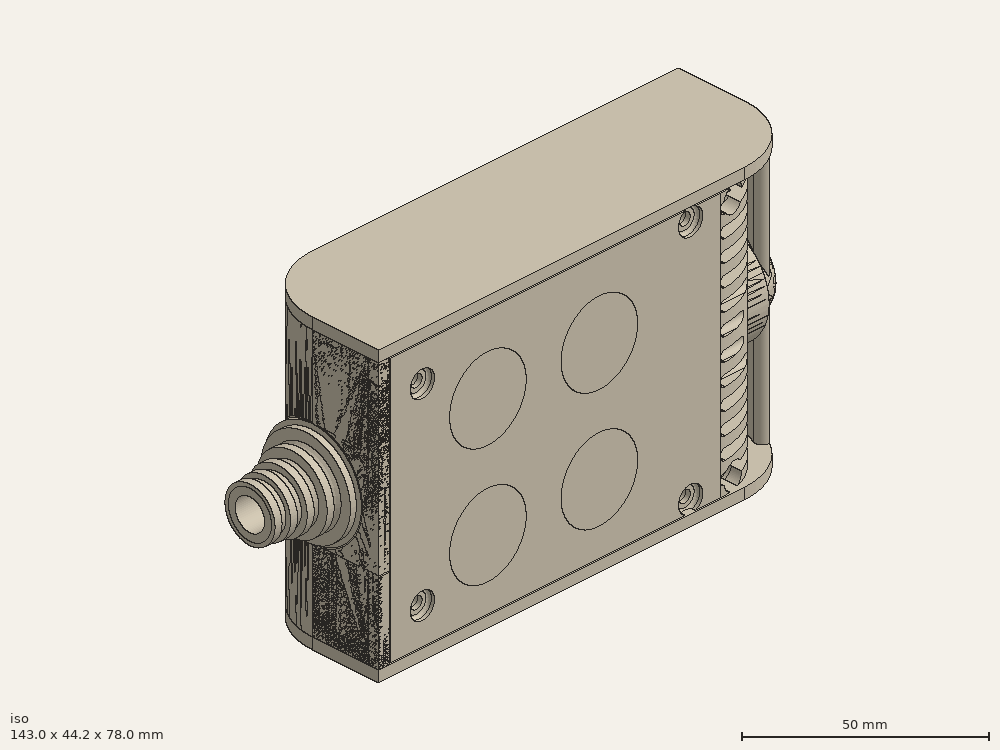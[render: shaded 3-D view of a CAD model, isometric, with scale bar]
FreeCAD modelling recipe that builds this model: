
FCSTD DOCUMENT  (FreeCAD 0.19R0.19.2)
Label: enclosure_138
License: All rights reserved
LicenseURL: http://en.wikipedia.org/wiki/All_rights_reserved
objects: Part::Feature×90, Part::Revolution×90, Part::MultiFuse×67, Sketcher::SketchObject×48, Part::Extrusion×36, Part::Cut×33, Part::Fillet×27, Part::Cylinder×26, Part::Box×19, App::MeasureDistance×4
note: 436 computed .brp shape members not serialized (recipe doc carries the construction recipe); baked Part::Feature solids carry a one-line shape summary decoded from their .brp

FEATURE [Sketcher::SketchObject] Sketch  label="topSketch"
  FullyConstrained = true
  sketch-geometry (20):
    g0: LineSegment StartX=5.21097e-06 StartY=3 StartZ=0 EndX=5.21097e-06 EndY=19 EndZ=0
    g1: ArcOfCircle CenterX=19 CenterY=19 CenterZ=0 NormalX=0 NormalY=0 NormalZ=1 AngleXU=0 Radius=19 StartAngle=1.5708 EndAngle=3.14159
    g2: ArcOfCircle CenterX=19 CenterY=19 CenterZ=0 NormalX=0 NormalY=0 NormalZ=1 AngleXU=0 Radius=16 StartAngle=1.5708 EndAngle=3.14159
    g3: LineSegment StartX=114 StartY=35 StartZ=0 EndX=19 EndY=35 EndZ=0
    g4: LineSegment StartX=5.21097e-06 StartY=3 StartZ=0 EndX=5.21097e-06 EndY=0 EndZ=0
    g5: LineSegment StartX=3 StartY=0 StartZ=0 EndX=5.21097e-06 EndY=0 EndZ=0
    g6: LineSegment StartX=3 StartY=19 StartZ=0 EndX=3 EndY=0 EndZ=0
    g7: LineSegment StartX=19 StartY=38 StartZ=0 EndX=124 EndY=38 EndZ=0
    g8: Circle CenterX=119 CenterY=35 CenterZ=0 NormalX=0 NormalY=0 NormalZ=1 AngleXU=0 Radius=1
    g9: Circle CenterX=121 CenterY=35 CenterZ=0 NormalX=0 NormalY=0 NormalZ=1 AngleXU=0 Radius=1
    g10: Circle CenterX=121 CenterY=33 CenterZ=0 NormalX=0 NormalY=0 NormalZ=1 AngleXU=0 Radius=1
    g11: BSplineCurve PolesCount=3 KnotsCount=2 Degree=2 IsPeriodic=0
    g12: GeomPoint X=119 Y=35 Z=0
    g13: GeomPoint X=121 Y=33 Z=0
    g14: LineSegment StartX=119 StartY=35 StartZ=0 EndX=114 EndY=35 EndZ=0
    g15: ArcOfCircle CenterX=105 CenterY=19 CenterZ=0 NormalX=0 NormalY=0 NormalZ=1 AngleXU=0 Radius=19 StartAngle=5.7297 EndAngle=6.28319
    g16: ArcOfCircle CenterX=105 CenterY=19 CenterZ=0 NormalX=0 NormalY=0 NormalZ=1 AngleXU=0 Radius=16 StartAngle=5.60905 EndAngle=6.28319
    g17: LineSegment StartX=121 StartY=33 StartZ=0 EndX=121 EndY=19 EndZ=0
    g18: LineSegment StartX=124 StartY=38 StartZ=0 EndX=124 EndY=19 EndZ=0
    g19: LineSegment StartX=117.5 StartY=9.01251 StartZ=0 EndX=121.163 EndY=9.0125 EndZ=0
  constraints (46):
    c: Vertical(g0)
    c: Block(g0)
    c: Coincident(g1,g0)
    c: Block(g1)
    c: Coincident(g2,g1)
    c: Block(g2)
    c: Coincident(g3,g2)
    c: Horizontal(g3)
    c: Tangent(g3,g2)
    c: Coincident(g4,g0)
    c: Distance(g4) = 3
    c: Vertical(g4)
    c: Coincident(g5,g4)
    c: Horizontal(g5)
    c: Coincident(g6,g2)
    c: Coincident(g6,g5)
    c: Vertical(g6)
    c: Horizontal(g7)
    c: Distance(g7) = 105
    c: Coincident(g7,g1)
    c: Block(g3)
    c: Weight(g8) = 1
    c: Equal(g8,g9)
    c: Equal(g8,g10)
    c: InternalAlignment(g8,g11)
    c: InternalAlignment(g9,g11)
    c: InternalAlignment(g10,g11)
    c: InternalAlignment(g12,g11)
    c: InternalAlignment(g13,g11)
    c: Block(g11)
    c: Coincident(g14,g11)
    c: Coincident(g14,g3)
    c: Horizontal(g14)
    c: Block(g15)
    c: Coincident(g16,g15)
    c: Block(g16)
    c: Coincident(g17,g11)
    c: Coincident(g17,g16)
    c: Vertical(g17)
    c: Distance(g17) = 14
    c: Coincident(g18,g7)
    c: Coincident(g18,g15)
    c: Vertical(g18)
    c: Distance(g18) = 19
    c: Coincident(g19,g16)
    c: Coincident(g19,g15)
FEATURE [Sketcher::SketchObject] Sketch001  label="bottomSketch"
  FullyConstrained = true
  sketch-geometry (32):
    g0: LineSegment StartX=3.3 StartY=-6.03275e-07 StartZ=0 EndX=98 EndY=-6.03275e-07 EndZ=0
    g1: ArcOfCircle CenterX=98 CenterY=19 CenterZ=0 NormalX=0 NormalY=0 NormalZ=1 AngleXU=0 Radius=19 StartAngle=4.71239 EndAngle=5.71103
    g2: LineSegment StartX=6.3 StartY=8 StartZ=0 EndX=3.3 EndY=8 EndZ=0
    g3: LineSegment StartX=3.3 StartY=8 StartZ=0 EndX=3.3 EndY=-6.03275e-07 EndZ=0
    g4: ArcOfCircle CenterX=8.3 CenterY=5 CenterZ=0 NormalX=0 NormalY=0 NormalZ=1 AngleXU=0 Radius=2 StartAngle=3.14159 EndAngle=4.71239
    g5: LineSegment StartX=6.3 StartY=8 StartZ=0 EndX=6.3 EndY=5 EndZ=0
    g6: ArcOfCircle CenterX=98 CenterY=19 CenterZ=0 NormalX=0 NormalY=0 NormalZ=1 AngleXU=0 Radius=12.7 StartAngle=4.71239 EndAngle=6.28319
    g7: LineSegment StartX=94.7 StartY=3 StartZ=0 EndX=8.3 EndY=3 EndZ=0
    g8-g12: Circle x5 (B-spline internal-alignment scaffolding for g13; pole/knot coordinates omitted)
    g13: BSplineCurve PolesCount=5 KnotsCount=3 Degree=3 IsPeriodic=0
    g14: GeomPoint X=98 Y=6.3 Z=0
    g15: GeomPoint X=96.3938 Y=4.71946 Z=0
    g16: GeomPoint X=94.7 Y=3 Z=0
    g17-g23: Circle x7 (B-spline internal-alignment scaffolding for g24; pole/knot coordinates omitted)
    g24: BSplineCurve PolesCount=7 KnotsCount=5 Degree=3 IsPeriodic=0
    g25-g29: GeomPoint x5 (B-spline internal-alignment scaffolding for g24; pole/knot coordinates omitted)
    g30: ArcOfCircle CenterX=98 CenterY=19 CenterZ=0 NormalX=0 NormalY=0 NormalZ=1 AngleXU=0 Radius=15.7 StartAngle=5.81226 EndAngle=6.28319
    g31: LineSegment StartX=110.7 StartY=19 StartZ=0 EndX=113.7 EndY=19 EndZ=0
  constraints (41):
    c: Horizontal(g0)
    c: Coincident(g1,g0)
    c: Block(g1)
    c: Horizontal(g2)
    c: Distance(g2) = 3
    c: Coincident(g3,g2)
    c: Vertical(g3)
    c: Coincident(g3,g0)
    c: Block(g4)
    c: Block(g2)
    c: Coincident(g5,g2)
    c: Coincident(g5,g4)
    c: Vertical(g5)
    c: Coincident(g6,g1)
    c: Block(g6)
    c: Coincident(g7,g4)
    c: Horizontal(g7)
    c: Block(g0)
    c: Block(g7)
    c: Block(g3)
    c: Coincident(g13,g6)
    c: Weight(g8) = 1
    c: Equal(g8, g9-g12) x4
    c: Coincident(g13,g7)
    c: InternalAlignment(g8-g12 -> g13) x5
    c: InternalAlignment(g14,g13)
    c: InternalAlignment(g15,g13)
    c: InternalAlignment(g16,g13)
    c: Block(g13)
    c: Weight(g17) = 1
    c: Equal(g17, g18-g23) x6
    c: Coincident(g24,g1)
    c: InternalAlignment(g17-g23 -> g24) x7
    c: InternalAlignment(g25-g29 -> g24) x5
    c: Block(g24)
    c: Coincident(g30,g24)
    c: Coincident(g31,g6)
    c: Coincident(g31,g30)
    c: Horizontal(g31)
    c: Block(g31)
    c: Block(g30)
FEATURE [Part::Extrusion] Extrude  label="top"
  Base = -> Sketch
  Dir = (0,0,1)
  DirMode = 2
  FaceMakerClass = Part::FaceMakerBullseye
  LengthFwd = 72
  LengthRev = 0
  Solid = true
  Symmetric = false
FEATURE [Part::Extrusion] Extrude001  label="bottom"
  Base = -> Sketch001
  Dir = (0,0,1)
  DirMode = 2
  FaceMakerClass = Part::FaceMakerBullseye
  LengthFwd = 71.4
  LengthRev = 0
  Placement = pos=(0,0,0.3) rot=(0,0,1;0rad)
  Solid = true
  Symmetric = false
FEATURE [Sketcher::SketchObject] Sketch002  label="topSketch001"
  FullyConstrained = true
  sketch-geometry (6):
    g0: ArcOfCircle CenterX=19 CenterY=19 CenterZ=0 NormalX=0 NormalY=0 NormalZ=1 AngleXU=0 Radius=19 StartAngle=1.5708 EndAngle=3.14159
    g1: LineSegment StartX=5.22862e-06 StartY=19 StartZ=0 EndX=5.22862e-06 EndY=1.19904e-11 EndZ=0
    g2: LineSegment StartX=19 StartY=38 StartZ=0 EndX=124 EndY=38 EndZ=0
    g3: LineSegment StartX=5.22862e-06 StartY=1.19904e-11 StartZ=0 EndX=105 EndY=1.19904e-11 EndZ=0
    g4: ArcOfCircle CenterX=105 CenterY=19 CenterZ=0 NormalX=0 NormalY=0 NormalZ=1 AngleXU=0 Radius=19 StartAngle=4.71239 EndAngle=6.28319
    g5: LineSegment StartX=124 StartY=38 StartZ=0 EndX=124 EndY=19 EndZ=0
  constraints (16):
    c: Block(g0)
    c: Coincident(g1,g0)
    c: Vertical(g1)
    c: Horizontal(g2)
    c: Distance(g2) = 105
    c: Coincident(g2,g0)
    c: Distance(g1) = 19
    c: Coincident(g3,g1)
    c: Horizontal(g3)
    c: Distance(g3) = 105
    c: Block(g4)
    c: Coincident(g4,g3)
    c: Coincident(g5,g2)
    c: Coincident(g5,g4)
    c: Vertical(g5)
    c: Distance(g5) = 19
FEATURE [Part::Extrusion] Extrude002  label="sideA"
  Base = -> Sketch002
  Dir = (0,0,1)
  DirMode = 2
  FaceMakerClass = Part::FaceMakerBullseye
  LengthFwd = 3
  LengthRev = 0
  Placement = pos=(0,0,-3) rot=(0,0,1;0rad)
  Solid = true
  Symmetric = false
FEATURE [Sketcher::SketchObject] Sketch003  label="topSketch002"
  FullyConstrained = true
  sketch-geometry (6):
    g0: LineSegment StartX=19 StartY=38 StartZ=0 EndX=117 EndY=38 EndZ=0
    g1: ArcOfCircle CenterX=19 CenterY=19 CenterZ=0 NormalX=0 NormalY=0 NormalZ=1 AngleXU=0 Radius=19 StartAngle=1.5708 EndAngle=3.14159
    g2: LineSegment StartX=117 StartY=38 StartZ=0 EndX=117 EndY=19 EndZ=0
    g3: LineSegment StartX=98 StartY=1.0161e-12 StartZ=0 EndX=5.22862e-06 EndY=1.0161e-12 EndZ=0
    g4: LineSegment StartX=5.22862e-06 StartY=19 StartZ=0 EndX=5.22862e-06 EndY=1.0161e-12 EndZ=0
    g5: ArcOfCircle CenterX=98 CenterY=19 CenterZ=0 NormalX=0 NormalY=0 NormalZ=1 AngleXU=0 Radius=19 StartAngle=4.71239 EndAngle=6.28319
  constraints (16):
    c: Horizontal(g0)
    c: Distance(g0) = 98
    c: Coincident(g1,g0)
    c: Block(g1)
    c: Coincident(g2,g0)
    c: Vertical(g2)
    c: Distance(g2) = 19
    c: Horizontal(g3)
    c: Coincident(g4,g1)
    c: Vertical(g4)
    c: Coincident(g3,g4)
    c: Block(g3)
    c: Coincident(g5,g2)
    c: Coincident(g5,g3)
    c: Block(g0)
    c: Block(g5)
FEATURE [Sketcher::SketchObject] Sketch004
  FullyConstrained = true
  MapMode = 3
  Placement = pos=(0,0,0) rot=(1,0,0;1.5708rad)
  Support = -> [Extrude]
  sketch-geometry (8):
    g0: Circle CenterX=80.351 CenterY=-67.6202 CenterZ=0 NormalX=0 NormalY=0 NormalZ=1 AngleXU=0 Radius=2
    g1: Circle CenterX=80.351 CenterY=-67.6202 CenterZ=0 NormalX=0 NormalY=0 NormalZ=1 AngleXU=0 Radius=3
    g2: Circle CenterX=80.351 CenterY=-4.92017 CenterZ=0 NormalX=0 NormalY=0 NormalZ=1 AngleXU=0 Radius=2
    g3: Circle CenterX=80.351 CenterY=-4.92017 CenterZ=0 NormalX=0 NormalY=0 NormalZ=1 AngleXU=0 Radius=3
    g4: Circle CenterX=23.851 CenterY=-4.92017 CenterZ=0 NormalX=0 NormalY=0 NormalZ=1 AngleXU=0 Radius=2
    g5: Circle CenterX=23.851 CenterY=-4.92017 CenterZ=0 NormalX=0 NormalY=0 NormalZ=1 AngleXU=0 Radius=3
    g6: Circle CenterX=23.851 CenterY=-67.6202 CenterZ=0 NormalX=0 NormalY=0 NormalZ=1 AngleXU=0 Radius=2
    g7: Circle CenterX=23.851 CenterY=-67.6202 CenterZ=0 NormalX=0 NormalY=0 NormalZ=1 AngleXU=0 Radius=3
  constraints (8):
    c: Block(g3)
    c: Block(g2)
    c: Block(g1)
    c: Block(g0)
    c: Block(g6)
    c: Block(g7)
    c: Block(g4)
    c: Block(g5)
FEATURE [Part::Extrusion] Extrude004
  Base = -> Sketch004
  Dir = (0,-1,2e-16)
  DirMode = 2
  FaceMakerClass = Part::FaceMakerBullseye
  LengthFwd = 6
  LengthRev = 0
  Placement = pos=(0,9,0) rot=(0,0,1;0rad)
  Solid = true
  Symmetric = false
FEATURE [Sketcher::SketchObject] Sketch005
  FullyConstrained = true
  MapMode = 3
  Placement = pos=(0,0,0) rot=(1,0,0;1.5708rad)
  Support = -> [Extrude]
  sketch-geometry (8):
    g0: Circle CenterX=80.351 CenterY=-67.6202 CenterZ=0 NormalX=0 NormalY=0 NormalZ=1 AngleXU=0 Radius=3
    g1: Circle CenterX=80.351 CenterY=-4.92017 CenterZ=0 NormalX=0 NormalY=0 NormalZ=1 AngleXU=0 Radius=3
    g2: Circle CenterX=23.851 CenterY=-4.92017 CenterZ=0 NormalX=0 NormalY=0 NormalZ=1 AngleXU=0 Radius=3
    g3: Circle CenterX=23.851 CenterY=-67.6202 CenterZ=0 NormalX=0 NormalY=0 NormalZ=1 AngleXU=0 Radius=3
    g4: Circle CenterX=23.851 CenterY=-67.6202 CenterZ=0 NormalX=0 NormalY=0 NormalZ=1 AngleXU=0 Radius=5
    g5: Circle CenterX=80.351 CenterY=-67.6202 CenterZ=0 NormalX=0 NormalY=0 NormalZ=1 AngleXU=0 Radius=5
    g6: Circle CenterX=23.851 CenterY=-4.92017 CenterZ=0 NormalX=0 NormalY=0 NormalZ=1 AngleXU=0 Radius=5
    g7: Circle CenterX=80.351 CenterY=-4.92017 CenterZ=0 NormalX=0 NormalY=0 NormalZ=1 AngleXU=0 Radius=5
  constraints (8):
    c: Block(g1)
    c: Block(g0)
    c: Block(g3)
    c: Block(g2)
    c: Block(g5)
    c: Block(g4)
    c: Block(g6)
    c: Block(g7)
FEATURE [Part::Extrusion] Extrude005
  Base = -> Sketch005
  Dir = (0,-1,2e-16)
  DirMode = 2
  FaceMakerClass = Part::FaceMakerBullseye
  LengthFwd = 2
  LengthRev = 0
  Solid = true
  Symmetric = false
FEATURE [Sketcher::SketchObject] Sketch006
  FullyConstrained = true
  MapMode = 3
  Placement = pos=(0,0,0) rot=(1,0,0;1.5708rad)
  sketch-geometry (8):
    g0: Circle CenterX=80.351 CenterY=-67.6202 CenterZ=0 NormalX=0 NormalY=0 NormalZ=1 AngleXU=0 Radius=3
    g1: Circle CenterX=80.351 CenterY=-4.92017 CenterZ=0 NormalX=0 NormalY=0 NormalZ=1 AngleXU=0 Radius=3
    g2: Circle CenterX=23.851 CenterY=-4.92017 CenterZ=0 NormalX=0 NormalY=0 NormalZ=1 AngleXU=0 Radius=3
    g3: Circle CenterX=23.851 CenterY=-67.6202 CenterZ=0 NormalX=0 NormalY=0 NormalZ=1 AngleXU=0 Radius=3
    g4: Circle CenterX=23.851 CenterY=-67.6202 CenterZ=0 NormalX=0 NormalY=0 NormalZ=1 AngleXU=0 Radius=5
    g5: Circle CenterX=80.351 CenterY=-67.6202 CenterZ=0 NormalX=0 NormalY=0 NormalZ=1 AngleXU=0 Radius=5
    g6: Circle CenterX=23.851 CenterY=-4.92017 CenterZ=0 NormalX=0 NormalY=0 NormalZ=1 AngleXU=0 Radius=5
    g7: Circle CenterX=80.351 CenterY=-4.92017 CenterZ=0 NormalX=0 NormalY=0 NormalZ=1 AngleXU=0 Radius=5
  constraints (8):
    c: Block(g1)
    c: Block(g0)
    c: Block(g3)
    c: Block(g2)
    c: Block(g5)
    c: Block(g4)
    c: Block(g6)
    c: Block(g7)
FEATURE [Part::Extrusion] Extrude007
  Base = -> Sketch006
  Dir = (0,-1,2e-16)
  DirMode = 2
  FaceMakerClass = Part::FaceMakerBullseye
  LengthFwd = 2
  LengthRev = 0
  Solid = true
  Symmetric = false
FEATURE [Part::Fillet] Fillet
  Base = -> Extrude007
  Edges = 4 edges r=1.99: [Edge6,Edge12,Edge18,Edge24]
FEATURE [Part::Cut] Cut
  Base = -> Extrude005
  Placement = pos=(0,5,0) rot=(0,0,1;0rad)
  Tool = -> Fillet
FEATURE [Part::MultiFuse] Fusion  label="pCBScrews"
  Placement = pos=(-2.5,0,72.3) rot=(0,0,1;0rad)
  Shapes = -> [Extrude004,Cut]
FEATURE [App::MeasureDistance] Distance  label="Distance: 0.69 mm"
  Distance = 0.685967
  P1 = (24.0138,2.9647,0.3)
  P2 = (23.8901,3,-0.373787)
FEATURE [App::MeasureDistance] Distance001  label="Distance: 0.53 mm"
  Distance = 0.533607
  P1 = (80.2939,3,72.2334)
  P2 = (80.281,2.99661,71.7)
FEATURE [Part::Fillet] Fillet001
  Base = -> Extrude001
  Edges = 1 edges r=2.4: [Edge17]
FEATURE [Part::Fillet] Fillet002  label="bottom001"
  Base = -> Fillet001
  Edges = 1 edges r=2.4: [Edge36]
FEATURE [Part::Fillet] Fillet003  label="top001"
  Base = -> Extrude
  Edges = 1 edges r=2: [Edge1]
FEATURE [Sketcher::SketchObject] Sketch007
  FullyConstrained = true
  sketch-geometry (16):
    g0: LineSegment StartX=4 StartY=0 StartZ=0 EndX=4 EndY=2.4 EndZ=0
    g1: LineSegment StartX=4 StartY=2.4 StartZ=0 EndX=7 EndY=2.4 EndZ=0
    g2: LineSegment StartX=4 StartY=0 StartZ=0 EndX=5.7 EndY=0 EndZ=0
    g3: LineSegment StartX=5.7 StartY=0 StartZ=0 EndX=5.7 EndY=-5.6 EndZ=0
    g4-g8: Circle x5 (B-spline internal-alignment scaffolding for g9; pole/knot coordinates omitted)
    g9: BSplineCurve PolesCount=5 KnotsCount=3 Degree=3 IsPeriodic=0
    g10: GeomPoint X=7 Y=2.4 Z=0
    g11: GeomPoint X=10.4582 Y=-1.55472 Z=0
    g12: GeomPoint X=14 Y=-5.6 Z=0
    g13: LineSegment StartX=14 StartY=-5.6 StartZ=0 EndX=14 EndY=-14.1 EndZ=0
    g14: LineSegment StartX=14 StartY=-14.1 StartZ=0 EndX=6.5 EndY=-14.1 EndZ=0
    g15: LineSegment StartX=5.7 StartY=-5.6 StartZ=0 EndX=6.5 EndY=-14.1 EndZ=0
  constraints (28):
    c: Distance(g0) = 2.4
    c: Vertical(g0)
    c: Block(g0)
    c: Coincident(g1,g0)
    c: Horizontal(g1)
    c: Distance(g1) = 3
    c: Coincident(g2,g0)
    c: Horizontal(g2)
    c: Distance(g2) = 1.7
    c: Coincident(g3,g2)
    c: Vertical(g3)
    c: Distance(g3) = 5.6
    c: Coincident(g9,g1)
    c: Weight(g4) = 1
    c: Equal(g4, g5-g8) x4
    c: InternalAlignment(g4-g8 -> g9) x5
    c: InternalAlignment(g10,g9)
    c: InternalAlignment(g11,g9)
    c: InternalAlignment(g12,g9)
    c: Block(g9)
    c: Coincident(g13,g9)
    c: Vertical(g13)
    c: Distance(g13) = 8.5
    c: Coincident(g14,g13)
    c: Horizontal(g14)
    c: Distance(g14) = 7.5
    c: Coincident(g15,g3)
    c: Coincident(g15,g14)
FEATURE [Part::Feature] Face
  shape: bbox 10 x 16.5 x 2e-07 mm, 1 faces, 0 solids (baked)
FEATURE [Part::Revolution] Revolve  label="plugHousing"
  Angle = 360
  Axis = (0,1,0)
  Base = (0,0,0)
  FaceMakerClass = Part::FaceMakerBullseye
  Placement = pos=(0,0,36.15) rot=(0,0,1;0rad)
  Solid = false
  Source = -> Face
  Symmetric = false
FEATURE [Part::Feature] Face001
  shape: bbox 10 x 16.5 x 2e-07 mm, 1 faces, 0 solids (baked)
FEATURE [Part::Revolution] Revolve001  label="plugHousing001"
  Angle = 360
  Axis = (0,1,0)
  Base = (0,0,0)
  FaceMakerClass = Part::FaceMakerBullseye
  Placement = pos=(0,0,36.15) rot=(0,0,1;0rad)
  Solid = false
  Source = -> Face001
  Symmetric = false
FEATURE [Part::MultiFuse] Fusion001  label="plugHousing002"
  Placement = pos=(0,0,0) rot=(0,0,1;1.5708rad)
  Shapes = -> [Revolve001,Revolve]
FEATURE [Part::Feature] Face002
  shape: bbox 10 x 16.5 x 2e-07 mm, 1 faces, 0 solids (baked)
FEATURE [Part::Revolution] Revolve003  label="plugHousing005"
  Angle = 360
  Axis = (0,1,0)
  Base = (0,0,0)
  FaceMakerClass = Part::FaceMakerBullseye
  Placement = pos=(0,0,36.15) rot=(0,0,1;0rad)
  Solid = false
  Source = -> Face002
  Symmetric = false
FEATURE [Part::Feature] Face003
  shape: bbox 10 x 16.5 x 2e-07 mm, 1 faces, 0 solids (baked)
FEATURE [Part::Revolution] Revolve002  label="plugHousing003"
  Angle = 360
  Axis = (0,1,0)
  Base = (0,0,0)
  FaceMakerClass = Part::FaceMakerBullseye
  Placement = pos=(0,0,36.15) rot=(0,0,1;0rad)
  Solid = false
  Source = -> Face003
  Symmetric = false
FEATURE [Part::MultiFuse] Fusion002  label="plugHousing004"
  Placement = pos=(0,0,0) rot=(0,0,1;1.5708rad)
  Shapes = -> [Revolve002,Revolve003]
FEATURE [Part::MultiFuse] Fusion003  label="plugHousing006"
  Placement = pos=(0,19,0) rot=(0,0,1;3.14159rad)
  Shapes = -> [Fusion002,Fusion001]
FEATURE [Part::Feature] Face004
  shape: bbox 10 x 16.5 x 2e-07 mm, 1 faces, 0 solids (baked)
FEATURE [Part::Revolution] Revolve006  label="plugHousing010"
  Angle = 360
  Axis = (0,1,0)
  Base = (0,0,0)
  FaceMakerClass = Part::FaceMakerBullseye
  Placement = pos=(0,0,36.15) rot=(0,0,1;0rad)
  Solid = false
  Source = -> Face004
  Symmetric = false
FEATURE [Part::Feature] Face005
  shape: bbox 10 x 16.5 x 2e-07 mm, 1 faces, 0 solids (baked)
FEATURE [Part::Revolution] Revolve007  label="plugHousing011"
  Angle = 360
  Axis = (0,1,0)
  Base = (0,0,0)
  FaceMakerClass = Part::FaceMakerBullseye
  Placement = pos=(0,0,36.15) rot=(0,0,1;0rad)
  Solid = false
  Source = -> Face005
  Symmetric = false
FEATURE [Part::Feature] Face006
  shape: bbox 10 x 16.5 x 2e-07 mm, 1 faces, 0 solids (baked)
FEATURE [Part::Revolution] Revolve004  label="plugHousing007"
  Angle = 360
  Axis = (0,1,0)
  Base = (0,0,0)
  FaceMakerClass = Part::FaceMakerBullseye
  Placement = pos=(0,0,36.15) rot=(0,0,1;0rad)
  Solid = false
  Source = -> Face006
  Symmetric = false
FEATURE [Part::MultiFuse] Fusion004  label="plugHousing009"
  Placement = pos=(0,0,0) rot=(0,0,1;1.5708rad)
  Shapes = -> [Revolve004,Revolve007]
FEATURE [Part::Feature] Face007
  shape: bbox 10 x 16.5 x 2e-07 mm, 1 faces, 0 solids (baked)
FEATURE [Part::Revolution] Revolve005  label="plugHousing008"
  Angle = 360
  Axis = (0,1,0)
  Base = (0,0,0)
  FaceMakerClass = Part::FaceMakerBullseye
  Placement = pos=(0,0,36.15) rot=(0,0,1;0rad)
  Solid = false
  Source = -> Face007
  Symmetric = false
FEATURE [Part::MultiFuse] Fusion005  label="plugHousing012"
  Placement = pos=(0,0,0) rot=(0,0,1;1.5708rad)
  Shapes = -> [Revolve006,Revolve005]
FEATURE [Part::MultiFuse] Fusion006  label="plugHousing013"
  Placement = pos=(0,19,0) rot=(0,0,1;3.14159rad)
  Shapes = -> [Fusion005,Fusion004]
FEATURE [Part::MultiFuse] Fusion007  label="plugHousing014"
  Placement = pos=(122.621,0,-0.15) rot=(0,0,1;0rad)
  Shapes = -> [Fusion003,Fusion006]
FEATURE [Part::Cylinder] Cylinder002
  Angle = 360
  AttacherType = Attacher::AttachEngine3D
  Height = 20
  Placement = pos=(0,0,36.15) rot=(0,0,1;0rad)
  Radius = 4
FEATURE [Part::Cylinder] Cylinder003
  Angle = 360
  AttacherType = Attacher::AttachEngine3D
  Height = 10
  Placement = pos=(0,0,36.15) rot=(0,0,1;0rad)
  Radius = 4
FEATURE [Part::MultiFuse] Fusion009  label="removeToCreateHoleForPlugHousing"
  Placement = pos=(70,19,36.15) rot=(0,1,0;1.5708rad)
  Shapes = -> [Cylinder002,Cylinder003]
FEATURE [Part::Cylinder] Cylinder004
  Angle = 360
  AttacherType = Attacher::AttachEngine3D
  Height = 20
  Placement = pos=(0,0,36.15) rot=(0,0,1;0rad)
  Radius = 4
FEATURE [Part::Cylinder] Cylinder005
  Angle = 360
  AttacherType = Attacher::AttachEngine3D
  Height = 10
  Placement = pos=(0,0,36.15) rot=(0,0,1;0rad)
  Radius = 4
FEATURE [Part::MultiFuse] Fusion010  label="removeToCreateHoleForPlugHousing001"
  Placement = pos=(70,19,36.15) rot=(0,1,0;1.5708rad)
  Shapes = -> [Cylinder004,Cylinder005]
FEATURE [Part::Cut] Cut001
  Base = -> Fillet003
  Tool = -> Fusion010
FEATURE [Part::Cut] Cut002  label="Bottom"
  Base = -> Fillet002
  Tool = -> Fusion009
FEATURE [Part::Feature] Face008
  shape: bbox 10 x 16.5 x 2e-07 mm, 1 faces, 0 solids (baked)
FEATURE [Part::Revolution] Revolve011  label="plugHousing021"
  Angle = 360
  Axis = (0,1,0)
  Base = (0,0,0)
  FaceMakerClass = Part::FaceMakerBullseye
  Placement = pos=(0,0,36.15) rot=(0,0,1;0rad)
  Solid = false
  Source = -> Face008
  Symmetric = false
FEATURE [Part::Feature] Face009
  shape: bbox 10 x 16.5 x 2e-07 mm, 1 faces, 0 solids (baked)
FEATURE [Part::Revolution] Revolve012  label="plugHousing022"
  Angle = 360
  Axis = (0,1,0)
  Base = (0,0,0)
  FaceMakerClass = Part::FaceMakerBullseye
  Placement = pos=(0,0,36.15) rot=(0,0,1;0rad)
  Solid = false
  Source = -> Face009
  Symmetric = false
FEATURE [Part::Feature] Face010 .. Face013  x4 (patterned run collapsed; names and placements below)
  shape: bbox 10 x 16.5 x 2e-07 mm, 1 faces, 0 solids (baked)
FEATURE [Part::Revolution] Revolve015  label="plugHousing027"
  Angle = 360
  Axis = (0,1,0)
  Base = (0,0,0)
  FaceMakerClass = Part::FaceMakerBullseye
  Placement = pos=(0,0,36.15) rot=(0,0,1;0rad)
  Solid = false
  Source = -> Face013
  Symmetric = false
FEATURE [Part::Feature] Face014
  shape: bbox 10 x 16.5 x 2e-07 mm, 1 faces, 0 solids (baked)
FEATURE [Part::Feature] Face015
  shape: bbox 10 x 16.5 x 2e-07 mm, 1 faces, 0 solids (baked)
FEATURE [Part::Feature] Face016
  shape: bbox 10 x 16.5 x 2e-07 mm, 1 faces, 0 solids (baked)
FEATURE [Part::Revolution] Revolve019  label="plugHousing033"
  Angle = 360
  Axis = (0,1,0)
  Base = (0,0,0)
  FaceMakerClass = Part::FaceMakerBullseye
  Placement = pos=(0,0,36.15) rot=(0,0,1;0rad)
  Solid = false
  Source = -> Face016
  Symmetric = false
FEATURE [Part::Feature] Face017
  shape: bbox 10 x 16.5 x 2e-07 mm, 1 faces, 0 solids (baked)
FEATURE [Part::Revolution] Revolve020  label="plugHousing034"
  Angle = 360
  Axis = (0,1,0)
  Base = (0,0,0)
  FaceMakerClass = Part::FaceMakerBullseye
  Placement = pos=(0,0,36.15) rot=(0,0,1;0rad)
  Solid = false
  Source = -> Face017
  Symmetric = false
FEATURE [Part::Feature] Face018
  shape: bbox 10 x 16.5 x 2e-07 mm, 1 faces, 0 solids (baked)
FEATURE [Part::Revolution] Revolve016  label="plugHousing030"
  Angle = 360
  Axis = (0,1,0)
  Base = (0,0,0)
  FaceMakerClass = Part::FaceMakerBullseye
  Placement = pos=(0,0,36.15) rot=(0,0,1;0rad)
  Solid = false
  Source = -> Face018
  Symmetric = false
FEATURE [Part::MultiFuse] Fusion020  label="plugHousing038"
  Placement = pos=(0,0,0) rot=(0,0,1;1.5708rad)
  Shapes = -> [Revolve016,Revolve020]
FEATURE [Part::Feature] Face019
  shape: bbox 10 x 16.5 x 2e-07 mm, 1 faces, 0 solids (baked)
FEATURE [Part::Feature] Face020
  shape: bbox 10 x 16.5 x 2e-07 mm, 1 faces, 0 solids (baked)
FEATURE [Part::Revolution] Revolve017  label="plugHousing031"
  Angle = 360
  Axis = (0,1,0)
  Base = (0,0,0)
  FaceMakerClass = Part::FaceMakerBullseye
  Placement = pos=(0,0,36.15) rot=(0,0,1;0rad)
  Solid = false
  Source = -> Face020
  Symmetric = false
FEATURE [Part::MultiFuse] Fusion021  label="plugHousing039"
  Placement = pos=(0,0,0) rot=(0,0,1;1.5708rad)
  Shapes = -> [Revolve019,Revolve017]
FEATURE [Part::MultiFuse] Fusion023  label="plugHousing041"
  Placement = pos=(0,19,0) rot=(0,0,1;3.14159rad)
  Shapes = -> [Fusion021,Fusion020]
FEATURE [Part::Revolution] Revolve022  label="plugHousing043"
  Angle = 360
  Axis = (0,1,0)
  Base = (0,0,0)
  FaceMakerClass = Part::FaceMakerBullseye
  Placement = pos=(0,0,36.15) rot=(0,0,1;0rad)
  Solid = false
  Source = -> Face019
  Symmetric = false
FEATURE [Part::Feature] Face021
  shape: bbox 10 x 16.5 x 2e-07 mm, 1 faces, 0 solids (baked)
FEATURE [Part::Revolution] Revolve023  label="plugHousing044"
  Angle = 360
  Axis = (0,1,0)
  Base = (0,0,0)
  FaceMakerClass = Part::FaceMakerBullseye
  Placement = pos=(0,0,36.15) rot=(0,0,1;0rad)
  Solid = false
  Source = -> Face021
  Symmetric = false
FEATURE [Part::Feature] Face022
  shape: bbox 10 x 16.5 x 2e-07 mm, 1 faces, 0 solids (baked)
FEATURE [Part::Revolution] Revolve018  label="plugHousing032"
  Angle = 360
  Axis = (0,1,0)
  Base = (0,0,0)
  FaceMakerClass = Part::FaceMakerBullseye
  Placement = pos=(0,0,36.15) rot=(0,0,1;0rad)
  Solid = false
  Source = -> Face022
  Symmetric = false
FEATURE [Part::MultiFuse] Fusion022  label="plugHousing040"
  Placement = pos=(0,0,0) rot=(0,0,1;1.5708rad)
  Shapes = -> [Revolve018,Revolve023]
FEATURE [Part::Feature] Face023
  shape: bbox 10 x 16.5 x 2e-07 mm, 1 faces, 0 solids (baked)
FEATURE [Part::Revolution] Revolve021  label="plugHousing035"
  Angle = 360
  Axis = (0,1,0)
  Base = (0,0,0)
  FaceMakerClass = Part::FaceMakerBullseye
  Placement = pos=(0,0,36.15) rot=(0,0,1;0rad)
  Solid = false
  Source = -> Face023
  Symmetric = false
FEATURE [Part::MultiFuse] Fusion018  label="plugHousing036"
  Placement = pos=(0,0,0) rot=(0,0,1;1.5708rad)
  Shapes = -> [Revolve022,Revolve021]
FEATURE [Part::MultiFuse] Fusion019  label="plugHousing037"
  Placement = pos=(0,19,0) rot=(0,0,1;3.14159rad)
  Shapes = -> [Fusion018,Fusion022]
FEATURE [Part::MultiFuse] Fusion024  label="plugHousing042"
  Placement = pos=(122.621,0,-0.15) rot=(0,0,1;0rad)
  Shapes = -> [Fusion023,Fusion019]
FEATURE [Part::Cylinder] Cylinder006
  Angle = 360
  AttacherType = Attacher::AttachEngine3D
  Height = 20
  Placement = pos=(0,0,36.15) rot=(0,0,1;0rad)
  Radius = 14.3
FEATURE [Part::Cylinder] Cylinder007
  Angle = 360
  AttacherType = Attacher::AttachEngine3D
  Height = 10
  Placement = pos=(0,0,36.15) rot=(0,0,1;0rad)
  Radius = 4
FEATURE [Part::MultiFuse] Fusion026  label="removeToCreteHoleForPlugHousing"
  Placement = pos=(70,19,36) rot=(0,1,0;1.5708rad)
  Shapes = -> [Cylinder006,Cylinder007]
FEATURE [Part::Box] Box001  label="Cube001"
  AttacherType = Attacher::AttachEngine3D
  Height = 28
  Length = 3
  Placement = pos=(110.7,19,22) rot=(0,0,1;0rad)
  Width = 15.7
FEATURE [Part::Cut] Cut003  label="top002"
  Base = -> Cut001
  Tool = -> Fusion007
FEATURE [Part::Revolution] Revolve008  label="plugHousing015"
  Angle = 360
  Axis = (0,1,0)
  Base = (0,0,0)
  FaceMakerClass = Part::FaceMakerBullseye
  Placement = pos=(0,0,36.15) rot=(0,0,1;0rad)
  Solid = false
  Source = -> Face010
  Symmetric = false
FEATURE [Part::MultiFuse] Fusion013  label="plugHousing020"
  Placement = pos=(0,0,0) rot=(0,0,1;1.5708rad)
  Shapes = -> [Revolve008,Revolve012]
FEATURE [Part::Cut] Cut004  label="top003"
  Base = -> Cut003
  Placement = pos=(1,0,0) rot=(0,0,1;0rad)
  Tool = -> Fusion026
FEATURE [Part::Cylinder] Cylinder008
  Angle = 360
  AttacherType = Attacher::AttachEngine3D
  Height = 20
  Placement = pos=(0,0,36.15) rot=(0,0,1;0rad)
  Radius = 10.3
FEATURE [Part::Cylinder] Cylinder009
  Angle = 360
  AttacherType = Attacher::AttachEngine3D
  Height = 10
  Placement = pos=(0,0,36.15) rot=(0,0,1;0rad)
  Radius = 4
FEATURE [Part::MultiFuse] Fusion027  label="removeToCreteHoleForPlugHousing001"
  Placement = pos=(70,19,36) rot=(0,1,0;1.5708rad)
  Shapes = -> [Cylinder008,Cylinder009]
FEATURE [Part::Cut] Cut005  label="plugHousingTab"
  Base = -> Box001
  Tool = -> Fusion027
FEATURE [Part::MultiFuse] Fusion028  label="plugHousing045"
  Shapes = -> [Fusion024,Cut005]
FEATURE [Part::Box] Box002  label="Cube002"
  AttacherType = Attacher::AttachEngine3D
  Height = 28.8
  Length = 3
  Placement = pos=(107.3,28,21.6) rot=(0,0,1;0rad)
  Width = 7
FEATURE [Part::Box] Box003  label="Cube003"
  AttacherType = Attacher::AttachEngine3D
  Height = 3
  Length = 6.4
  Placement = pos=(107.3,28,18.6) rot=(0,0,1;0rad)
  Width = 7
FEATURE [Part::Box] Box004  label="Cube004"
  AttacherType = Attacher::AttachEngine3D
  Height = 3
  Length = 6.4
  Placement = pos=(107.3,28,50.4) rot=(0,0,1;0rad)
  Width = 7
FEATURE [Part::MultiFuse] Fusion029  label="plugHousingBracketHolder"
  Shapes = -> [Box004,Box002,Box003]
FEATURE [Part::Cylinder] Cylinder010
  Angle = 360
  AttacherType = Attacher::AttachEngine3D
  Height = 20
  Placement = pos=(0,0,36.15) rot=(0,0,1;0rad)
  Radius = 14.3
FEATURE [Part::Cylinder] Cylinder011
  Angle = 360
  AttacherType = Attacher::AttachEngine3D
  Height = 10
  Placement = pos=(0,0,36.15) rot=(0,0,1;0rad)
  Radius = 4
FEATURE [Part::MultiFuse] Fusion030  label="removeToCreteHoleForPlugHousing002"
  Placement = pos=(70,19,36) rot=(0,1,0;1.5708rad)
  Shapes = -> [Cylinder010,Cylinder011]
FEATURE [Part::Cut] Cut006  label="plugHousingBracketHolder001"
  Base = -> Fusion029
  Tool = -> Fusion030
FEATURE [Part::Cylinder] Cylinder012
  Angle = 360
  AttacherType = Attacher::AttachEngine3D
  Height = 20
  Placement = pos=(0,0,36.15) rot=(0,0,1;0rad)
  Radius = 7
FEATURE [Part::Cylinder] Cylinder013
  Angle = 360
  AttacherType = Attacher::AttachEngine3D
  Height = 10
  Placement = pos=(0,0,36.15) rot=(0,0,1;0rad)
  Radius = 4
FEATURE [Part::MultiFuse] Fusion032  label="removeToCreteHoleForPlugHousing003"
  Placement = pos=(70,19,36) rot=(0,1,0;1.5708rad)
  Shapes = -> [Cylinder012,Cylinder013]
FEATURE [Part::Cut] Cut007  label="bottom002"
  Base = -> Cut002
  Tool = -> Fusion032
FEATURE [Sketcher::SketchObject] Sketch008
  FullyConstrained = true
  sketch-geometry (54):
    g0: LineSegment StartX=-4.2 StartY=0 StartZ=0 EndX=-6.2 EndY=0 EndZ=0
    g1: LineSegment StartX=-14 StartY=-18 StartZ=0 EndX=-14 EndY=-26.5 EndZ=0
    g2: LineSegment StartX=-4.2 StartY=0 StartZ=0 EndX=-4.2 EndY=-13.4877 EndZ=0
    g3: Circle CenterX=-4.2 CenterY=-13.4877 CenterZ=0 NormalX=0 NormalY=0 NormalZ=1 AngleXU=0 Radius=1
    g4: Circle CenterX=-4.2 CenterY=-26.5 CenterZ=0 NormalX=0 NormalY=0 NormalZ=1 AngleXU=0 Radius=1
    g5: Circle CenterX=-8.2 CenterY=-26.5 CenterZ=0 NormalX=0 NormalY=0 NormalZ=1 AngleXU=0 Radius=1
    g6: BSplineCurve PolesCount=3 KnotsCount=2 Degree=2 IsPeriodic=0
    g7: GeomPoint X=-4.2 Y=-13.4877 Z=0
    g8: GeomPoint X=-8.2 Y=-26.5 Z=0
    g9: LineSegment StartX=-14 StartY=-26.5 StartZ=0 EndX=-8.2 EndY=-26.5 EndZ=0
    g10: LineSegment StartX=-10.15 StartY=-12 StartZ=0 EndX=-10.15 EndY=-14 EndZ=0
    g11: LineSegment StartX=-12.8401 StartY=-16 StartZ=0 EndX=-10.1571 EndY=-16 EndZ=0
    g12: LineSegment StartX=-10.15 StartY=-14 StartZ=0 EndX=-8.70761 EndY=-14 EndZ=0
    g13: LineSegment StartX=-12.8401 StartY=-16 StartZ=0 EndX=-12.8401 EndY=-17.6958 EndZ=0
    g14: LineSegment StartX=-10.15 StartY=-12 StartZ=0 EndX=-7.79258 EndY=-12 EndZ=0
    g15: Circle CenterX=-6.2215 CenterY=-2 CenterZ=0 NormalX=0 NormalY=0 NormalZ=1 AngleXU=0 Radius=1
    g16: Circle CenterX=-6.22762 CenterY=-2.58724 CenterZ=0 NormalX=0 NormalY=0 NormalZ=1 AngleXU=0 Radius=1
    g17: Circle CenterX=-6.32538 CenterY=-4 CenterZ=0 NormalX=0 NormalY=0 NormalZ=1 AngleXU=0 Radius=1
    g18: BSplineCurve PolesCount=3 KnotsCount=2 Degree=2 IsPeriodic=0
    g19: GeomPoint X=-6.2215 Y=-2 Z=0
    g20: GeomPoint X=-6.32538 Y=-4 Z=0
    g21: Circle CenterX=-6.48644 CenterY=-5.99526 CenterZ=0 NormalX=0 NormalY=0 NormalZ=1 AngleXU=0 Radius=1
    g22: Circle CenterX=-6.58486 CenterY=-6.99526 CenterZ=0 NormalX=0 NormalY=0 NormalZ=1 AngleXU=0 Radius=1
    g23: Circle CenterX=-6.77343 CenterY=-8 CenterZ=0 NormalX=0 NormalY=0 NormalZ=1 AngleXU=0 Radius=1
    g24: BSplineCurve PolesCount=3 KnotsCount=2 Degree=2 IsPeriodic=0
    g25: GeomPoint X=-6.48644 Y=-5.99526 Z=0
    g26: GeomPoint X=-6.77343 Y=-8 Z=0
    g27: Circle CenterX=-7.19003 CenterY=-10 CenterZ=0 NormalX=0 NormalY=0 NormalZ=1 AngleXU=0 Radius=1
    g28: Circle CenterX=-7.44407 CenterY=-11.0915 CenterZ=0 NormalX=0 NormalY=0 NormalZ=1 AngleXU=0 Radius=1
    g29: Circle CenterX=-7.79258 CenterY=-12 CenterZ=0 NormalX=0 NormalY=0 NormalZ=1 AngleXU=0 Radius=1
    g30: BSplineCurve PolesCount=3 KnotsCount=2 Degree=2 IsPeriodic=0
    g31: GeomPoint X=-7.19003 Y=-10 Z=0
    g32: GeomPoint X=-7.79258 Y=-12 Z=0
    g33: Circle CenterX=-8.70761 CenterY=-14 CenterZ=0 NormalX=0 NormalY=0 NormalZ=1 AngleXU=0 Radius=1
    g34: Circle CenterX=-9.33087 CenterY=-15.1837 CenterZ=0 NormalX=0 NormalY=0 NormalZ=1 AngleXU=0 Radius=1
    g35: Circle CenterX=-10.1571 CenterY=-16 CenterZ=0 NormalX=0 NormalY=0 NormalZ=1 AngleXU=0 Radius=1
    g36: BSplineCurve PolesCount=3 KnotsCount=2 Degree=2 IsPeriodic=0
    g37: GeomPoint X=-8.70761 Y=-14 Z=0
    g38: GeomPoint X=-10.1571 Y=-16 Z=0
    g39: Circle CenterX=-12.8401 CenterY=-17.6958 CenterZ=0 NormalX=0 NormalY=0 NormalZ=1 AngleXU=0 Radius=1
    g40: Circle CenterX=-13.3521 CenterY=-17.9027 CenterZ=0 NormalX=0 NormalY=0 NormalZ=1 AngleXU=0 Radius=1
    g41: Circle CenterX=-14 CenterY=-18 CenterZ=0 NormalX=0 NormalY=0 NormalZ=1 AngleXU=0 Radius=1
    g42: BSplineCurve PolesCount=3 KnotsCount=2 Degree=2 IsPeriodic=0
    g43: GeomPoint X=-12.8401 Y=-17.6958 Z=0
    g44: GeomPoint X=-14 Y=-18 Z=0
    g45: LineSegment StartX=-6.2 StartY=0 StartZ=0 EndX=-7.2 EndY=0 EndZ=0
    g46: LineSegment StartX=-7.2 StartY=0 StartZ=0 EndX=-7.2 EndY=-2 EndZ=0
    g47: LineSegment StartX=-7.2 StartY=-2 StartZ=0 EndX=-6.2215 EndY=-2 EndZ=0
    g48: LineSegment StartX=-6.32538 StartY=-4 StartZ=0 EndX=-7.65538 EndY=-4 EndZ=0
    g49: LineSegment StartX=-7.65538 StartY=-4 StartZ=0 EndX=-7.65538 EndY=-5.99526 EndZ=0
    g50: LineSegment StartX=-7.65538 StartY=-5.99526 StartZ=0 EndX=-6.48644 EndY=-5.99526 EndZ=0
    g51: LineSegment StartX=-6.77343 StartY=-8 StartZ=0 EndX=-8.43343 EndY=-8 EndZ=0
    g52: LineSegment StartX=-8.43343 StartY=-8 StartZ=0 EndX=-8.43343 EndY=-10 EndZ=0
    g53: LineSegment StartX=-8.43343 StartY=-10 StartZ=0 EndX=-7.19003 EndY=-10 EndZ=0
  constraints (112):
    c: Horizontal(g0)
    c: Distance(g0) = 2
    c: Block(g0)
    c: Vertical(g1)
    c: Coincident(g2,g0)
    c: Vertical(g2)
    c: Block(g2)
    c: Coincident(g6,g2)
    c: Weight(g3) = 1
    c: Equal(g3,g4)
    c: Equal(g3,g5)
    c: InternalAlignment(g3,g6)
    c: InternalAlignment(g4,g6)
    c: InternalAlignment(g5,g6)
    c: InternalAlignment(g7,g6)
    c: InternalAlignment(g8,g6)
    c: Block(g6)
    c: Coincident(g9,g1)
    c: Coincident(g9,g6)
    c: Horizontal(g9)
    c: Vertical(g10)
    c: Block(g10)
    c: Horizontal(g11)
    c: Block(g11)
    c: Coincident(g12,g10)
    c: Horizontal(g12)
    c: Block(g12)
    c: Coincident(g13,g11)
    c: Vertical(g13)
    c: Block(g13)
    c: Coincident(g14,g10)
    c: Horizontal(g14)
    c: Block(g14)
    c: Block(g9)
    c: Block(g1)
    c: Weight(g15) = 1
    c: Equal(g15,g16)
    c: Equal(g15,g17)
    c: InternalAlignment(g15,g18)
    c: InternalAlignment(g16,g18)
    c: InternalAlignment(g17,g18)
    c: InternalAlignment(g19,g18)
    c: InternalAlignment(g20,g18)
    c: Weight(g21) = 1
    c: Equal(g21,g22)
    c: Equal(g21,g23)
    c: InternalAlignment(g21,g24)
    c: InternalAlignment(g22,g24)
    c: InternalAlignment(g23,g24)
    c: InternalAlignment(g25,g24)
    c: InternalAlignment(g26,g24)
    c: Weight(g27) = 1
    c: Equal(g27,g28)
    c: Equal(g27,g29)
    c: Coincident(g30,g14)
    c: InternalAlignment(g27,g30)
    c: InternalAlignment(g28,g30)
    c: InternalAlignment(g29,g30)
    c: InternalAlignment(g31,g30)
    c: InternalAlignment(g32,g30)
    c: Coincident(g36,g12)
    c: Weight(g33) = 1
    c: Equal(g33,g34)
    c: Equal(g33,g35)
    c: Coincident(g36,g11)
    c: InternalAlignment(g33,g36)
    c: InternalAlignment(g34,g36)
    c: InternalAlignment(g35,g36)
    c: InternalAlignment(g37,g36)
    c: InternalAlignment(g38,g36)
    c: Coincident(g42,g13)
    c: Weight(g39) = 1
    c: Equal(g39,g40)
    c: Equal(g39,g41)
    c: Coincident(g42,g1)
    c: InternalAlignment(g39,g42)
    c: InternalAlignment(g40,g42)
    c: InternalAlignment(g41,g42)
    c: InternalAlignment(g43,g42)
    c: InternalAlignment(g44,g42)
    c: Block(g18)
    c: Block(g24)
    c: Block(g30)
    c: Block(g36)
    c: Block(g42)
    c: Horizontal(g45)
    c: Coincident(g45,g0)
    c: Vertical(g46)
    c: Coincident(g46,g45)
    c: Coincident(g47,g46)
    c: Coincident(g47,g18)
    c: Horizontal(g47)
    c: Block(g46)
    c: Coincident(g48,g18)
    c: Horizontal(g48)
    c: Distance(g48) = 1.33
    c: Vertical(g49)
    c: Coincident(g49,g48)
    c: Coincident(g50,g49)
    c: Coincident(g50,g24)
    c: Horizontal(g50)
    c: Tangent(g50,g22)
    c: Horizontal(g51)
    c: Coincident(g51,g24)
    c: Block(g51)
    c: Vertical(g52)
    c: Block(g52)
    c: Coincident(g52,g51)
    c: Coincident(g53,g52)
    c: Coincident(g53,g30)
    c: Horizontal(g53)
    c: Distance(g1) = 8.5
FEATURE [Part::Feature] Face024
  shape: bbox 9.8 x 26.5 x 2e-07 mm, 1 faces, 0 solids (baked)
FEATURE [Part::Revolution] Revolve024
  Angle = 360
  Axis = (0,1,0)
  Base = (0,0,0)
  FaceMakerClass = Part::FaceMakerBullseye
  Placement = pos=(0,0,0) rot=(0,0,1;1.5708rad)
  Solid = false
  Source = -> Face024
  Symmetric = false
FEATURE [Part::Feature] Face025
  shape: bbox 9.8 x 26.5 x 2e-07 mm, 1 faces, 0 solids (baked)
FEATURE [Part::Revolution] Revolve025
  Angle = 360
  Axis = (0,1,0)
  Base = (0,0,0)
  FaceMakerClass = Part::FaceMakerBullseye
  Placement = pos=(0,0,0) rot=(0,0,1;1.5708rad)
  Solid = false
  Source = -> Face025
  Symmetric = false
FEATURE [Part::MultiFuse] Fusion033
  Placement = pos=(-18,19,36) rot=(0,0,1;0rad)
  Shapes = -> [Revolve025,Revolve024]
FEATURE [Part::Cylinder] Cylinder014
  Angle = 360
  AttacherType = Attacher::AttachEngine3D
  Height = 20
  Placement = pos=(0,0,36.15) rot=(0,0,1;0rad)
  Radius = 14.3
FEATURE [Part::Cylinder] Cylinder015
  Angle = 360
  AttacherType = Attacher::AttachEngine3D
  Height = 10
  Placement = pos=(0,0,36.15) rot=(0,0,1;0rad)
  Radius = 4
FEATURE [Part::MultiFuse] Fusion034  label="removeToCreteHoleForPlugHousing004"
  Placement = pos=(-42,19,36) rot=(0,1,0;1.5708rad)
  Shapes = -> [Cylinder014,Cylinder015]
FEATURE [Part::Cut] Cut008  label="top004"
  Base = -> Cut004
  Placement = pos=(-1,0,0) rot=(0,0,1;0rad)
  Tool = -> Fusion034
FEATURE [Part::Box] Box005  label="Cube005"
  AttacherType = Attacher::AttachEngine3D
  Height = 28
  Length = 3
  Placement = pos=(110.7,19,22) rot=(0,0,1;0rad)
  Width = 15.7
FEATURE [Part::Cylinder] Cylinder016
  Angle = 360
  AttacherType = Attacher::AttachEngine3D
  Height = 10
  Placement = pos=(0,0,36.15) rot=(0,0,1;0rad)
  Radius = 4
FEATURE [Part::Cylinder] Cylinder017
  Angle = 360
  AttacherType = Attacher::AttachEngine3D
  Height = 20
  Placement = pos=(0,0,36.15) rot=(0,0,1;0rad)
  Radius = 10.3
FEATURE [Part::MultiFuse] Fusion035  label="removeToCreteHoleForPlugHousing005"
  Placement = pos=(70,19,36) rot=(0,1,0;1.5708rad)
  Shapes = -> [Cylinder017,Cylinder016]
FEATURE [Part::Cut] Cut009  label="plugHousingTab001"
  Base = -> Box005
  Placement = pos=(-107.4,-14,0) rot=(0,0,1;0rad)
  Tool = -> Fusion035
FEATURE [Part::Box] Box006  label="Cube006"
  AttacherType = Attacher::AttachEngine3D
  Height = 28
  Length = 3
  Placement = pos=(110.7,19,22) rot=(0,0,1;0rad)
  Width = 15.7
FEATURE [Part::Cylinder] Cylinder018
  Angle = 360
  AttacherType = Attacher::AttachEngine3D
  Height = 10
  Placement = pos=(0,0,36.15) rot=(0,0,1;0rad)
  Radius = 4
FEATURE [Part::Cylinder] Cylinder019
  Angle = 360
  AttacherType = Attacher::AttachEngine3D
  Height = 20
  Placement = pos=(0,0,36.15) rot=(0,0,1;0rad)
  Radius = 10.3
FEATURE [Part::MultiFuse] Fusion036  label="removeToCreteHoleForPlugHousing006"
  Placement = pos=(70,19,36) rot=(0,1,0;1.5708rad)
  Shapes = -> [Cylinder019,Cylinder018]
FEATURE [Part::Cut] Cut010  label="plugHousingTab002"
  Base = -> Box006
  Placement = pos=(-107.4,-14,0) rot=(0,0,1;0rad)
  Tool = -> Fusion036
FEATURE [Part::MultiFuse] Fusion037
  Placement = pos=(9.6,23,0) rot=(0,0,1;3.14159rad)
  Shapes = -> [Cut009,Cut010]
FEATURE [Part::Box] Box  label="Cube"
  AttacherType = Attacher::AttachEngine3D
  Height = 10
  Length = 3
  Placement = pos=(3.3,4,12) rot=(0,0,1;0rad)
  Width = 10
FEATURE [Part::Fillet] Fillet004
  Base = -> Fusion028
  Edges = 1 edges r=2: [Edge25]
FEATURE [Part::Fillet] Fillet005  label="plugHousing046"
  Base = -> Fillet004
  Edges = 1 edges r=2: [Edge8]
FEATURE [Part::Fillet] Fillet006
  Base = -> Box
  Edges = 1 edges r=2: [Edge11]
FEATURE [Part::Box] Box007  label="Cube007"
  AttacherType = Attacher::AttachEngine3D
  Height = 10
  Length = 3
  Placement = pos=(3.3,4,50) rot=(0,0,1;0rad)
  Width = 10
FEATURE [Part::Fillet] Fillet007
  Base = -> Box007
  Edges = 1 edges r=2: [Edge12]
FEATURE [Part::Box] Box008  label="Cube008"
  AttacherType = Attacher::AttachEngine3D
  Height = 28
  Length = 4
  Placement = pos=(5,0,22) rot=(0,0,1;0rad)
  Width = 10
FEATURE [Part::Fillet] Fillet008
  Base = -> Box008
  Edges = 1 edges r=1: [Edge7]
FEATURE [Part::Fillet] Fillet009
  Base = -> Fillet008
  Edges = 1 edges r=2: [Edge5]
FEATURE [Part::Fillet] Fillet010
  Base = -> Fillet009
  Edges = 1 edges r=2: [Edge2]
FEATURE [Sketcher::SketchObject] Sketch009  label="topSketch003"
  FullyConstrained = true
  sketch-geometry (4):
    g0: LineSegment StartX=16.8446 StartY=31.512 StartZ=0 EndX=16.3251 EndY=34.4666 EndZ=0
    g1: ArcOfCircle CenterX=19 CenterY=19.2524 CenterZ=0 NormalX=0 NormalY=0 NormalZ=1 AngleXU=0 Radius=15.4476 StartAngle=1.74483 EndAngle=2.72717
    g2: ArcOfCircle CenterX=19 CenterY=19.2524 CenterZ=0 NormalX=0 NormalY=0 NormalZ=1 AngleXU=0 Radius=12.4476 StartAngle=1.74483 EndAngle=2.73189
    g3: LineSegment StartX=4.86004 StartY=25.4725 StartZ=0 EndX=7.58253 EndY=24.2107 EndZ=0
  constraints (7):
    c: Block(g0)
    c: Coincident(g1,g0)
    c: Coincident(g2,g0)
    c: Coincident(g3,g1)
    c: Coincident(g3,g2)
    c: Block(g1)
    c: Block(g2)
FEATURE [Part::Extrusion] Extrude008
  Base = -> Sketch009
  Dir = (0,0,1)
  DirMode = 2
  FaceMakerClass = Part::FaceMakerBullseye
  LengthFwd = 10
  LengthRev = 0
  Placement = pos=(0,0,31) rot=(0,0,1;0rad)
  Solid = true
  Symmetric = false
FEATURE [Part::Cylinder] Cylinder020
  Angle = 360
  AttacherType = Attacher::AttachEngine3D
  Height = 20
  Placement = pos=(0,0,36.15) rot=(0,0,1;0rad)
  Radius = 8.2
FEATURE [Part::Cylinder] Cylinder021
  Angle = 360
  AttacherType = Attacher::AttachEngine3D
  Height = 10
  Placement = pos=(0,0,36.15) rot=(0,0,1;0rad)
  Radius = 4
FEATURE [Part::MultiFuse] Fusion038  label="removeToCreteHoleForPlugHousing007"
  Placement = pos=(-42,19,36) rot=(0,1,0;1.5708rad)
  Shapes = -> [Cylinder020,Cylinder021]
FEATURE [Part::Cut] Cut011
  Base = -> Extrude008
  Tool = -> Fusion038
FEATURE [Part::Fillet] Fillet011
  Base = -> Cut011
  Edges = 1 edges r=2: [Edge1]
FEATURE [Part::Fillet] Fillet012
  Base = -> Fillet011
  Edges = 1 edges r=2.5: [Edge1]
FEATURE [Part::Fillet] Fillet013
  Base = -> Fillet012
  Edges = 1 edges r=2.5: [Edge2]
FEATURE [Part::Box] Box010  label="Cube010"
  AttacherType = Attacher::AttachEngine3D
  Height = 16
  Length = 8
  Placement = pos=(12.7,31.52,28) rot=(0,0,1;0rad)
  Width = 4
FEATURE [Sketcher::SketchObject] Sketch010  label="topSketch004"
  FullyConstrained = true
  sketch-geometry (4):
    g0: LineSegment StartX=16.8446 StartY=31.512 StartZ=0 EndX=16.3251 EndY=34.4666 EndZ=0
    g1: ArcOfCircle CenterX=19 CenterY=19.2524 CenterZ=0 NormalX=0 NormalY=0 NormalZ=1 AngleXU=0 Radius=15.4476 StartAngle=1.74483 EndAngle=2.72717
    g2: ArcOfCircle CenterX=19 CenterY=19.2524 CenterZ=0 NormalX=0 NormalY=0 NormalZ=1 AngleXU=0 Radius=12.4476 StartAngle=1.74483 EndAngle=2.73189
    g3: LineSegment StartX=4.86004 StartY=25.4725 StartZ=0 EndX=7.58253 EndY=24.2107 EndZ=0
  constraints (7):
    c: Block(g0)
    c: Coincident(g1,g0)
    c: Coincident(g2,g0)
    c: Coincident(g3,g1)
    c: Coincident(g3,g2)
    c: Block(g1)
    c: Block(g2)
FEATURE [Part::Cylinder] Cylinder022
  Angle = 360
  AttacherType = Attacher::AttachEngine3D
  Height = 10
  Placement = pos=(0,0,36.15) rot=(0,0,1;0rad)
  Radius = 4
FEATURE [Sketcher::SketchObject] Sketch011  label="topSketch005"
  FullyConstrained = true
  sketch-geometry (4):
    g0: LineSegment StartX=16.8446 StartY=31.512 StartZ=0 EndX=16.3251 EndY=34.4666 EndZ=0
    g1: ArcOfCircle CenterX=19 CenterY=19.2524 CenterZ=0 NormalX=0 NormalY=0 NormalZ=1 AngleXU=0 Radius=15.4476 StartAngle=1.74483 EndAngle=2.72717
    g2: ArcOfCircle CenterX=19 CenterY=19.2524 CenterZ=0 NormalX=0 NormalY=0 NormalZ=1 AngleXU=0 Radius=12.4476 StartAngle=1.74483 EndAngle=2.73189
    g3: LineSegment StartX=4.86004 StartY=25.4725 StartZ=0 EndX=7.58253 EndY=24.2107 EndZ=0
  constraints (7):
    c: Block(g0)
    c: Coincident(g1,g0)
    c: Coincident(g2,g0)
    c: Coincident(g3,g1)
    c: Coincident(g3,g2)
    c: Block(g1)
    c: Block(g2)
FEATURE [Part::Extrusion] Extrude010
  Base = -> Sketch011
  Dir = (0,0,1)
  DirMode = 2
  FaceMakerClass = Part::FaceMakerBullseye
  LengthFwd = 10.6
  LengthRev = 0
  Placement = pos=(0,0,31) rot=(0,0,1;0rad)
  Solid = true
  Symmetric = false
FEATURE [Part::Cylinder] Cylinder023
  Angle = 360
  AttacherType = Attacher::AttachEngine3D
  Height = 20
  Placement = pos=(0,0,36.15) rot=(0,0,1;0rad)
  Radius = 8.2
FEATURE [Part::MultiFuse] Fusion039  label="removeToCreteHoleForPlugHousing008"
  Placement = pos=(-42,19,36) rot=(0,1,0;1.5708rad)
  Shapes = -> [Cylinder023,Cylinder022]
FEATURE [Part::Cut] Cut012
  Base = -> Extrude010
  Placement = pos=(0,0,-0.3) rot=(0,0,1;0rad)
  Tool = -> Fusion039
FEATURE [Part::Cut] Cut013
  Base = -> Box010
  Tool = -> Cut012
FEATURE [Part::Fillet] Fillet014
  Base = -> Cut013
  Edges = 1 edges r=0.7: [Edge13]
FEATURE [Part::Fillet] Fillet015
  Base = -> Fillet014
  Edges = 1 edges r=0.7: [Edge13]
FEATURE [Part::Fillet] Fillet016
  Base = -> Fillet015
  Edges = 1 edges r=0.7: [Edge16]
FEATURE [Part::Fillet] Fillet017
  Base = -> Fillet016
  Edges = 1 edges r=0.7: [Edge11]
FEATURE [Part::Fillet] Fillet018
  Base = -> Fillet017
  Edges = 1 edges r=0.7: [Edge10]
FEATURE [Part::Fillet] Fillet019
  Base = -> Fillet018
  Edges = 1 edges r=1.2: [Edge5]
FEATURE [Part::Fillet] Fillet020
  Base = -> Fillet019
  Edges = 1 edges r=1.2: [Edge12]
FEATURE [Part::Fillet] Fillet021
  Base = -> Fillet020
  Edges = 1 edges r=2: [Edge1]
  Placement = pos=(0.3,0,0) rot=(0,0,1;0rad)
FEATURE [Part::MultiFuse] Fusion040  label="top005"
  Shapes = -> [Cut008,Fillet021]
FEATURE [Part::MultiFuse] Fusion041  label="wireHolder"
  Shapes = -> [Fusion033,Fillet013]
FEATURE [Part::MultiFuse] Fusion042
  Shapes = -> [Fillet007,Fusion041]
FEATURE [Part::MultiFuse] Fusion043  label="wireHolder001"
  Shapes = -> [Fusion042,Fillet010]
FEATURE [Part::MultiFuse] Fusion044  label="wireHolder002"
  Shapes = -> [Fillet006,Fusion037,Fusion043]
FEATURE [Part::Feature] Face026
  shape: bbox 11 x 6 x 2e-07 mm, 1 faces, 0 solids (baked)
FEATURE [Part::Revolution] Revolve026
  Angle = 360
  Axis = (0,1,0)
  Base = (0,0,0)
  FaceMakerClass = Part::FaceMakerBullseye
  Placement = pos=(30.3,-1,19.7) rot=(0,0,1;0rad)
  Solid = false
  Source = -> Face026
  Symmetric = false
FEATURE [Sketcher::SketchObject] Sketch013  label="topSketch006"
  FullyConstrained = true
  sketch-geometry (13):
    g0: LineSegment StartX=117 StartY=19 StartZ=0 EndX=117 EndY=38 EndZ=0
    g1: ArcOfCircle CenterX=98 CenterY=19 CenterZ=0 NormalX=0 NormalY=0 NormalZ=1 AngleXU=0 Radius=19 StartAngle=5.7297 EndAngle=6.28319
    g2: LineSegment StartX=0 StartY=3 StartZ=0 EndX=0 EndY=19 EndZ=0
    g3: LineSegment StartX=19 StartY=38 StartZ=0 EndX=117 EndY=38 EndZ=0
    g4: ArcOfCircle CenterX=19 CenterY=19 CenterZ=0 NormalX=0 NormalY=0 NormalZ=1 AngleXU=0 Radius=19 StartAngle=1.5708 EndAngle=3.14159
    g5: ArcOfCircle CenterX=19 CenterY=19 CenterZ=0 NormalX=0 NormalY=0 NormalZ=1 AngleXU=0 Radius=16 StartAngle=1.5708 EndAngle=3.14159
    g6: ArcOfCircle CenterX=98 CenterY=19 CenterZ=0 NormalX=0 NormalY=0 NormalZ=1 AngleXU=0 Radius=16 StartAngle=5.60905 EndAngle=6.28319
    g7: LineSegment StartX=114 StartY=19 StartZ=0 EndX=114 EndY=35 EndZ=0
    g8: LineSegment StartX=110.5 StartY=9.01251 StartZ=0 EndX=114.163 EndY=9.01251 EndZ=0
    g9: LineSegment StartX=114 StartY=35 StartZ=0 EndX=19 EndY=35 EndZ=0
    g10: LineSegment StartX=0 StartY=3 StartZ=0 EndX=0 EndY=0 EndZ=0
    g11: LineSegment StartX=3 StartY=0 StartZ=0 EndX=0 EndY=0 EndZ=0
    g12: LineSegment StartX=3 StartY=19 StartZ=0 EndX=3 EndY=0 EndZ=0
  constraints (33):
    c: Vertical(g0)
    c: Distance(g0) = 19
    c: Block(g0)
    c: Coincident(g1,g0)
    c: Block(g1)
    c: Vertical(g2)
    c: Block(g2)
    c: Coincident(g3,g0)
    c: Horizontal(g3)
    c: Distance(g3) = 98
    c: Coincident(g4,g3)
    c: Coincident(g4,g2)
    c: Block(g4)
    c: Coincident(g5,g4)
    c: Coincident(g6,g1)
    c: Block(g6)
    c: Block(g5)
    c: Coincident(g7,g6)
    c: Vertical(g7)
    c: Coincident(g8,g6)
    c: Coincident(g8,g1)
    c: Coincident(g9,g7)
    c: Coincident(g9,g5)
    c: Horizontal(g9)
    c: Tangent(g9,g5)
    c: Coincident(g10,g2)
    c: Distance(g10) = 3
    c: Vertical(g10)
    c: Coincident(g11,g10)
    c: Horizontal(g11)
    c: Coincident(g12,g5)
    c: Coincident(g12,g11)
    c: Vertical(g12)
FEATURE [Part::Extrusion] Extrude011  label="top006"
  Base = -> Sketch013
  Dir = (0,0,1)
  DirMode = 2
  FaceMakerClass = Part::FaceMakerBullseye
  LengthFwd = 72
  LengthRev = 0
  Solid = true
  Symmetric = false
FEATURE [Sketcher::SketchObject] Sketch014
  FullyConstrained = true
  MapMode = 3
  Placement = pos=(0,0,0) rot=(1,0,0;1.5708rad)
  Support = -> [Extrude011]
  sketch-geometry (8):
    g0: Circle CenterX=80.351 CenterY=-67.6202 CenterZ=0 NormalX=0 NormalY=0 NormalZ=1 AngleXU=0 Radius=2
    g1: Circle CenterX=80.351 CenterY=-67.6202 CenterZ=0 NormalX=0 NormalY=0 NormalZ=1 AngleXU=0 Radius=3
    g2: Circle CenterX=80.351 CenterY=-4.92017 CenterZ=0 NormalX=0 NormalY=0 NormalZ=1 AngleXU=0 Radius=2
    g3: Circle CenterX=80.351 CenterY=-4.92017 CenterZ=0 NormalX=0 NormalY=0 NormalZ=1 AngleXU=0 Radius=3
    g4: Circle CenterX=23.851 CenterY=-4.92017 CenterZ=0 NormalX=0 NormalY=0 NormalZ=1 AngleXU=0 Radius=2
    g5: Circle CenterX=23.851 CenterY=-4.92017 CenterZ=0 NormalX=0 NormalY=0 NormalZ=1 AngleXU=0 Radius=3
    g6: Circle CenterX=23.851 CenterY=-67.6202 CenterZ=0 NormalX=0 NormalY=0 NormalZ=1 AngleXU=0 Radius=2
    g7: Circle CenterX=23.851 CenterY=-67.6202 CenterZ=0 NormalX=0 NormalY=0 NormalZ=1 AngleXU=0 Radius=3
  constraints (8):
    c: Block(g3)
    c: Block(g2)
    c: Block(g1)
    c: Block(g0)
    c: Block(g6)
    c: Block(g7)
    c: Block(g4)
    c: Block(g5)
FEATURE [Part::Feature] Face027
  shape: bbox 11 x 6 x 2e-07 mm, 1 faces, 0 solids (baked)
FEATURE [Part::Revolution] Revolve027
  Angle = 360
  Axis = (0,1,0)
  Base = (0,0,0)
  FaceMakerClass = Part::FaceMakerBullseye
  Placement = pos=(30.3,-1,51.7) rot=(0,0,1;0rad)
  Solid = false
  Source = -> Face027
  Symmetric = false
FEATURE [Part::Feature] Face028
  shape: bbox 11 x 6 x 2e-07 mm, 1 faces, 0 solids (baked)
FEATURE [Part::Revolution] Revolve028
  Angle = 360
  Axis = (0,1,0)
  Base = (0,0,0)
  FaceMakerClass = Part::FaceMakerBullseye
  Placement = pos=(62.3,-1,19.7) rot=(0,0,1;0rad)
  Solid = false
  Source = -> Face028
  Symmetric = false
FEATURE [Part::Feature] Face029
  shape: bbox 11 x 6 x 2e-07 mm, 1 faces, 0 solids (baked)
FEATURE [Part::Revolution] Revolve029
  Angle = 360
  Axis = (0,1,0)
  Base = (0,0,0)
  FaceMakerClass = Part::FaceMakerBullseye
  Placement = pos=(62.3,-1,51.7) rot=(0,0,1;0rad)
  Solid = false
  Source = -> Face029
  Symmetric = false
FEATURE [Part::Feature] Wire
  shape: bbox 11 x 5.2 x 2e-07 mm, 0 faces, 0 solids (baked)
FEATURE [Part::Revolution] Revolve030
  Angle = 360
  Axis = (0,1,0)
  Base = (0,0,0)
  FaceMakerClass = Part::FaceMakerBullseye
  Placement = pos=(30.3,38,19.7) rot=(0,0,1;0rad)
  Solid = true
  Source = -> Wire
  Symmetric = false
FEATURE [Part::Feature] Wire001
  shape: bbox 11 x 5.2 x 2e-07 mm, 0 faces, 0 solids (baked)
FEATURE [Part::Revolution] Revolve031
  Angle = 360
  Axis = (0,1,0)
  Base = (0,0,0)
  FaceMakerClass = Part::FaceMakerBullseye
  Placement = pos=(30.3,38,51.7) rot=(0,0,1;0rad)
  Solid = true
  Source = -> Wire001
  Symmetric = false
FEATURE [Part::Feature] Wire002
  shape: bbox 11 x 5.2 x 2e-07 mm, 0 faces, 0 solids (baked)
FEATURE [Part::Revolution] Revolve032
  Angle = 360
  Axis = (0,1,0)
  Base = (0,0,0)
  FaceMakerClass = Part::FaceMakerBullseye
  Placement = pos=(62.3,38,51.7) rot=(0,0,1;0rad)
  Solid = true
  Source = -> Wire002
  Symmetric = false
FEATURE [Part::Feature] Wire003
  shape: bbox 11 x 5.2 x 2e-07 mm, 0 faces, 0 solids (baked)
FEATURE [Part::Revolution] Revolve033
  Angle = 360
  Axis = (0,1,0)
  Base = (0,0,0)
  FaceMakerClass = Part::FaceMakerBullseye
  Placement = pos=(62.3,38,19.7) rot=(0,0,1;0rad)
  Solid = true
  Source = -> Wire003
  Symmetric = false
FEATURE [Part::MultiFuse] Fusion045  label="altRandScrewHousing"
  Shapes = -> [Revolve029,Revolve027,Revolve028,Revolve026]
FEATURE [Part::MultiFuse] Fusion046  label="fanScrewHousing"
  Shapes = -> [Revolve033,Revolve032,Revolve031,Revolve030]
FEATURE [Sketcher::SketchObject] Sketch015
  FullyConstrained = true
  sketch-geometry (17):
    g0: Circle CenterX=-3.5 CenterY=23.5 CenterZ=0 NormalX=0 NormalY=0 NormalZ=1 AngleXU=0 Radius=1
    g1: Circle CenterX=-1 CenterY=15.25 CenterZ=0 NormalX=0 NormalY=0 NormalZ=1 AngleXU=0 Radius=1
    g2: Circle CenterX=-3.5 CenterY=7 CenterZ=0 NormalX=0 NormalY=0 NormalZ=1 AngleXU=0 Radius=1
    g3: BSplineCurve PolesCount=3 KnotsCount=2 Degree=2 IsPeriodic=0
    g4: GeomPoint X=-3.5 Y=23.5 Z=0
    g5: GeomPoint X=-3.5 Y=7 Z=0
    g6: Circle CenterX=-4.8 CenterY=30.5 CenterZ=0 NormalX=0 NormalY=0 NormalZ=1 AngleXU=0 Radius=1
    g7: Circle CenterX=-3.5 CenterY=30.5 CenterZ=0 NormalX=0 NormalY=0 NormalZ=1 AngleXU=0 Radius=1
    g8: Circle CenterX=-3.5 CenterY=29.2 CenterZ=0 NormalX=0 NormalY=0 NormalZ=1 AngleXU=0 Radius=1
    g9: BSplineCurve PolesCount=3 KnotsCount=2 Degree=2 IsPeriodic=0
    g10: GeomPoint X=-4.8 Y=30.5 Z=0
    g11: GeomPoint X=-3.5 Y=29.2 Z=0
    g12: LineSegment StartX=-3.5 StartY=29.2 StartZ=0 EndX=-3.5 EndY=23.5 EndZ=0
    g13: LineSegment StartX=-4.8 StartY=30.5 StartZ=0 EndX=0 EndY=30.5 EndZ=0
    g14: LineSegment StartX=-3.5 StartY=0.3 StartZ=0 EndX=0 EndY=0.3 EndZ=0
    g15: LineSegment StartX=-3.5 StartY=0.3 StartZ=0 EndX=-3.5 EndY=7 EndZ=0
    g16: LineSegment StartX=0 StartY=0.3 StartZ=0 EndX=0 EndY=30.5 EndZ=0
  constraints (33):
    c: Weight(g0) = 1
    c: Equal(g0,g1)
    c: Equal(g0,g2)
    c: InternalAlignment(g0,g3)
    c: InternalAlignment(g1,g3)
    c: InternalAlignment(g2,g3)
    c: InternalAlignment(g4,g3)
    c: InternalAlignment(g5,g3)
    c: Block(g3)
    c: Weight(g6) = 1
    c: Equal(g6,g7)
    c: Equal(g6,g8)
    c: InternalAlignment(g6,g9)
    c: InternalAlignment(g7,g9)
    c: InternalAlignment(g8,g9)
    c: InternalAlignment(g10,g9)
    c: InternalAlignment(g11,g9)
    c: Block(g9)
    c: Coincident(g12,g9)
    c: Coincident(g12,g3)
    c: Vertical(g12)
    c: Coincident(g13,g9)
    c: Horizontal(g13)
    c: Distance(g13) = 4.8
    c: Horizontal(g14)
    c: Block(g14)
    c: Coincident(g15,g14)
    c: Coincident(g15,g3)
    c: Vertical(g15)
    c: Coincident(g16,g14)
    c: Coincident(g16,g13)
    c: Vertical(g16)
    c: Tangent(g16,g1)
FEATURE [Sketcher::SketchObject] Sketch016
  FullyConstrained = true
  sketch-geometry (16):
    g0: Circle CenterX=-3.5 CenterY=23.5 CenterZ=0 NormalX=0 NormalY=0 NormalZ=1 AngleXU=0 Radius=1
    g1: Circle CenterX=-1 CenterY=15.25 CenterZ=0 NormalX=0 NormalY=0 NormalZ=1 AngleXU=0 Radius=1
    g2: Circle CenterX=-3.5 CenterY=7 CenterZ=0 NormalX=0 NormalY=0 NormalZ=1 AngleXU=0 Radius=1
    g3: BSplineCurve PolesCount=3 KnotsCount=2 Degree=2 IsPeriodic=0
    g4: GeomPoint X=-3.5 Y=23.5 Z=0
    g5: GeomPoint X=-3.5 Y=7 Z=0
    g6: LineSegment StartX=-3.5 StartY=28.2 StartZ=0 EndX=-3.5 EndY=23.5 EndZ=0
    g7: LineSegment StartX=0 StartY=29.5 StartZ=0 EndX=0 EndY=30 EndZ=0
    g8: LineSegment StartX=-3.5 StartY=28.2 StartZ=0 EndX=-3.5 EndY=30 EndZ=0
    g9: LineSegment StartX=0 StartY=30 StartZ=0 EndX=0 EndY=30.5 EndZ=0
    g10: LineSegment StartX=0 StartY=30.5 StartZ=0 EndX=-3.5 EndY=30.5 EndZ=0
    g11: LineSegment StartX=-3.5 StartY=30.5 StartZ=0 EndX=-3.5 EndY=30 EndZ=0
    g12: LineSegment StartX=0 StartY=29.5 StartZ=0 EndX=0 EndY=5 EndZ=0
    g13: LineSegment StartX=-3.5 StartY=0.3 StartZ=0 EndX=-3.5 EndY=7 EndZ=0
    g14: LineSegment StartX=-3.5 StartY=0.3 StartZ=0 EndX=0 EndY=0.3 EndZ=0
    g15: LineSegment StartX=0 StartY=5 StartZ=0 EndX=0 EndY=0.3 EndZ=0
  constraints (39):
    c: Weight(g0) = 1
    c: Equal(g0,g1)
    c: Equal(g0,g2)
    c: InternalAlignment(g0,g3)
    c: InternalAlignment(g1,g3)
    c: InternalAlignment(g2,g3)
    c: InternalAlignment(g4,g3)
    c: InternalAlignment(g5,g3)
    c: Block(g3)
    c: Coincident(g6,g3)
    c: Vertical(g6)
    c: Vertical(g7)
    c: Distance(g7) = 0.5
    c: Coincident(g8,g6)
    c: Vertical(g8)
    c: Block(g6)
    c: Block(g7)
    c: Vertical(g9)
    c: Equal(g7,g9) = 0.5
    c: Block(g9)
    c: Coincident(g9,g7)
    c: Horizontal(g10)
    c: Coincident(g10,g9)
    c: Coincident(g11,g10)
    c: Coincident(g11,g8)
    c: Vertical(g11)
    c: Block(g11)
    c: Coincident(g12,g7)
    c: Vertical(g12)
    c: Coincident(g13,g3)
    c: Vertical(g13)
    c: Distance(g13) = 6.7
    c: Coincident(g14,g13)
    c: Horizontal(g14)
    c: Block(g14)
    c: Coincident(g15,g12)
    c: Coincident(g15,g14)
    c: Vertical(g15)
    c: Block(g15)
FEATURE [Sketcher::SketchObject] Sketch017
  FullyConstrained = true
  sketch-geometry (11):
    g0: LineSegment StartX=-3.5 StartY=1e-16 StartZ=0 EndX=-1.6 EndY=1e-16 EndZ=0
    g1: LineSegment StartX=-1.6 StartY=1e-16 StartZ=0 EndX=-1.6 EndY=1.5 EndZ=0
    g2: LineSegment StartX=-3.5 StartY=1.5 StartZ=0 EndX=-1.6 EndY=1.5 EndZ=0
    g3: LineSegment StartX=-3.5 StartY=1e-16 StartZ=0 EndX=-4.8 EndY=1e-16 EndZ=0
    g4: Circle CenterX=-3.5 CenterY=1.3 CenterZ=0 NormalX=0 NormalY=0 NormalZ=1 AngleXU=0 Radius=1
    g5: Circle CenterX=-3.5 CenterY=1e-16 CenterZ=0 NormalX=0 NormalY=0 NormalZ=1 AngleXU=0 Radius=1
    g6: Circle CenterX=-4.8 CenterY=1e-16 CenterZ=0 NormalX=0 NormalY=0 NormalZ=1 AngleXU=0 Radius=1
    g7: BSplineCurve PolesCount=3 KnotsCount=2 Degree=2 IsPeriodic=0
    g8: GeomPoint X=-3.5 Y=1.3 Z=0
    g9: GeomPoint X=-4.8 Y=1e-16 Z=0
    g10: LineSegment StartX=-3.5 StartY=1.3 StartZ=0 EndX=-3.5 EndY=1.5 EndZ=0
  constraints (24):
    c: Horizontal(g0)
    c: Distance(g0) = 1.9
    c: Block(g0)
    c: Coincident(g1,g0)
    c: Vertical(g1)
    c: Coincident(g2,g1)
    c: Horizontal(g2)
    c: Coincident(g3,g0)
    c: Horizontal(g3)
    c: Distance(g3) = 1.3
    c: Weight(g4) = 1
    c: Equal(g4,g5)
    c: Coincident(g5,g0)
    c: Equal(g4,g6)
    c: Coincident(g7,g3)
    c: InternalAlignment(g4,g7)
    c: InternalAlignment(g5,g7)
    c: InternalAlignment(g6,g7)
    c: InternalAlignment(g8,g7)
    c: InternalAlignment(g9,g7)
    c: Coincident(g10,g7)
    c: Coincident(g10,g2)
    c: Vertical(g10)
    c: Block(g10)
FEATURE [Part::Feature] Face035
  shape: bbox 3.2 x 1.5 x 2e-07 mm, 1 faces, 0 solids (baked)
FEATURE [Part::Revolution] Revolve039  label="backCaseScrewRetainer"
  Angle = 360
  Axis = (0,1,0)
  Base = (0,0,0)
  FaceMakerClass = Part::FaceMakerBullseye
  Placement = pos=(12.5,3,62) rot=(0,0,1;0rad)
  Solid = false
  Source = -> Face035
  Symmetric = false
FEATURE [Part::Feature] Face036
  shape: bbox 3.2 x 1.5 x 2e-07 mm, 1 faces, 0 solids (baked)
FEATURE [Part::Feature] Face039
  shape: bbox 4.8 x 30.2 x 2e-07 mm, 1 faces, 0 solids (baked)
FEATURE [Part::Revolution] Revolve043  label="frontCaseScrewPost002"
  Angle = 360
  Axis = (0,1,0)
  Base = (0,0,0)
  FaceMakerClass = Part::FaceMakerBullseye
  Placement = pos=(89.5,4.5,3.5) rot=(0,0,1;0rad)
  Solid = false
  Source = -> Face039
  Symmetric = false
FEATURE [Part::Feature] Face042
  shape: bbox 4.8 x 30.2 x 2e-07 mm, 1 faces, 0 solids (baked)
FEATURE [Part::Revolution] Revolve046  label="frontCaseScrewPost003"
  Angle = 360
  Axis = (0,1,0)
  Base = (0,0,0)
  FaceMakerClass = Part::FaceMakerBullseye
  Placement = pos=(89.5,4.5,68.5) rot=(0,0,1;0rad)
  Solid = false
  Source = -> Face042
  Symmetric = false
FEATURE [Part::Feature] Face043
  shape: bbox 3.2 x 1.5 x 2e-07 mm, 1 faces, 0 solids (baked)
FEATURE [Part::Revolution] Revolve047  label="frontCaseScrewRetainer002"
  Angle = 360
  Axis = (0,1,0)
  Base = (0,0,0)
  FaceMakerClass = Part::FaceMakerBullseye
  Placement = pos=(89.5,3,68.5) rot=(0,0,1;0rad)
  Solid = false
  Source = -> Face043
  Symmetric = false
FEATURE [Part::Feature] Face044
  shape: bbox 3.2 x 1.5 x 2e-07 mm, 1 faces, 0 solids (baked)
FEATURE [Part::Revolution] Revolve048  label="frontCaseScrewRetainer003"
  Angle = 360
  Axis = (0,1,0)
  Base = (0,0,0)
  FaceMakerClass = Part::FaceMakerBullseye
  Placement = pos=(89.5,3,3.5) rot=(0,0,1;0rad)
  Solid = false
  Source = -> Face044
  Symmetric = false
FEATURE [App::MeasureDistance] Distance002  label="Distance: 1.67 mm"
  Distance = 1.66921
  P1 = (99.2361,4.7524,71.7)
  P2 = (99.2347,6.42161,71.7)
FEATURE [Sketcher::SketchObject] Sketch018
  FullyConstrained = true
  sketch-geometry (7):
    g0: LineSegment StartX=0 StartY=0 StartZ=0 EndX=0 EndY=6 EndZ=0
    g1: Circle CenterX=0 CenterY=0 CenterZ=0 NormalX=0 NormalY=0 NormalZ=1 AngleXU=0 Radius=1
    g2: Circle CenterX=8 CenterY=6 CenterZ=0 NormalX=0 NormalY=0 NormalZ=1 AngleXU=0 Radius=1
    g3: BSplineCurve PolesCount=3 KnotsCount=2 Degree=2 IsPeriodic=0
    g4: GeomPoint X=0 Y=0 Z=0
    g5: GeomPoint X=8 Y=6 Z=0
    g6: LineSegment StartX=0 StartY=6 StartZ=0 EndX=8 EndY=6 EndZ=0
  constraints (14):
    c: Coincident(g0,g-1)
    c: Distance(g0) = 6
    c: Vertical(g0)
    c: Coincident(g3,g0)
    c: Weight(g1) = 1
    c: Equal(g1,g2)
    c: InternalAlignment(g1,g3)
    c: InternalAlignment(g2,g3)
    c: InternalAlignment(g4,g3)
    c: InternalAlignment(g5,g3)
    c: Block(g3)
    c: Coincident(g6,g0)
    c: Coincident(g6,g3)
    c: Horizontal(g6)
FEATURE [Part::Extrusion] Extrude012  label="caseScrewPillarBracket"
  Base = -> Sketch018
  Dir = (0,0,1)
  DirMode = 2
  FaceMakerClass = Part::FaceMakerBullseye
  LengthFwd = 2.4
  LengthRev = 0
  Placement = pos=(15.76,29,8.8) rot=(0,1,0;0rad)
  Solid = true
  Symmetric = false
FEATURE [Sketcher::SketchObject] Sketch019
  FullyConstrained = true
  sketch-geometry (7):
    g0: LineSegment StartX=0 StartY=0 StartZ=0 EndX=0 EndY=6 EndZ=0
    g1: Circle CenterX=0 CenterY=0 CenterZ=0 NormalX=0 NormalY=0 NormalZ=1 AngleXU=0 Radius=1
    g2: Circle CenterX=8 CenterY=6 CenterZ=0 NormalX=0 NormalY=0 NormalZ=1 AngleXU=0 Radius=1
    g3: BSplineCurve PolesCount=3 KnotsCount=2 Degree=2 IsPeriodic=0
    g4: GeomPoint X=0 Y=0 Z=0
    g5: GeomPoint X=8 Y=6 Z=0
    g6: LineSegment StartX=0 StartY=6 StartZ=0 EndX=8 EndY=6 EndZ=0
  constraints (14):
    c: Coincident(g0,g-1)
    c: Distance(g0) = 6
    c: Vertical(g0)
    c: Coincident(g3,g0)
    c: Weight(g1) = 1
    c: Equal(g1,g2)
    c: InternalAlignment(g1,g3)
    c: InternalAlignment(g2,g3)
    c: InternalAlignment(g4,g3)
    c: InternalAlignment(g5,g3)
    c: Block(g3)
    c: Coincident(g6,g0)
    c: Coincident(g6,g3)
    c: Horizontal(g6)
FEATURE [Part::Extrusion] Extrude013  label="caseScrewPillarBracket001"
  Base = -> Sketch019
  Dir = (0,0,1)
  DirMode = 2
  FaceMakerClass = Part::FaceMakerBullseye
  LengthFwd = 2.4
  LengthRev = 0
  Placement = pos=(15.76,29,60.8) rot=(0,0,1;0rad)
  Solid = true
  Symmetric = false
FEATURE [Sketcher::SketchObject] Sketch020
  FullyConstrained = true
  sketch-geometry (7):
    g0: LineSegment StartX=0 StartY=0 StartZ=0 EndX=0 EndY=6 EndZ=0
    g1: Circle CenterX=0 CenterY=0 CenterZ=0 NormalX=0 NormalY=0 NormalZ=1 AngleXU=0 Radius=1
    g2: Circle CenterX=8 CenterY=6 CenterZ=0 NormalX=0 NormalY=0 NormalZ=1 AngleXU=0 Radius=1
    g3: BSplineCurve PolesCount=3 KnotsCount=2 Degree=2 IsPeriodic=0
    g4: GeomPoint X=0 Y=0 Z=0
    g5: GeomPoint X=8 Y=6 Z=0
    g6: LineSegment StartX=0 StartY=6 StartZ=0 EndX=8 EndY=6 EndZ=0
  constraints (14):
    c: Coincident(g0,g-1)
    c: Distance(g0) = 6
    c: Vertical(g0)
    c: Coincident(g3,g0)
    c: Weight(g1) = 1
    c: Equal(g1,g2)
    c: InternalAlignment(g1,g3)
    c: InternalAlignment(g2,g3)
    c: InternalAlignment(g4,g3)
    c: InternalAlignment(g5,g3)
    c: Block(g3)
    c: Coincident(g6,g0)
    c: Coincident(g6,g3)
    c: Horizontal(g6)
FEATURE [Part::Extrusion] Extrude014  label="caseScrewPillarBracket002"
  Base = -> Sketch020
  Dir = (0,0,1)
  DirMode = 2
  FaceMakerClass = Part::FaceMakerBullseye
  LengthFwd = 2.4
  LengthRev = 0
  Placement = pos=(13.7,29,13.26) rot=(0,-1,0;1.5708rad)
  Solid = true
  Symmetric = false
FEATURE [Sketcher::SketchObject] Sketch021
  FullyConstrained = true
  sketch-geometry (7):
    g0: LineSegment StartX=0 StartY=0 StartZ=0 EndX=0 EndY=6 EndZ=0
    g1: Circle CenterX=0 CenterY=0 CenterZ=0 NormalX=0 NormalY=0 NormalZ=1 AngleXU=0 Radius=1
    g2: Circle CenterX=8 CenterY=6 CenterZ=0 NormalX=0 NormalY=0 NormalZ=1 AngleXU=0 Radius=1
    g3: BSplineCurve PolesCount=3 KnotsCount=2 Degree=2 IsPeriodic=0
    g4: GeomPoint X=0 Y=0 Z=0
    g5: GeomPoint X=8 Y=6 Z=0
    g6: LineSegment StartX=0 StartY=6 StartZ=0 EndX=8 EndY=6 EndZ=0
  constraints (14):
    c: Coincident(g0,g-1)
    c: Distance(g0) = 6
    c: Vertical(g0)
    c: Coincident(g3,g0)
    c: Weight(g1) = 1
    c: Equal(g1,g2)
    c: InternalAlignment(g1,g3)
    c: InternalAlignment(g2,g3)
    c: InternalAlignment(g4,g3)
    c: InternalAlignment(g5,g3)
    c: Block(g3)
    c: Coincident(g6,g0)
    c: Coincident(g6,g3)
    c: Horizontal(g6)
FEATURE [Part::Extrusion] Extrude015  label="caseScrewPillarBracket003"
  Base = -> Sketch021
  Dir = (0,0,1)
  DirMode = 2
  FaceMakerClass = Part::FaceMakerBullseye
  LengthFwd = 2.4
  LengthRev = 0
  Placement = pos=(11.3,29,58.74) rot=(0,1,0;1.5708rad)
  Solid = true
  Symmetric = false
FEATURE [Sketcher::SketchObject] Sketch022
  FullyConstrained = true
  sketch-geometry (7):
    g0: LineSegment StartX=0 StartY=0 StartZ=0 EndX=0 EndY=6 EndZ=0
    g1: Circle CenterX=0 CenterY=0 CenterZ=0 NormalX=0 NormalY=0 NormalZ=1 AngleXU=0 Radius=1
    g2: Circle CenterX=8 CenterY=6 CenterZ=0 NormalX=0 NormalY=0 NormalZ=1 AngleXU=0 Radius=1
    g3: BSplineCurve PolesCount=3 KnotsCount=2 Degree=2 IsPeriodic=0
    g4: GeomPoint X=0 Y=0 Z=0
    g5: GeomPoint X=8 Y=6 Z=0
    g6: LineSegment StartX=0 StartY=6 StartZ=0 EndX=8 EndY=6 EndZ=0
  constraints (14):
    c: Coincident(g0,g-1)
    c: Distance(g0) = 6
    c: Vertical(g0)
    c: Coincident(g3,g0)
    c: Weight(g1) = 1
    c: Equal(g1,g2)
    c: InternalAlignment(g1,g3)
    c: InternalAlignment(g2,g3)
    c: InternalAlignment(g4,g3)
    c: InternalAlignment(g5,g3)
    c: Block(g3)
    c: Coincident(g6,g0)
    c: Coincident(g6,g3)
    c: Horizontal(g6)
FEATURE [Part::Extrusion] Extrude016  label="caseScrewPillarBracket004"
  Base = -> Sketch022
  Dir = (0,0,1)
  DirMode = 2
  FaceMakerClass = Part::FaceMakerBullseye
  LengthFwd = 2.4
  LengthRev = 0
  Placement = pos=(88.3,29,65.23) rot=(0,1,0;1.5708rad)
  Solid = true
  Symmetric = false
FEATURE [Sketcher::SketchObject] Sketch023
  FullyConstrained = true
  sketch-geometry (7):
    g0: LineSegment StartX=0 StartY=0 StartZ=0 EndX=0 EndY=6 EndZ=0
    g1: Circle CenterX=0 CenterY=0 CenterZ=0 NormalX=0 NormalY=0 NormalZ=1 AngleXU=0 Radius=1
    g2: Circle CenterX=8 CenterY=6 CenterZ=0 NormalX=0 NormalY=0 NormalZ=1 AngleXU=0 Radius=1
    g3: BSplineCurve PolesCount=3 KnotsCount=2 Degree=2 IsPeriodic=0
    g4: GeomPoint X=0 Y=0 Z=0
    g5: GeomPoint X=8 Y=6 Z=0
    g6: LineSegment StartX=0 StartY=6 StartZ=0 EndX=8 EndY=6 EndZ=0
  constraints (14):
    c: Coincident(g0,g-1)
    c: Distance(g0) = 6
    c: Vertical(g0)
    c: Coincident(g3,g0)
    c: Weight(g1) = 1
    c: Equal(g1,g2)
    c: InternalAlignment(g1,g3)
    c: InternalAlignment(g2,g3)
    c: InternalAlignment(g4,g3)
    c: InternalAlignment(g5,g3)
    c: Block(g3)
    c: Coincident(g6,g0)
    c: Coincident(g6,g3)
    c: Horizontal(g6)
FEATURE [Part::Extrusion] Extrude017  label="caseScrewPillarBracket005"
  Base = -> Sketch023
  Dir = (0,0,1)
  DirMode = 2
  FaceMakerClass = Part::FaceMakerBullseye
  LengthFwd = 2.4
  LengthRev = 0
  Placement = pos=(90.7,29,6.77) rot=(0,-1,0;1.5708rad)
  Solid = true
  Symmetric = false
FEATURE [Sketcher::SketchObject] Sketch024
  FullyConstrained = true
  sketch-geometry (7):
    g0: LineSegment StartX=0 StartY=0 StartZ=0 EndX=0 EndY=6 EndZ=0
    g1: Circle CenterX=0 CenterY=0 CenterZ=0 NormalX=0 NormalY=0 NormalZ=1 AngleXU=0 Radius=1
    g2: Circle CenterX=8 CenterY=6 CenterZ=0 NormalX=0 NormalY=0 NormalZ=1 AngleXU=0 Radius=1
    g3: BSplineCurve PolesCount=3 KnotsCount=2 Degree=2 IsPeriodic=0
    g4: GeomPoint X=0 Y=0 Z=0
    g5: GeomPoint X=8 Y=6 Z=0
    g6: LineSegment StartX=0 StartY=6 StartZ=0 EndX=8 EndY=6 EndZ=0
  constraints (14):
    c: Coincident(g0,g-1)
    c: Distance(g0) = 6
    c: Vertical(g0)
    c: Coincident(g3,g0)
    c: Weight(g1) = 1
    c: Equal(g1,g2)
    c: InternalAlignment(g1,g3)
    c: InternalAlignment(g2,g3)
    c: InternalAlignment(g4,g3)
    c: InternalAlignment(g5,g3)
    c: Block(g3)
    c: Coincident(g6,g0)
    c: Coincident(g6,g3)
    c: Horizontal(g6)
FEATURE [Part::Extrusion] Extrude018  label="caseScrewPillarBracket006"
  Base = -> Sketch024
  Dir = (0,0,1)
  DirMode = 2
  FaceMakerClass = Part::FaceMakerBullseye
  LengthFwd = 2.4
  LengthRev = 0
  Placement = pos=(103.7,29,6.77) rot=(0,-1,0;1.5708rad)
  Solid = true
  Symmetric = false
FEATURE [Sketcher::SketchObject] Sketch025
  FullyConstrained = true
  sketch-geometry (7):
    g0: LineSegment StartX=0 StartY=0 StartZ=0 EndX=0 EndY=6 EndZ=0
    g1: Circle CenterX=0 CenterY=0 CenterZ=0 NormalX=0 NormalY=0 NormalZ=1 AngleXU=0 Radius=1
    g2: Circle CenterX=8 CenterY=6 CenterZ=0 NormalX=0 NormalY=0 NormalZ=1 AngleXU=0 Radius=1
    g3: BSplineCurve PolesCount=3 KnotsCount=2 Degree=2 IsPeriodic=0
    g4: GeomPoint X=0 Y=0 Z=0
    g5: GeomPoint X=8 Y=6 Z=0
    g6: LineSegment StartX=0 StartY=6 StartZ=0 EndX=8 EndY=6 EndZ=0
  constraints (14):
    c: Coincident(g0,g-1)
    c: Distance(g0) = 6
    c: Vertical(g0)
    c: Coincident(g3,g0)
    c: Weight(g1) = 1
    c: Equal(g1,g2)
    c: InternalAlignment(g1,g3)
    c: InternalAlignment(g2,g3)
    c: InternalAlignment(g4,g3)
    c: InternalAlignment(g5,g3)
    c: Block(g3)
    c: Coincident(g6,g0)
    c: Coincident(g6,g3)
    c: Horizontal(g6)
FEATURE [Part::Extrusion] Extrude019  label="caseScrewPillarBracket007"
  Base = -> Sketch025
  Dir = (0,0,1)
  DirMode = 2
  FaceMakerClass = Part::FaceMakerBullseye
  LengthFwd = 2.4
  LengthRev = 0
  Placement = pos=(101.3,29,65.23) rot=(0,1,0;1.5708rad)
  Solid = true
  Symmetric = false
FEATURE [Part::Box] Box011  label="frontCaseScrewPillarBracket"
  AttacherType = Attacher::AttachEngine3D
  Height = 2.4
  Length = 16
  Placement = pos=(87,28,2.3) rot=(0,0,1;0rad)
  Width = 7
FEATURE [Part::Box] Box012  label="frontCaseScrewPillarBracket001"
  AttacherType = Attacher::AttachEngine3D
  Height = 2.4
  Length = 16
  Placement = pos=(87,28,67.3) rot=(0,0,1;0rad)
  Width = 7
FEATURE [Sketcher::SketchObject] Sketch026
  FullyConstrained = true
  sketch-geometry (17):
    g0: Circle CenterX=-3.5 CenterY=23.5 CenterZ=0 NormalX=0 NormalY=0 NormalZ=1 AngleXU=0 Radius=1
    g1: Circle CenterX=-1 CenterY=15.25 CenterZ=0 NormalX=0 NormalY=0 NormalZ=1 AngleXU=0 Radius=1
    g2: Circle CenterX=-3.5 CenterY=7 CenterZ=0 NormalX=0 NormalY=0 NormalZ=1 AngleXU=0 Radius=1
    g3: BSplineCurve PolesCount=3 KnotsCount=2 Degree=2 IsPeriodic=0
    g4: GeomPoint X=-3.5 Y=23.5 Z=0
    g5: GeomPoint X=-3.5 Y=7 Z=0
    g6: Circle CenterX=-4.8 CenterY=30.5 CenterZ=0 NormalX=0 NormalY=0 NormalZ=1 AngleXU=0 Radius=1
    g7: Circle CenterX=-3.5 CenterY=30.5 CenterZ=0 NormalX=0 NormalY=0 NormalZ=1 AngleXU=0 Radius=1
    g8: Circle CenterX=-3.5 CenterY=29.2 CenterZ=0 NormalX=0 NormalY=0 NormalZ=1 AngleXU=0 Radius=1
    g9: BSplineCurve PolesCount=3 KnotsCount=2 Degree=2 IsPeriodic=0
    g10: GeomPoint X=-4.8 Y=30.5 Z=0
    g11: GeomPoint X=-3.5 Y=29.2 Z=0
    g12: LineSegment StartX=-3.5 StartY=29.2 StartZ=0 EndX=-3.5 EndY=23.5 EndZ=0
    g13: LineSegment StartX=-4.8 StartY=30.5 StartZ=0 EndX=0 EndY=30.5 EndZ=0
    g14: LineSegment StartX=-3.5 StartY=5 StartZ=0 EndX=-3.5 EndY=7 EndZ=0
    g15: LineSegment StartX=0 StartY=5 StartZ=0 EndX=0 EndY=30.5 EndZ=0
    g16: LineSegment StartX=-3.5 StartY=5 StartZ=0 EndX=0 EndY=5 EndZ=0
  constraints (33):
    c: Weight(g0) = 1
    c: Equal(g0,g1)
    c: Equal(g0,g2)
    c: InternalAlignment(g0,g3)
    c: InternalAlignment(g1,g3)
    c: InternalAlignment(g2,g3)
    c: InternalAlignment(g4,g3)
    c: InternalAlignment(g5,g3)
    c: Block(g3)
    c: Weight(g6) = 1
    c: Equal(g6,g7)
    c: Equal(g6,g8)
    c: InternalAlignment(g6,g9)
    c: InternalAlignment(g7,g9)
    c: InternalAlignment(g8,g9)
    c: InternalAlignment(g10,g9)
    c: InternalAlignment(g11,g9)
    c: Block(g9)
    c: Coincident(g12,g9)
    c: Coincident(g12,g3)
    c: Vertical(g12)
    c: Coincident(g13,g9)
    c: Horizontal(g13)
    c: Distance(g13) = 4.8
    c: Coincident(g14,g3)
    c: Vertical(g14)
    c: Coincident(g15,g13)
    c: Vertical(g15)
    c: Tangent(g15,g1)
    c: Distance(g14) = 2
    c: Coincident(g16,g14)
    c: Horizontal(g16)
    c: Coincident(g15,g16)
FEATURE [Part::Feature] Face050
  shape: bbox 4.8 x 25.5 x 2e-07 mm, 1 faces, 0 solids (baked)
FEATURE [Part::Revolution] Revolve054  label="moreFrontCaseScrewPost001"
  Angle = 360
  Axis = (0,1,0)
  Base = (0,0,0)
  FaceMakerClass = Part::FaceMakerBullseye
  Placement = pos=(102.5,4.5,3.5) rot=(0,0,1;0rad)
  Solid = false
  Source = -> Face050
  Symmetric = false
FEATURE [Part::Feature] Face051
  shape: bbox 4.8 x 25.5 x 2e-07 mm, 1 faces, 0 solids (baked)
FEATURE [Part::Revolution] Revolve055  label="moreFrontCaseScrewPost002"
  Angle = 360
  Axis = (0,1,0)
  Base = (0,0,0)
  FaceMakerClass = Part::FaceMakerBullseye
  Placement = pos=(102.5,4.5,68.5) rot=(0,0,1;0rad)
  Solid = false
  Source = -> Face051
  Symmetric = false
FEATURE [Sketcher::SketchObject] Sketch027
  FullyConstrained = true
  sketch-geometry (10):
    g0: LineSegment StartX=-1.6 StartY=4.7 StartZ=0 EndX=-1.6 EndY=1.7 EndZ=0
    g1: LineSegment StartX=-3.5 StartY=4.7 StartZ=0 EndX=-1.6 EndY=4.7 EndZ=0
    g2: LineSegment StartX=-1.6 StartY=1.7 StartZ=0 EndX=-1.6 EndY=1.5 EndZ=0
    g3: LineSegment StartX=-1.6 StartY=1.5 StartZ=0 EndX=-5.2 EndY=1.5 EndZ=0
    g4: Circle CenterX=-3.5 CenterY=4.7 CenterZ=0 NormalX=0 NormalY=0 NormalZ=1 AngleXU=0 Radius=1
    g5: Circle CenterX=-3.59627 CenterY=2.99743 CenterZ=0 NormalX=0 NormalY=0 NormalZ=1 AngleXU=0 Radius=1
    g6: Circle CenterX=-5.2 CenterY=1.5 CenterZ=0 NormalX=0 NormalY=0 NormalZ=1 AngleXU=0 Radius=1
    g7: BSplineCurve PolesCount=3 KnotsCount=2 Degree=2 IsPeriodic=0
    g8: GeomPoint X=-3.5 Y=4.7 Z=0
    g9: GeomPoint X=-5.2 Y=1.5 Z=0
  constraints (23):
    c: Vertical(g0)
    c: Distance(g0) = 3
    c: Coincident(g1,g0)
    c: Horizontal(g1)
    c: Block(g0)
    c: Block(g1)
    c: Coincident(g2,g0)
    c: Vertical(g2)
    c: Distance(g2) = 0.2
    c: Coincident(g3,g2)
    c: Horizontal(g3)
    c: Block(g3)
    c: Coincident(g7,g1)
    c: Weight(g4) = 1
    c: Equal(g4,g5)
    c: Equal(g4,g6)
    c: Coincident(g7,g3)
    c: InternalAlignment(g4,g7)
    c: InternalAlignment(g5,g7)
    c: InternalAlignment(g6,g7)
    c: InternalAlignment(g8,g7)
    c: InternalAlignment(g9,g7)
    c: Block(g7)
FEATURE [Sketcher::SketchObject] Sketch028
  FullyConstrained = true
  sketch-geometry (18):
    g0: LineSegment StartX=0 StartY=3e-16 StartZ=0 EndX=0 EndY=1.7 EndZ=0
    g1: LineSegment StartX=-3.5 StartY=0 StartZ=0 EndX=-3.5 EndY=0.9 EndZ=0
    g2: Circle CenterX=-2.7 CenterY=1.7 CenterZ=0 NormalX=0 NormalY=0 NormalZ=1 AngleXU=0 Radius=1
    g3: Circle CenterX=-3.5 CenterY=1.7 CenterZ=0 NormalX=0 NormalY=0 NormalZ=1 AngleXU=0 Radius=1
    g4: Circle CenterX=-3.5 CenterY=0.9 CenterZ=0 NormalX=0 NormalY=0 NormalZ=1 AngleXU=0 Radius=1
    g5: BSplineCurve PolesCount=3 KnotsCount=2 Degree=2 IsPeriodic=0
    g6: GeomPoint X=-2.7 Y=1.7 Z=0
    g7: GeomPoint X=-3.5 Y=0.9 Z=0
    g8: LineSegment StartX=-3.5 StartY=0 StartZ=0 EndX=-3.5 EndY=-7 EndZ=0
    g9: LineSegment StartX=0 StartY=3e-16 StartZ=0 EndX=0 EndY=-7 EndZ=0
    g10: LineSegment StartX=-3.5 StartY=-7 StartZ=0 EndX=0 EndY=-7 EndZ=0
    g11: LineSegment StartX=-2.7 StartY=1.7 StartZ=0 EndX=-1.6 EndY=1.7 EndZ=0
    g12: LineSegment StartX=0 StartY=1.7 StartZ=0 EndX=0 EndY=4.5 EndZ=0
    g13: LineSegment StartX=0 StartY=4.5 StartZ=0 EndX=0 EndY=10.8 EndZ=0
    g14: LineSegment StartX=0 StartY=10.8 StartZ=0 EndX=-2 EndY=10.8 EndZ=0
    g15: LineSegment StartX=-1.6 StartY=4.7 StartZ=0 EndX=-1.6 EndY=1.7 EndZ=0
    g16: LineSegment StartX=-1.6 StartY=4.7 StartZ=0 EndX=-2 EndY=4.7 EndZ=0
    g17: LineSegment StartX=-2 StartY=4.7 StartZ=0 EndX=-2 EndY=10.8 EndZ=0
  constraints (44):
    c: Vertical(g0)
    c: Vertical(g1)
    c: Distance(g1) = 0.9
    c: Block(g0)
    c: Distance(g0) = 1.7
    c: Weight(g2) = 1
    c: Equal(g2,g3)
    c: Equal(g2,g4)
    c: Coincident(g5,g1)
    c: InternalAlignment(g2,g5)
    c: InternalAlignment(g3,g5)
    c: InternalAlignment(g4,g5)
    c: InternalAlignment(g6,g5)
    c: InternalAlignment(g7,g5)
    c: Block(g5)
    c: Coincident(g8,g1)
    c: Vertical(g8)
    c: Distance(g8) = 7
    c: Vertical(g9)
    c: Equal(g8,g9) = 7
    c: Coincident(g9,g0)
    c: Coincident(g10,g8)
    c: Coincident(g10,g9)
    c: Horizontal(g10)
    c: Coincident(g11,g5)
    c: Horizontal(g11)
    c: Coincident(g12,g0)
    c: Vertical(g12)
    c: Distance(g12) = 2.8
    c: Coincident(g13,g12)
    c: Vertical(g13)
    c: Distance(g13) = 6.3
    c: Coincident(g14,g13)
    c: Horizontal(g14)
    c: Distance(g14) = 2
    c: Vertical(g15)
    c: Distance(g15) = 3
    c: Block(g11)
    c: Coincident(g15,g11)
    c: Coincident(g16,g15)
    c: Horizontal(g16)
    c: Coincident(g17,g16)
    c: Coincident(g17,g14)
    c: Vertical(g17)
FEATURE [Part::Revolution] Revolve040  label="backCaseScrewRetainer001"
  Angle = 360
  Axis = (0,1,0)
  Base = (0,0,0)
  FaceMakerClass = Part::FaceMakerBullseye
  Placement = pos=(12.5,3,10) rot=(0,0,1;0rad)
  Solid = false
  Source = -> Face036
  Symmetric = false
FEATURE [Part::Feature] Face055
  shape: bbox 3.5 x 30.2 x 2e-07 mm, 1 faces, 0 solids (baked)
FEATURE [Part::Revolution] Revolve059  label="backCaseScrewPost"
  Angle = 360
  Axis = (0,1,0)
  Base = (0,0,0)
  FaceMakerClass = Part::FaceMakerBullseye
  Placement = pos=(12.5,4.5,10) rot=(0,0,1;0rad)
  Solid = false
  Source = -> Face055
  Symmetric = false
FEATURE [Part::Feature] Face056
  shape: bbox 3.5 x 30.2 x 2e-07 mm, 1 faces, 0 solids (baked)
FEATURE [Part::Revolution] Revolve060  label="backCaseScrewPost001"
  Angle = 360
  Axis = (0,1,0)
  Base = (0,0,0)
  FaceMakerClass = Part::FaceMakerBullseye
  Placement = pos=(12.5,4.5,62) rot=(0,0,1;0rad)
  Solid = false
  Source = -> Face056
  Symmetric = false
FEATURE [Part::Feature] Face057
  shape: bbox 3.5 x 17.8 x 2e-07 mm, 1 faces, 0 solids (baked)
FEATURE [Part::Revolution] Revolve061  label="removeToCreateScrewAndThreadedInsertHole"
  Angle = 360
  Axis = (0,1,0)
  Base = (0,0,0)
  FaceMakerClass = Part::FaceMakerBullseye
  Placement = pos=(12.5,0,10) rot=(0,0,1;0rad)
  Solid = false
  Source = -> Face057
  Symmetric = false
FEATURE [Part::Feature] Face058
  shape: bbox 3.5 x 17.8 x 2e-07 mm, 1 faces, 0 solids (baked)
FEATURE [Part::Revolution] Revolve062  label="removeToCreateScrewAndThreadedInsertHole001"
  Angle = 360
  Axis = (0,1,0)
  Base = (0,0,0)
  FaceMakerClass = Part::FaceMakerBullseye
  Placement = pos=(12.5,0,62) rot=(0,0,1;0rad)
  Solid = false
  Source = -> Face058
  Symmetric = false
FEATURE [Part::Feature] Face059
  shape: bbox 3.5 x 17.8 x 2e-07 mm, 1 faces, 0 solids (baked)
FEATURE [Part::Revolution] Revolve063  label="removeToCreateScrewAndThreadedInsertHole002"
  Angle = 360
  Axis = (0,1,0)
  Base = (0,0,0)
  FaceMakerClass = Part::FaceMakerBullseye
  Placement = pos=(89.5,0,68.5) rot=(0,0,1;0rad)
  Solid = false
  Source = -> Face059
  Symmetric = false
FEATURE [Part::Feature] Face060
  shape: bbox 3.5 x 17.8 x 2e-07 mm, 1 faces, 0 solids (baked)
FEATURE [Part::Revolution] Revolve064  label="removeToCreateScrewAndThreadedInsertHole003"
  Angle = 360
  Axis = (0,1,0)
  Base = (0,0,0)
  FaceMakerClass = Part::FaceMakerBullseye
  Placement = pos=(89.5,0,3.5) rot=(0,0,1;0rad)
  Solid = false
  Source = -> Face060
  Symmetric = false
FEATURE [Part::Feature] Face061
  shape: bbox 3.5 x 17.8 x 2e-07 mm, 1 faces, 0 solids (baked)
FEATURE [Part::Revolution] Revolve065  label="removeToCreateScrewAndThreadedInsertHole004"
  Angle = 360
  Axis = (0,1,0)
  Base = (0,0,0)
  FaceMakerClass = Part::FaceMakerBullseye
  Placement = pos=(102.5,4.7,3.5) rot=(0,0,1;0rad)
  Solid = false
  Source = -> Face061
  Symmetric = false
FEATURE [Part::Feature] Face062
  shape: bbox 3.5 x 17.8 x 2e-07 mm, 1 faces, 0 solids (baked)
FEATURE [Part::Revolution] Revolve066  label="removeToCreateScrewAndThreadedInsertHole005"
  Angle = 360
  Axis = (0,1,0)
  Base = (0,0,0)
  FaceMakerClass = Part::FaceMakerBullseye
  Placement = pos=(102.5,4.7,68.5) rot=(0,0,1;0rad)
  Solid = false
  Source = -> Face062
  Symmetric = false
FEATURE [Part::MultiFuse] Fusion047  label="makeHoles"
  Shapes = -> [Revolve066,Revolve065,Revolve064,Revolve063,Revolve062,Revolve061]
FEATURE [Part::Feature] Face063
  shape: bbox 3.6 x 3.2 x 2e-07 mm, 1 faces, 0 solids (baked)
FEATURE [Part::Revolution] Revolve067  label="moreFrontCaseScrewRetainer002"
  Angle = 360
  Axis = (0,1,0)
  Base = (0,0,0)
  FaceMakerClass = Part::FaceMakerBullseye
  Placement = pos=(102.5,4.5,68.5) rot=(0,0,1;0rad)
  Solid = false
  Source = -> Face063
  Symmetric = false
FEATURE [Part::Feature] Face064
  shape: bbox 3.6 x 3.2 x 2e-07 mm, 1 faces, 0 solids (baked)
FEATURE [Part::Revolution] Revolve068  label="moreFrontCaseScrewRetainer003"
  Angle = 360
  Axis = (0,1,0)
  Base = (0,0,0)
  FaceMakerClass = Part::FaceMakerBullseye
  Placement = pos=(102.5,4.5,3.5) rot=(0,0,1;0rad)
  Solid = false
  Source = -> Face064
  Symmetric = false
FEATURE [Part::Feature] Face065
  shape: bbox 3.5 x 17.8 x 2e-07 mm, 1 faces, 0 solids (baked)
FEATURE [Part::Revolution] Revolve069  label="removeToCreateScrewAndThreadedInsertHole006"
  Angle = 360
  Axis = (0,1,0)
  Base = (0,0,0)
  FaceMakerClass = Part::FaceMakerBullseye
  Placement = pos=(12.5,0,10) rot=(0,0,1;0rad)
  Solid = false
  Source = -> Face065
  Symmetric = false
FEATURE [Part::Feature] Face066
  shape: bbox 3.5 x 17.8 x 2e-07 mm, 1 faces, 0 solids (baked)
FEATURE [Part::Revolution] Revolve070  label="removeToCreateScrewAndThreadedInsertHole007"
  Angle = 360
  Axis = (0,1,0)
  Base = (0,0,0)
  FaceMakerClass = Part::FaceMakerBullseye
  Placement = pos=(12.5,0,62) rot=(0,0,1;0rad)
  Solid = false
  Source = -> Face066
  Symmetric = false
FEATURE [Part::Feature] Face067
  shape: bbox 3.5 x 17.8 x 2e-07 mm, 1 faces, 0 solids (baked)
FEATURE [Part::Revolution] Revolve071  label="removeToCreateScrewAndThreadedInsertHole008"
  Angle = 360
  Axis = (0,1,0)
  Base = (0,0,0)
  FaceMakerClass = Part::FaceMakerBullseye
  Placement = pos=(89.5,0,68.5) rot=(0,0,1;0rad)
  Solid = false
  Source = -> Face067
  Symmetric = false
FEATURE [Part::Feature] Face068
  shape: bbox 3.5 x 17.8 x 2e-07 mm, 1 faces, 0 solids (baked)
FEATURE [Part::Revolution] Revolve072  label="removeToCreateScrewAndThreadedInsertHole009"
  Angle = 360
  Axis = (0,1,0)
  Base = (0,0,0)
  FaceMakerClass = Part::FaceMakerBullseye
  Placement = pos=(89.5,0,3.5) rot=(0,0,1;0rad)
  Solid = false
  Source = -> Face068
  Symmetric = false
FEATURE [Part::Feature] Face069
  shape: bbox 3.5 x 17.8 x 2e-07 mm, 1 faces, 0 solids (baked)
FEATURE [Part::Feature] Face070
  shape: bbox 3.5 x 17.8 x 2e-07 mm, 1 faces, 0 solids (baked)
FEATURE [Part::Revolution] Revolve073  label="removeToCreateScrewAndThreadedInsertHole010"
  Angle = 360
  Axis = (0,1,0)
  Base = (0,0,0)
  FaceMakerClass = Part::FaceMakerBullseye
  Placement = pos=(102.5,4.7,3.5) rot=(0,0,1;0rad)
  Solid = false
  Source = -> Face069
  Symmetric = false
FEATURE [Part::Revolution] Revolve074  label="removeToCreateScrewAndThreadedInsertHole011"
  Angle = 360
  Axis = (0,1,0)
  Base = (0,0,0)
  FaceMakerClass = Part::FaceMakerBullseye
  Placement = pos=(102.5,4.7,68.5) rot=(0,0,1;0rad)
  Solid = false
  Source = -> Face070
  Symmetric = false
FEATURE [Part::MultiFuse] Fusion048  label="makeHoles001"
  Shapes = -> [Revolve074,Revolve073,Revolve072,Revolve071,Revolve070,Revolve069]
FEATURE [Part::MultiFuse] Fusion049  label="caseScrewRetainers"
  Shapes = -> [Revolve067,Revolve068,Revolve048,Revolve047,Revolve039,Revolve040]
FEATURE [Part::Cut] Cut015  label="caseScrewRetainers001"
  Base = -> Fusion049
  Tool = -> Fusion048
FEATURE [Part::MultiFuse] Fusion050  label="casePillars"
  Shapes = -> [Revolve055,Revolve054,Revolve043,Revolve046,Revolve059,Revolve060]
FEATURE [Part::Feature] Face071 .. Face076  x6 (patterned run collapsed; names and placements below)
  shape: bbox 3.5 x 17.8 x 2e-07 mm, 1 faces, 0 solids (baked)
FEATURE [Part::Revolution] Revolve075  label="removeToCreateScrewAndThreadedInsertHole012"
  Angle = 360
  Axis = (0,1,0)
  Base = (0,0,0)
  FaceMakerClass = Part::FaceMakerBullseye
  Placement = pos=(12.5,0,10) rot=(0,0,1;0rad)
  Solid = false
  Source = -> Face071
  Symmetric = false
FEATURE [Part::Revolution] Revolve076  label="removeToCreateScrewAndThreadedInsertHole013"
  Angle = 360
  Axis = (0,1,0)
  Base = (0,0,0)
  FaceMakerClass = Part::FaceMakerBullseye
  Placement = pos=(12.5,0,62) rot=(0,0,1;0rad)
  Solid = false
  Source = -> Face072
  Symmetric = false
FEATURE [Part::Revolution] Revolve077  label="removeToCreateScrewAndThreadedInsertHole014"
  Angle = 360
  Axis = (0,1,0)
  Base = (0,0,0)
  FaceMakerClass = Part::FaceMakerBullseye
  Placement = pos=(89.5,0,68.5) rot=(0,0,1;0rad)
  Solid = false
  Source = -> Face073
  Symmetric = false
FEATURE [Part::Revolution] Revolve078  label="removeToCreateScrewAndThreadedInsertHole015"
  Angle = 360
  Axis = (0,1,0)
  Base = (0,0,0)
  FaceMakerClass = Part::FaceMakerBullseye
  Placement = pos=(89.5,0,3.5) rot=(0,0,1;0rad)
  Solid = false
  Source = -> Face074
  Symmetric = false
FEATURE [Part::Revolution] Revolve079  label="removeToCreateScrewAndThreadedInsertHole016"
  Angle = 360
  Axis = (0,1,0)
  Base = (0,0,0)
  FaceMakerClass = Part::FaceMakerBullseye
  Placement = pos=(102.5,4.7,3.5) rot=(0,0,1;0rad)
  Solid = false
  Source = -> Face075
  Symmetric = false
FEATURE [Part::Revolution] Revolve080  label="removeToCreateScrewAndThreadedInsertHole017"
  Angle = 360
  Axis = (0,1,0)
  Base = (0,0,0)
  FaceMakerClass = Part::FaceMakerBullseye
  Placement = pos=(102.5,4.7,68.5) rot=(0,0,1;0rad)
  Solid = false
  Source = -> Face076
  Symmetric = false
FEATURE [Part::MultiFuse] Fusion051  label="makeHoles002"
  Shapes = -> [Revolve080,Revolve079,Revolve078,Revolve077,Revolve076,Revolve075]
FEATURE [Part::Cut] Cut016  label="caesPillars"
  Base = -> Fusion050
  Tool = -> Fusion051
FEATURE [Part::Revolution] Revolve009  label="plugHousing016"
  Angle = 360
  Axis = (0,1,0)
  Base = (0,0,0)
  FaceMakerClass = Part::FaceMakerBullseye
  Placement = pos=(0,0,36.15) rot=(0,0,1;0rad)
  Solid = false
  Source = -> Face012
  Symmetric = false
FEATURE [Part::MultiFuse] Fusion014  label="plugHousing023"
  Placement = pos=(0,0,0) rot=(0,0,1;1.5708rad)
  Shapes = -> [Revolve011,Revolve009]
FEATURE [Part::Revolution] Revolve010  label="plugHousing017"
  Angle = 360
  Axis = (0,1,0)
  Base = (0,0,0)
  FaceMakerClass = Part::FaceMakerBullseye
  Placement = pos=(0,0,36.15) rot=(0,0,1;0rad)
  Solid = false
  Source = -> Face014
  Symmetric = false
FEATURE [Part::MultiFuse] Fusion015  label="plugHousing024"
  Placement = pos=(0,0,0) rot=(0,0,1;1.5708rad)
  Shapes = -> [Revolve010,Revolve015]
FEATURE [Part::Revolution] Revolve014  label="plugHousing026"
  Angle = 360
  Axis = (0,1,0)
  Base = (0,0,0)
  FaceMakerClass = Part::FaceMakerBullseye
  Placement = pos=(0,0,36.15) rot=(0,0,1;0rad)
  Solid = false
  Source = -> Face011
  Symmetric = false
FEATURE [Part::Revolution] Revolve013  label="plugHousing025"
  Angle = 360
  Axis = (0,1,0)
  Base = (0,0,0)
  FaceMakerClass = Part::FaceMakerBullseye
  Placement = pos=(0,0,36.15) rot=(0,0,1;0rad)
  Solid = false
  Source = -> Face015
  Symmetric = false
FEATURE [Part::MultiFuse] Fusion016  label="plugHousing028"
  Placement = pos=(0,19,0) rot=(0,0,1;3.14159rad)
  Shapes = -> [Fusion014,Fusion013]
FEATURE [Part::MultiFuse] Fusion011  label="plugHousing018"
  Placement = pos=(0,0,0) rot=(0,0,1;1.5708rad)
  Shapes = -> [Revolve014,Revolve013]
FEATURE [Part::MultiFuse] Fusion012  label="plugHousing019"
  Placement = pos=(0,19,0) rot=(0,0,1;3.14159rad)
  Shapes = -> [Fusion011,Fusion015]
FEATURE [Part::MultiFuse] Fusion017  label="plugHousing029"
  Placement = pos=(122.621,0,-0.15) rot=(0,0,1;0rad)
  Shapes = -> [Fusion016,Fusion012]
FEATURE [Part::MultiFuse] Fusion052  label="casePillarRetainers"
  Shapes = -> [Extrude012,Extrude013,Extrude014,Extrude015,Extrude016,Extrude017,Extrude018,Extrude019,Box011,Box012]
FEATURE [Part::Feature] Face077
  shape: bbox 3.5 x 17.8 x 2e-07 mm, 1 faces, 0 solids (baked)
FEATURE [Part::Revolution] Revolve081  label="removeToCreateScrewAndThreadedInsertHole018"
  Angle = 360
  Axis = (0,1,0)
  Base = (0,0,0)
  FaceMakerClass = Part::FaceMakerBullseye
  Placement = pos=(62.3,30.3,19.7) rot=(0,0,1;0rad)
  Solid = false
  Source = -> Face077
  Symmetric = false
FEATURE [Part::Feature] Face078
  shape: bbox 3.5 x 17.8 x 2e-07 mm, 1 faces, 0 solids (baked)
FEATURE [Part::Revolution] Revolve082  label="removeToCreateScrewAndThreadedInsertHole019"
  Angle = 360
  Axis = (0,1,0)
  Base = (0,0,0)
  FaceMakerClass = Part::FaceMakerBullseye
  Placement = pos=(62.3,30.3,51.7) rot=(0,0,1;0rad)
  Solid = false
  Source = -> Face078
  Symmetric = false
FEATURE [Part::Feature] Face079
  shape: bbox 3.5 x 17.8 x 2e-07 mm, 1 faces, 0 solids (baked)
FEATURE [Part::Revolution] Revolve083  label="removeToCreateScrewAndThreadedInsertHole020"
  Angle = 360
  Axis = (0,1,0)
  Base = (0,0,0)
  FaceMakerClass = Part::FaceMakerBullseye
  Placement = pos=(30.3,30.3,19.7) rot=(0,0,1;0rad)
  Solid = false
  Source = -> Face079
  Symmetric = false
FEATURE [Part::Feature] Face080
  shape: bbox 3.5 x 17.8 x 2e-07 mm, 1 faces, 0 solids (baked)
FEATURE [Part::Revolution] Revolve084  label="removeToCreateScrewAndThreadedInsertHole021"
  Angle = 360
  Axis = (0,1,0)
  Base = (0,0,0)
  FaceMakerClass = Part::FaceMakerBullseye
  Placement = pos=(30.3,30.3,51.7) rot=(0,0,1;0rad)
  Solid = false
  Source = -> Face080
  Symmetric = false
FEATURE [Part::MultiFuse] Fusion053  label="createThreadedInsertHolesForFan"
  Shapes = -> [Revolve081,Revolve082,Revolve083,Revolve084]
FEATURE [Part::Cut] Cut017  label="fanScrewHousing001"
  Base = -> Fusion046
  Tool = -> Fusion053
FEATURE [Part::Feature] Face081
  shape: bbox 3.5 x 17.8 x 2e-07 mm, 1 faces, 0 solids (baked)
FEATURE [Part::Revolution] Revolve085  label="removeToCreateScrewAndThreadedInsertHole022"
  Angle = 360
  Axis = (0,1,0)
  Base = (0,0,0)
  FaceMakerClass = Part::FaceMakerBullseye
  Placement = pos=(62.3,30.3,19.7) rot=(0,0,1;0rad)
  Solid = false
  Source = -> Face081
  Symmetric = false
FEATURE [Part::Feature] Face082
  shape: bbox 3.5 x 17.8 x 2e-07 mm, 1 faces, 0 solids (baked)
FEATURE [Part::Revolution] Revolve086  label="removeToCreateScrewAndThreadedInsertHole023"
  Angle = 360
  Axis = (0,1,0)
  Base = (0,0,0)
  FaceMakerClass = Part::FaceMakerBullseye
  Placement = pos=(62.3,30.3,51.7) rot=(0,0,1;0rad)
  Solid = false
  Source = -> Face082
  Symmetric = false
FEATURE [Part::Feature] Face083
  shape: bbox 3.5 x 17.8 x 2e-07 mm, 1 faces, 0 solids (baked)
FEATURE [Part::Revolution] Revolve087  label="removeToCreateScrewAndThreadedInsertHole024"
  Angle = 360
  Axis = (0,1,0)
  Base = (0,0,0)
  FaceMakerClass = Part::FaceMakerBullseye
  Placement = pos=(30.3,30.3,19.7) rot=(0,0,1;0rad)
  Solid = false
  Source = -> Face083
  Symmetric = false
FEATURE [Part::Feature] Face084
  shape: bbox 3.5 x 17.8 x 2e-07 mm, 1 faces, 0 solids (baked)
FEATURE [Part::Revolution] Revolve088  label="removeToCreateScrewAndThreadedInsertHole025"
  Angle = 360
  Axis = (0,1,0)
  Base = (0,0,0)
  FaceMakerClass = Part::FaceMakerBullseye
  Placement = pos=(30.3,30.3,51.7) rot=(0,0,1;0rad)
  Solid = false
  Source = -> Face084
  Symmetric = false
FEATURE [Part::MultiFuse] Fusion054  label="createThreadedInsertHolesForFan001"
  Shapes = -> [Revolve085,Revolve086,Revolve087,Revolve088]
FEATURE [Part::Cut] Cut018  label="top007"
  Base = -> Fusion040
  Tool = -> Fusion054
FEATURE [Sketcher::SketchObject] Sketch029
  FullyConstrained = false
  Placement = pos=(0,0,0) rot=(1,0,0;1.5708rad)
  sketch-geometry (24):
    g0: ArcOfCircle CenterX=-4 CenterY=-10.5 CenterZ=0 NormalX=0 NormalY=0 NormalZ=1 AngleXU=0 Radius=1.5 StartAngle=6e-16 EndAngle=3.14159
    g1: ArcOfCircle CenterX=-34.2 CenterY=-10.5 CenterZ=0 NormalX=0 NormalY=0 NormalZ=1 AngleXU=0 Radius=1.5 StartAngle=0 EndAngle=3.14159
    g2: ArcOfCircle CenterX=-34.2 CenterY=-27.7 CenterZ=0 NormalX=0 NormalY=0 NormalZ=1 AngleXU=0 Radius=1.5 StartAngle=3.14159 EndAngle=6.28319
    g3: ArcOfCircle CenterX=-4 CenterY=-27.7 CenterZ=0 NormalX=0 NormalY=0 NormalZ=1 AngleXU=0 Radius=1.5 StartAngle=3.1416 EndAngle=6.28319
    g4: ArcOfCircle CenterX=-10 CenterY=-4.3 CenterZ=0 NormalX=0 NormalY=0 NormalZ=1 AngleXU=0 Radius=1.5 StartAngle=2e-16 EndAngle=3.14159
    g5: ArcOfCircle CenterX=-16.1 CenterY=-1.8 CenterZ=0 NormalX=0 NormalY=0 NormalZ=1 AngleXU=0 Radius=1.5 StartAngle=5e-16 EndAngle=3.14159
    g6: ArcOfCircle CenterX=-22.1 CenterY=-1.8 CenterZ=0 NormalX=0 NormalY=0 NormalZ=1 AngleXU=0 Radius=1.5 StartAngle=5e-16 EndAngle=3.14159
    g7: ArcOfCircle CenterX=-28.2 CenterY=-4.3 CenterZ=0 NormalX=0 NormalY=0 NormalZ=1 AngleXU=0 Radius=1.5 StartAngle=2e-16 EndAngle=3.14159
    g8: ArcOfCircle CenterX=-10 CenterY=-33.9 CenterZ=0 NormalX=0 NormalY=0 NormalZ=1 AngleXU=0 Radius=1.5 StartAngle=3.14159 EndAngle=6.28319
    g9: ArcOfCircle CenterX=-16.1 CenterY=-36.4 CenterZ=0 NormalX=0 NormalY=0 NormalZ=1 AngleXU=0 Radius=1.5 StartAngle=3.14159 EndAngle=6.28319
    g10: ArcOfCircle CenterX=-22.1 CenterY=-36.4 CenterZ=0 NormalX=0 NormalY=0 NormalZ=1 AngleXU=0 Radius=1.5 StartAngle=3.14159 EndAngle=6.28319
    g11: ArcOfCircle CenterX=-28.2 CenterY=-33.9 CenterZ=0 NormalX=0 NormalY=0 NormalZ=1 AngleXU=0 Radius=1.5 StartAngle=3.14159 EndAngle=6.28319
    g12: LineSegment StartX=-35.7 StartY=-10.5 StartZ=0 EndX=-35.7 EndY=-27.7 EndZ=0
    g13: LineSegment StartX=-32.7 StartY=-10.5 StartZ=0 EndX=-32.7 EndY=-27.7 EndZ=0
    g14: LineSegment StartX=-29.7 StartY=-33.9 StartZ=0 EndX=-29.7 EndY=-4.3 EndZ=0
    g15: LineSegment StartX=-26.7 StartY=-33.9 StartZ=0 EndX=-26.7 EndY=-4.3 EndZ=0
    g16: LineSegment StartX=-2.5 StartY=-10.5 StartZ=0 EndX=-2.5 EndY=-27.7 EndZ=0
    g17: LineSegment StartX=-8.5 StartY=-4.3 StartZ=0 EndX=-8.5 EndY=-33.9 EndZ=0
    g18: LineSegment StartX=-5.5 StartY=-10.5 StartZ=0 EndX=-5.5 EndY=-27.7 EndZ=0
    g19: LineSegment StartX=-11.5 StartY=-4.3 StartZ=0 EndX=-11.5 EndY=-33.9 EndZ=0
    g20: LineSegment StartX=-14.6 StartY=-1.8 StartZ=0 EndX=-14.6 EndY=-36.4 EndZ=0
    g21: LineSegment StartX=-17.6 StartY=-1.8 StartZ=0 EndX=-17.6 EndY=-36.4 EndZ=0
    g22: LineSegment StartX=-20.6 StartY=-36.4 StartZ=0 EndX=-20.6 EndY=-1.8 EndZ=0
    g23: LineSegment StartX=-23.6 StartY=-1.8 StartZ=0 EndX=-23.6 EndY=-36.4 EndZ=0
  constraints (48):
    c: Block(g0)
    c: Block(g1)
    c: Block(g2)
    c: Block(g3)
    c: Block(g4)
    c: Block(g5)
    c: Block(g6)
    c: Block(g7)
    c: Block(g8)
    c: Block(g9)
    c: Block(g10)
    c: Block(g11)
    c: Coincident(g12,g1)
    c: Coincident(g12,g2)
    c: Vertical(g12)
    c: Coincident(g13,g1)
    c: Coincident(g13,g2)
    c: Vertical(g13)
    c: Coincident(g14,g11)
    c: Coincident(g14,g7)
    c: Vertical(g14)
    c: Coincident(g15,g11)
    c: Coincident(g15,g7)
    c: Vertical(g15)
    c: Coincident(g16,g0)
    c: Coincident(g16,g3)
    c: Vertical(g16)
    c: Coincident(g17,g4)
    c: Coincident(g17,g8)
    c: Vertical(g17)
    c: Coincident(g18,g0)
    c: Coincident(g18,g3)
    c: Vertical(g18)
    c: Coincident(g19,g4)
    c: Coincident(g19,g8)
    c: Vertical(g19)
    c: Coincident(g20,g5)
    c: Coincident(g20,g9)
    c: Vertical(g20)
    c: Coincident(g21,g5)
    c: Coincident(g21,g9)
    c: Vertical(g21)
    c: Coincident(g22,g10)
    c: Coincident(g22,g6)
    c: Vertical(g22)
    c: Coincident(g23,g6)
    c: Coincident(g23,g10)
    c: Vertical(g23)
FEATURE [Part::Extrusion] Extrude020  label="removeToCreateFanGrillHoles"
  Base = -> Sketch029
  Dir = (0,-1,6e-16)
  DirMode = 2
  FaceMakerClass = Part::FaceMakerBullseye
  LengthFwd = 10
  LengthRev = 0
  Placement = pos=(65.4,44,54.82) rot=(0,0,1;0rad)
  Solid = true
  Symmetric = false
FEATURE [Part::MultiFuse] Fusion055  label="top008"
  Shapes = -> [Cut017,Cut018]
FEATURE [Part::Cut] Cut019  label="top009"
  Base = -> Fusion055
  Tool = -> Extrude020
FEATURE [App::MeasureDistance] Distance003  label="Distance: 71.95 mm"
  Distance = 71.9513
  P1 = (117,38,72)
  P2 = (117,38,0.0487319)
FEATURE [Sketcher::SketchObject] Sketch030
  FullyConstrained = true
  Placement = pos=(117,19,0) rot=(0.57735,0.57735,0.57735;2.0944rad)
  sketch-geometry (48):
    g0: LineSegment StartX=-49.19 StartY=69.25 StartZ=0 EndX=-49.19 EndY=66.25 EndZ=0
    g1: LineSegment StartX=-49.19 StartY=63.5 StartZ=0 EndX=-49.19 EndY=60.5 EndZ=0
    g2: LineSegment StartX=-49.19 StartY=57.75 StartZ=0 EndX=-49.19 EndY=54.75 EndZ=0
    g3: LineSegment StartX=-49.19 StartY=52 StartZ=0 EndX=-49.19 EndY=49 EndZ=0
    g4: LineSegment StartX=-49.19 StartY=46.25 StartZ=0 EndX=-49.19 EndY=43.25 EndZ=0
    g5: LineSegment StartX=-49.19 StartY=40.5 StartZ=0 EndX=-49.19 EndY=37.5 EndZ=0
    g6: LineSegment StartX=-49.19 StartY=34.5 StartZ=0 EndX=-49.19 EndY=31.5 EndZ=0
    g7: LineSegment StartX=-49.19 StartY=28.75 StartZ=0 EndX=-49.19 EndY=25.75 EndZ=0
    g8: LineSegment StartX=-49.19 StartY=23 StartZ=0 EndX=-49.19 EndY=20 EndZ=0
    g9: LineSegment StartX=-49.19 StartY=17.25 StartZ=0 EndX=-49.19 EndY=14.25 EndZ=0
    g10: LineSegment StartX=-49.19 StartY=11.5 StartZ=0 EndX=-49.19 EndY=8.5 EndZ=0
    g11: LineSegment StartX=-49.19 StartY=5.75 StartZ=0 EndX=-49.19 EndY=2.75 EndZ=0
    g12: ArcOfCircle CenterX=-1.5 CenterY=67.75 CenterZ=0 NormalX=0 NormalY=0 NormalZ=1 AngleXU=0 Radius=1.5 StartAngle=4.71239 EndAngle=7.85398
    g13: ArcOfCircle CenterX=-1.5 CenterY=62 CenterZ=0 NormalX=0 NormalY=0 NormalZ=1 AngleXU=0 Radius=1.5 StartAngle=4.71239 EndAngle=7.85398
    g14: ArcOfCircle CenterX=-1.5 CenterY=56.25 CenterZ=0 NormalX=0 NormalY=0 NormalZ=1 AngleXU=0 Radius=1.5 StartAngle=4.71239 EndAngle=7.85398
    g15: ArcOfCircle CenterX=-11.49 CenterY=50.5 CenterZ=0 NormalX=0 NormalY=0 NormalZ=1 AngleXU=0 Radius=1.5 StartAngle=4.71239 EndAngle=7.85398
    g16: ArcOfCircle CenterX=-16.28 CenterY=44.75 CenterZ=0 NormalX=0 NormalY=0 NormalZ=1 AngleXU=0 Radius=1.5 StartAngle=4.71239 EndAngle=7.85398
    g17: ArcOfCircle CenterX=-18.2337 CenterY=39 CenterZ=0 NormalX=0 NormalY=0 NormalZ=1 AngleXU=0 Radius=1.5 StartAngle=4.71485 EndAngle=7.85398
    g18: ArcOfCircle CenterX=-16.2837 CenterY=27.25 CenterZ=0 NormalX=0 NormalY=0 NormalZ=1 AngleXU=0 Radius=1.5 StartAngle=4.71485 EndAngle=7.85398
    g19: ArcOfCircle CenterX=-18.2337 CenterY=33 CenterZ=0 NormalX=0 NormalY=0 NormalZ=1 AngleXU=0 Radius=1.5 StartAngle=4.71485 EndAngle=7.85398
    g20: ArcOfCircle CenterX=-11.49 CenterY=21.5 CenterZ=0 NormalX=0 NormalY=0 NormalZ=1 AngleXU=0 Radius=1.5 StartAngle=4.71239 EndAngle=7.85398
    g21: ArcOfCircle CenterX=-1.5 CenterY=4.25 CenterZ=0 NormalX=0 NormalY=0 NormalZ=1 AngleXU=0 Radius=1.5 StartAngle=4.71239 EndAngle=7.85398
    g22: ArcOfCircle CenterX=-1.5 CenterY=10 CenterZ=0 NormalX=0 NormalY=0 NormalZ=1 AngleXU=0 Radius=1.5 StartAngle=4.71239 EndAngle=7.85398
    g23: ArcOfCircle CenterX=-1.5 CenterY=15.75 CenterZ=0 NormalX=0 NormalY=0 NormalZ=1 AngleXU=0 Radius=1.5 StartAngle=4.71239 EndAngle=7.85398
    g24: LineSegment StartX=-49.19 StartY=69.25 StartZ=0 EndX=-1.5 EndY=69.25 EndZ=0
    g25: LineSegment StartX=-49.19 StartY=66.25 StartZ=0 EndX=-1.5 EndY=66.25 EndZ=0
    g26: LineSegment StartX=-49.19 StartY=63.5 StartZ=0 EndX=-1.5 EndY=63.5 EndZ=0
    g27: LineSegment StartX=-49.19 StartY=60.5 StartZ=0 EndX=-1.5 EndY=60.5 EndZ=0
    g28: LineSegment StartX=-49.19 StartY=57.75 StartZ=0 EndX=-1.5 EndY=57.75 EndZ=0
    g29: LineSegment StartX=-49.19 StartY=54.75 StartZ=0 EndX=-1.5 EndY=54.75 EndZ=0
    g30: LineSegment StartX=-49.19 StartY=52 StartZ=0 EndX=-11.49 EndY=52 EndZ=0
    g31: LineSegment StartX=-49.19 StartY=49 StartZ=0 EndX=-11.49 EndY=49 EndZ=0
    g32: LineSegment StartX=-49.19 StartY=46.25 StartZ=0 EndX=-16.28 EndY=46.25 EndZ=0
    g33: LineSegment StartX=-49.19 StartY=43.25 StartZ=0 EndX=-16.28 EndY=43.25 EndZ=0
    g34: LineSegment StartX=-49.19 StartY=40.5 StartZ=0 EndX=-18.2337 EndY=40.5 EndZ=0
    g35: LineSegment StartX=-49.19 StartY=37.5 StartZ=0 EndX=-18.23 EndY=37.5 EndZ=0
    g36: LineSegment StartX=-49.19 StartY=34.5 StartZ=0 EndX=-18.2337 EndY=34.5 EndZ=0
    g37: LineSegment StartX=-49.19 StartY=31.5 StartZ=0 EndX=-18.23 EndY=31.5 EndZ=0
    g38: LineSegment StartX=-49.19 StartY=28.75 StartZ=0 EndX=-16.2837 EndY=28.75 EndZ=0
    g39: LineSegment StartX=-49.19 StartY=25.75 StartZ=0 EndX=-16.28 EndY=25.75 EndZ=0
    g40: LineSegment StartX=-49.19 StartY=23 StartZ=0 EndX=-11.49 EndY=23 EndZ=0
    g41: LineSegment StartX=-49.19 StartY=20 StartZ=0 EndX=-11.49 EndY=20 EndZ=0
    g42: LineSegment StartX=-49.19 StartY=17.25 StartZ=0 EndX=-1.5 EndY=17.25 EndZ=0
    g43: LineSegment StartX=-49.19 StartY=14.25 StartZ=0 EndX=-1.5 EndY=14.25 EndZ=0
    g44: LineSegment StartX=-49.19 StartY=11.5 StartZ=0 EndX=-1.5 EndY=11.5 EndZ=0
    g45: LineSegment StartX=-49.19 StartY=8.5 StartZ=0 EndX=-1.5 EndY=8.5 EndZ=0
    g46: LineSegment StartX=-49.19 StartY=5.75 StartZ=0 EndX=-1.5 EndY=5.75 EndZ=0
    g47: LineSegment StartX=-49.19 StartY=2.75 StartZ=0 EndX=-1.5 EndY=2.75 EndZ=0
  constraints (120):
    c: Vertical(g0)
    c: Distance(g0) = 3
    c: Block(g0)
    c: Vertical(g1)
    c: Distance(g1) = 3
    c: Vertical(g2)
    c: Equal(g0,g2) = 3
    c: Block(g2)
    c: Vertical(g3)
    c: Equal(g1,g3) = 3
    c: Vertical(g4)
    c: Equal(g0,g4) = 3
    c: Block(g4)
    c: Vertical(g5)
    c: Equal(g1,g5) = 3
    c: Vertical(g6)
    c: Equal(g0,g6) = 3
    c: Block(g6)
    c: Vertical(g7)
    c: Equal(g1,g7) = 3
    c: Vertical(g8)
    c: Equal(g0,g8) = 3
    c: Block(g8)
    c: Vertical(g9)
    c: Equal(g1,g9) = 3
    c: Vertical(g10)
    c: Equal(g0,g10) = 3
    c: Block(g10)
    c: Vertical(g11)
    c: Equal(g1,g11) = 3
    c: Block(g12)
    c: Block(g13)
    c: Block(g14)
    c: Block(g15)
    c: Block(g16)
    c: Block(g17)
    c: Block(g18)
    c: Block(g19)
    c: Block(g20)
    c: Block(g21)
    c: Block(g22)
    c: Block(g23)
    c: Block(g11)
    c: Block(g9)
    c: Block(g7)
    c: Block(g5)
    c: Block(g3)
    c: Block(g1)
    c: Coincident(g24,g0)
    c: Coincident(g24,g12)
    c: Horizontal(g24)
    c: Coincident(g25,g0)
    c: Coincident(g25,g12)
    c: Horizontal(g25)
    c: Coincident(g26,g1)
    c: Coincident(g26,g13)
    c: Horizontal(g26)
    c: Coincident(g27,g1)
    c: Coincident(g27,g13)
    c: Horizontal(g27)
    c: Coincident(g28,g2)
    c: Coincident(g28,g14)
    c: Horizontal(g28)
    c: Coincident(g29,g2)
    c: Coincident(g29,g14)
    c: Horizontal(g29)
    c: Coincident(g30,g3)
    c: Coincident(g30,g15)
    c: Horizontal(g30)
    c: Coincident(g31,g3)
    c: Coincident(g31,g15)
    c: Horizontal(g31)
    c: Coincident(g32,g4)
    c: Coincident(g32,g16)
    c: Horizontal(g32)
    c: Coincident(g33,g4)
    c: Coincident(g33,g16)
    c: Horizontal(g33)
    c: Coincident(g34,g5)
    c: Coincident(g34,g17)
    c: Horizontal(g34)
    c: Coincident(g35,g5)
    c: Coincident(g35,g17)
    c: Horizontal(g35)
    c: Coincident(g36,g6)
    c: Coincident(g36,g19)
    c: Horizontal(g36)
    c: Coincident(g37,g6)
    c: Coincident(g37,g19)
    c: Horizontal(g37)
    c: Coincident(g38,g7)
    c: Coincident(g38,g18)
    c: Horizontal(g38)
    c: Coincident(g39,g7)
    c: Coincident(g39,g18)
    c: Horizontal(g39)
    c: Coincident(g40,g8)
    c: Coincident(g40,g20)
    c: Horizontal(g40)
    c: Coincident(g41,g8)
    c: Coincident(g41,g20)
    c: Horizontal(g41)
    c: Coincident(g42,g9)
    c: Coincident(g42,g23)
    c: Horizontal(g42)
    c: Coincident(g43,g9)
    c: Coincident(g43,g23)
    c: Horizontal(g43)
    c: Coincident(g44,g10)
    c: Coincident(g44,g22)
    c: Horizontal(g44)
    c: Coincident(g45,g10)
    c: Coincident(g45,g22)
    c: Horizontal(g45)
    c: Coincident(g46,g11)
    c: Coincident(g46,g21)
    c: Horizontal(g46)
    c: Coincident(g47,g11)
    c: Coincident(g47,g21)
    c: Horizontal(g47)
FEATURE [Sketcher::SketchObject] Sketch031
  FullyConstrained = true
  Placement = pos=(117,19,0) rot=(0.57735,0.57735,0.57735;2.0944rad)
  sketch-geometry (24):
    g0: ArcOfCircle CenterX=-49.19 CenterY=67.75 CenterZ=0 NormalX=0 NormalY=0 NormalZ=1 AngleXU=0 Radius=1.5 StartAngle=1.5708 EndAngle=4.71239
    g1: ArcOfCircle CenterX=-49.19 CenterY=62 CenterZ=0 NormalX=0 NormalY=0 NormalZ=1 AngleXU=0 Radius=1.5 StartAngle=1.5708 EndAngle=4.71239
    g2: ArcOfCircle CenterX=-49.19 CenterY=56.25 CenterZ=0 NormalX=0 NormalY=0 NormalZ=1 AngleXU=0 Radius=1.5 StartAngle=1.5708 EndAngle=4.71239
    g3: ArcOfCircle CenterX=-49.19 CenterY=50.5 CenterZ=0 NormalX=0 NormalY=0 NormalZ=1 AngleXU=0 Radius=1.5 StartAngle=1.5708 EndAngle=4.71239
    g4: ArcOfCircle CenterX=-49.19 CenterY=44.75 CenterZ=0 NormalX=0 NormalY=0 NormalZ=1 AngleXU=0 Radius=1.5 StartAngle=1.5708 EndAngle=4.71239
    g5: ArcOfCircle CenterX=-49.19 CenterY=39 CenterZ=0 NormalX=0 NormalY=0 NormalZ=1 AngleXU=0 Radius=1.5 StartAngle=1.5708 EndAngle=4.71239
    g6: ArcOfCircle CenterX=-49.19 CenterY=33 CenterZ=0 NormalX=0 NormalY=0 NormalZ=1 AngleXU=0 Radius=1.5 StartAngle=1.5708 EndAngle=4.71239
    g7: ArcOfCircle CenterX=-49.19 CenterY=27.25 CenterZ=0 NormalX=0 NormalY=0 NormalZ=1 AngleXU=0 Radius=1.5 StartAngle=1.5708 EndAngle=4.71239
    g8: ArcOfCircle CenterX=-49.19 CenterY=21.5 CenterZ=0 NormalX=0 NormalY=0 NormalZ=1 AngleXU=0 Radius=1.5 StartAngle=1.5708 EndAngle=4.71239
    g9: ArcOfCircle CenterX=-49.19 CenterY=15.75 CenterZ=0 NormalX=0 NormalY=0 NormalZ=1 AngleXU=0 Radius=1.5 StartAngle=1.5708 EndAngle=4.71239
    g10: ArcOfCircle CenterX=-49.19 CenterY=10 CenterZ=0 NormalX=0 NormalY=0 NormalZ=1 AngleXU=0 Radius=1.5 StartAngle=1.5708 EndAngle=4.71239
    g11: ArcOfCircle CenterX=-49.19 CenterY=4.25 CenterZ=0 NormalX=0 NormalY=0 NormalZ=1 AngleXU=0 Radius=1.5 StartAngle=1.5708 EndAngle=4.71239
    g12: LineSegment StartX=-49.19 StartY=69.25 StartZ=0 EndX=-49.19 EndY=66.25 EndZ=0
    g13: LineSegment StartX=-49.19 StartY=63.5 StartZ=0 EndX=-49.19 EndY=60.5 EndZ=0
    g14: LineSegment StartX=-49.19 StartY=57.75 StartZ=0 EndX=-49.19 EndY=54.75 EndZ=0
    g15: LineSegment StartX=-49.19 StartY=52 StartZ=0 EndX=-49.19 EndY=49 EndZ=0
    g16: LineSegment StartX=-49.19 StartY=46.25 StartZ=0 EndX=-49.19 EndY=43.25 EndZ=0
    g17: LineSegment StartX=-49.19 StartY=40.5 StartZ=0 EndX=-49.19 EndY=37.5 EndZ=0
    g18: LineSegment StartX=-49.19 StartY=34.5 StartZ=0 EndX=-49.19 EndY=31.5 EndZ=0
    g19: LineSegment StartX=-49.19 StartY=28.75 StartZ=0 EndX=-49.19 EndY=25.75 EndZ=0
    g20: LineSegment StartX=-49.19 StartY=23 StartZ=0 EndX=-49.19 EndY=20 EndZ=0
    g21: LineSegment StartX=-49.19 StartY=17.25 StartZ=0 EndX=-49.19 EndY=14.25 EndZ=0
    g22: LineSegment StartX=-49.19 StartY=11.5 StartZ=0 EndX=-49.19 EndY=8.5 EndZ=0
    g23: LineSegment StartX=-49.19 StartY=5.75 StartZ=0 EndX=-49.19 EndY=2.75 EndZ=0
  constraints (48):
    c: Block(g0)
    c: Block(g1)
    c: Block(g2)
    c: Block(g3)
    c: Block(g4)
    c: Block(g5)
    c: Block(g6)
    c: Block(g7)
    c: Block(g8)
    c: Block(g9)
    c: Block(g10)
    c: Block(g11)
    c: Coincident(g12,g0)
    c: Coincident(g12,g0)
    c: Vertical(g12)
    c: Vertical(g13)
    c: Coincident(g13,g1)
    c: Vertical(g14)
    c: Coincident(g14,g2)
    c: Vertical(g15)
    c: Coincident(g15,g3)
    c: Vertical(g16)
    c: Coincident(g16,g4)
    c: Vertical(g17)
    c: Coincident(g17,g5)
    c: Vertical(g18)
    c: Coincident(g18,g6)
    c: Vertical(g19)
    c: Coincident(g19,g7)
    c: Vertical(g20)
    c: Coincident(g20,g8)
    c: Vertical(g21)
    c: Coincident(g21,g9)
    c: Vertical(g22)
    c: Coincident(g22,g10)
    c: Vertical(g23)
    c: Coincident(g23,g11)
    c: Block(g23)
    c: Block(g22)
    c: Block(g21)
    c: Block(g20)
    c: Block(g13)
    c: Block(g14)
    c: Block(g15)
    c: Block(g16)
    c: Block(g17)
    c: Block(g18)
    c: Block(g19)
FEATURE [Part::Extrusion] Extrude022
  Base = -> Sketch030
  Dir = (1,-2e-16,2e-16)
  DirMode = 2
  FaceMakerClass = Part::FaceMakerBullseye
  LengthFwd = 19
  LengthRev = 0
  Placement = pos=(-19,0,0) rot=(0,0,1;0rad)
  Solid = true
  Symmetric = false
FEATURE [Part::Fillet] Fillet022
  Base = -> Extrude022
  Edges = 24 edges r=1.49: [Edge6,Edge11,Edge18,Edge23,Edge30,Edge35,Edge42,Edge47,Edge54,Edge59,Edge66,Edge71,Edge78,Edge83,Edge90,Edge95,Edge102,Edge107,Edge114,Edge119,Edge126,Edge131,Edge138,Edge143]
FEATURE [Part::Cut] Cut020  label="top010"
  Base = -> Cut019
  Tool = -> Fillet022
FEATURE [Sketcher::SketchObject] Sketch032
  FullyConstrained = true
  Placement = pos=(117,19,0) rot=(0.57735,0.57735,0.57735;2.0944rad)
  sketch-geometry (48):
    g0: LineSegment StartX=-49.19 StartY=69.25 StartZ=0 EndX=-49.19 EndY=66.25 EndZ=0
    g1: LineSegment StartX=-49.19 StartY=63.5 StartZ=0 EndX=-49.19 EndY=60.5 EndZ=0
    g2: LineSegment StartX=-49.19 StartY=57.75 StartZ=0 EndX=-49.19 EndY=54.75 EndZ=0
    g3: LineSegment StartX=-49.19 StartY=52 StartZ=0 EndX=-49.19 EndY=49 EndZ=0
    g4: LineSegment StartX=-49.19 StartY=46.25 StartZ=0 EndX=-49.19 EndY=43.25 EndZ=0
    g5: LineSegment StartX=-49.19 StartY=40.5 StartZ=0 EndX=-49.19 EndY=37.5 EndZ=0
    g6: LineSegment StartX=-49.19 StartY=34.5 StartZ=0 EndX=-49.19 EndY=31.5 EndZ=0
    g7: LineSegment StartX=-49.19 StartY=28.75 StartZ=0 EndX=-49.19 EndY=25.75 EndZ=0
    g8: LineSegment StartX=-49.19 StartY=23 StartZ=0 EndX=-49.19 EndY=20 EndZ=0
    g9: LineSegment StartX=-49.19 StartY=17.25 StartZ=0 EndX=-49.19 EndY=14.25 EndZ=0
    g10: LineSegment StartX=-49.19 StartY=11.5 StartZ=0 EndX=-49.19 EndY=8.5 EndZ=0
    g11: LineSegment StartX=-49.19 StartY=5.75 StartZ=0 EndX=-49.19 EndY=2.75 EndZ=0
    g12: ArcOfCircle CenterX=-1.5 CenterY=67.75 CenterZ=0 NormalX=0 NormalY=0 NormalZ=1 AngleXU=0 Radius=1.5 StartAngle=4.71239 EndAngle=7.85398
    g13: ArcOfCircle CenterX=-1.5 CenterY=62 CenterZ=0 NormalX=0 NormalY=0 NormalZ=1 AngleXU=0 Radius=1.5 StartAngle=4.71239 EndAngle=7.85398
    g14: ArcOfCircle CenterX=-1.5 CenterY=56.25 CenterZ=0 NormalX=0 NormalY=0 NormalZ=1 AngleXU=0 Radius=1.5 StartAngle=4.71239 EndAngle=7.85398
    g15: ArcOfCircle CenterX=-11.49 CenterY=50.5 CenterZ=0 NormalX=0 NormalY=0 NormalZ=1 AngleXU=0 Radius=1.5 StartAngle=4.71239 EndAngle=7.85398
    g16: ArcOfCircle CenterX=-16.28 CenterY=44.75 CenterZ=0 NormalX=0 NormalY=0 NormalZ=1 AngleXU=0 Radius=1.5 StartAngle=4.71239 EndAngle=7.85398
    g17: ArcOfCircle CenterX=-18.2337 CenterY=39 CenterZ=0 NormalX=0 NormalY=0 NormalZ=1 AngleXU=0 Radius=1.5 StartAngle=4.71485 EndAngle=7.85398
    g18: ArcOfCircle CenterX=-16.2837 CenterY=27.25 CenterZ=0 NormalX=0 NormalY=0 NormalZ=1 AngleXU=0 Radius=1.5 StartAngle=4.71485 EndAngle=7.85398
    g19: ArcOfCircle CenterX=-18.2337 CenterY=33 CenterZ=0 NormalX=0 NormalY=0 NormalZ=1 AngleXU=0 Radius=1.5 StartAngle=4.71485 EndAngle=7.85398
    g20: ArcOfCircle CenterX=-11.49 CenterY=21.5 CenterZ=0 NormalX=0 NormalY=0 NormalZ=1 AngleXU=0 Radius=1.5 StartAngle=4.71239 EndAngle=7.85398
    g21: ArcOfCircle CenterX=-1.5 CenterY=4.25 CenterZ=0 NormalX=0 NormalY=0 NormalZ=1 AngleXU=0 Radius=1.5 StartAngle=4.71239 EndAngle=7.85398
    g22: ArcOfCircle CenterX=-1.5 CenterY=10 CenterZ=0 NormalX=0 NormalY=0 NormalZ=1 AngleXU=0 Radius=1.5 StartAngle=4.71239 EndAngle=7.85398
    g23: ArcOfCircle CenterX=-1.5 CenterY=15.75 CenterZ=0 NormalX=0 NormalY=0 NormalZ=1 AngleXU=0 Radius=1.5 StartAngle=4.71239 EndAngle=7.85398
    g24: LineSegment StartX=-49.19 StartY=69.25 StartZ=0 EndX=-1.5 EndY=69.25 EndZ=0
    g25: LineSegment StartX=-49.19 StartY=66.25 StartZ=0 EndX=-1.5 EndY=66.25 EndZ=0
    g26: LineSegment StartX=-49.19 StartY=63.5 StartZ=0 EndX=-1.5 EndY=63.5 EndZ=0
    g27: LineSegment StartX=-49.19 StartY=60.5 StartZ=0 EndX=-1.5 EndY=60.5 EndZ=0
    g28: LineSegment StartX=-49.19 StartY=57.75 StartZ=0 EndX=-1.5 EndY=57.75 EndZ=0
    g29: LineSegment StartX=-49.19 StartY=54.75 StartZ=0 EndX=-1.5 EndY=54.75 EndZ=0
    g30: LineSegment StartX=-49.19 StartY=52 StartZ=0 EndX=-11.49 EndY=52 EndZ=0
    g31: LineSegment StartX=-49.19 StartY=49 StartZ=0 EndX=-11.49 EndY=49 EndZ=0
    g32: LineSegment StartX=-49.19 StartY=46.25 StartZ=0 EndX=-16.28 EndY=46.25 EndZ=0
    g33: LineSegment StartX=-49.19 StartY=43.25 StartZ=0 EndX=-16.28 EndY=43.25 EndZ=0
    g34: LineSegment StartX=-49.19 StartY=40.5 StartZ=0 EndX=-18.2337 EndY=40.5 EndZ=0
    g35: LineSegment StartX=-49.19 StartY=37.5 StartZ=0 EndX=-18.23 EndY=37.5 EndZ=0
    g36: LineSegment StartX=-49.19 StartY=34.5 StartZ=0 EndX=-18.2337 EndY=34.5 EndZ=0
    g37: LineSegment StartX=-49.19 StartY=31.5 StartZ=0 EndX=-18.23 EndY=31.5 EndZ=0
    g38: LineSegment StartX=-49.19 StartY=28.75 StartZ=0 EndX=-16.2837 EndY=28.75 EndZ=0
    g39: LineSegment StartX=-49.19 StartY=25.75 StartZ=0 EndX=-16.28 EndY=25.75 EndZ=0
    g40: LineSegment StartX=-49.19 StartY=23 StartZ=0 EndX=-11.49 EndY=23 EndZ=0
    g41: LineSegment StartX=-49.19 StartY=20 StartZ=0 EndX=-11.49 EndY=20 EndZ=0
    g42: LineSegment StartX=-49.19 StartY=17.25 StartZ=0 EndX=-1.5 EndY=17.25 EndZ=0
    g43: LineSegment StartX=-49.19 StartY=14.25 StartZ=0 EndX=-1.5 EndY=14.25 EndZ=0
    g44: LineSegment StartX=-49.19 StartY=11.5 StartZ=0 EndX=-1.5 EndY=11.5 EndZ=0
    g45: LineSegment StartX=-49.19 StartY=8.5 StartZ=0 EndX=-1.5 EndY=8.5 EndZ=0
    g46: LineSegment StartX=-49.19 StartY=5.75 StartZ=0 EndX=-1.5 EndY=5.75 EndZ=0
    g47: LineSegment StartX=-49.19 StartY=2.75 StartZ=0 EndX=-1.5 EndY=2.75 EndZ=0
  constraints (120):
    c: Vertical(g0)
    c: Distance(g0) = 3
    c: Block(g0)
    c: Vertical(g1)
    c: Distance(g1) = 3
    c: Vertical(g2)
    c: Equal(g0,g2) = 3
    c: Block(g2)
    c: Vertical(g3)
    c: Equal(g1,g3) = 3
    c: Vertical(g4)
    c: Equal(g0,g4) = 3
    c: Block(g4)
    c: Vertical(g5)
    c: Equal(g1,g5) = 3
    c: Vertical(g6)
    c: Equal(g0,g6) = 3
    c: Block(g6)
    c: Vertical(g7)
    c: Equal(g1,g7) = 3
    c: Vertical(g8)
    c: Equal(g0,g8) = 3
    c: Block(g8)
    c: Vertical(g9)
    c: Equal(g1,g9) = 3
    c: Vertical(g10)
    c: Equal(g0,g10) = 3
    c: Block(g10)
    c: Vertical(g11)
    c: Equal(g1,g11) = 3
    c: Block(g12)
    c: Block(g13)
    c: Block(g14)
    c: Block(g15)
    c: Block(g16)
    c: Block(g17)
    c: Block(g18)
    c: Block(g19)
    c: Block(g20)
    c: Block(g21)
    c: Block(g22)
    c: Block(g23)
    c: Block(g11)
    c: Block(g9)
    c: Block(g7)
    c: Block(g5)
    c: Block(g3)
    c: Block(g1)
    c: Coincident(g24,g0)
    c: Coincident(g24,g12)
    c: Horizontal(g24)
    c: Coincident(g25,g0)
    c: Coincident(g25,g12)
    c: Horizontal(g25)
    c: Coincident(g26,g1)
    c: Coincident(g26,g13)
    c: Horizontal(g26)
    c: Coincident(g27,g1)
    c: Coincident(g27,g13)
    c: Horizontal(g27)
    c: Coincident(g28,g2)
    c: Coincident(g28,g14)
    c: Horizontal(g28)
    c: Coincident(g29,g2)
    c: Coincident(g29,g14)
    c: Horizontal(g29)
    c: Coincident(g30,g3)
    c: Coincident(g30,g15)
    c: Horizontal(g30)
    c: Coincident(g31,g3)
    c: Coincident(g31,g15)
    c: Horizontal(g31)
    c: Coincident(g32,g4)
    c: Coincident(g32,g16)
    c: Horizontal(g32)
    c: Coincident(g33,g4)
    c: Coincident(g33,g16)
    c: Horizontal(g33)
    c: Coincident(g34,g5)
    c: Coincident(g34,g17)
    c: Horizontal(g34)
    c: Coincident(g35,g5)
    c: Coincident(g35,g17)
    c: Horizontal(g35)
    c: Coincident(g36,g6)
    c: Coincident(g36,g19)
    c: Horizontal(g36)
    c: Coincident(g37,g6)
    c: Coincident(g37,g19)
    c: Horizontal(g37)
    c: Coincident(g38,g7)
    c: Coincident(g38,g18)
    c: Horizontal(g38)
    c: Coincident(g39,g7)
    c: Coincident(g39,g18)
    c: Horizontal(g39)
    c: Coincident(g40,g8)
    c: Coincident(g40,g20)
    c: Horizontal(g40)
    c: Coincident(g41,g8)
    c: Coincident(g41,g20)
    c: Horizontal(g41)
    c: Coincident(g42,g9)
    c: Coincident(g42,g23)
    c: Horizontal(g42)
    c: Coincident(g43,g9)
    c: Coincident(g43,g23)
    c: Horizontal(g43)
    c: Coincident(g44,g10)
    c: Coincident(g44,g22)
    c: Horizontal(g44)
    c: Coincident(g45,g10)
    c: Coincident(g45,g22)
    c: Horizontal(g45)
    c: Coincident(g46,g11)
    c: Coincident(g46,g21)
    c: Horizontal(g46)
    c: Coincident(g47,g11)
    c: Coincident(g47,g21)
    c: Horizontal(g47)
FEATURE [Part::Extrusion] Extrude023
  Base = -> Sketch032
  Dir = (1,-2e-16,2e-16)
  DirMode = 2
  FaceMakerClass = Part::FaceMakerBullseye
  LengthFwd = 19
  LengthRev = 0
  Placement = pos=(-19,0,0) rot=(0,0,1;0rad)
  Solid = true
  Symmetric = false
FEATURE [Part::Fillet] Fillet023
  Base = -> Extrude023
  Edges = 24 edges r=1.49: [Edge6,Edge11,Edge18,Edge23,Edge30,Edge35,Edge42,Edge47,Edge54,Edge59,Edge66,Edge71,Edge78,Edge83,Edge90,Edge95,Edge102,Edge107,Edge114,Edge119,Edge126,Edge131,Edge138,Edge143]
  Placement = pos=(0,0.05,0) rot=(0,0,1;0rad)
FEATURE [Part::Cut] Cut014  label="bottom003"
  Base = -> Cut007
  Tool = -> Fusion047
FEATURE [Part::Cut] Cut021  label="bottom004"
  Base = -> Cut014
  Tool = -> Fillet023
FEATURE [Sketcher::SketchObject] Sketch033
  FullyConstrained = true
  Placement = pos=(117,19,0) rot=(0.57735,0.57735,0.57735;2.0944rad)
  sketch-geometry (8):
    g0: LineSegment StartX=-49.19 StartY=69.25 StartZ=0 EndX=-49.19 EndY=66.25 EndZ=0
    g1: LineSegment StartX=-49.19 StartY=5.75 StartZ=0 EndX=-49.19 EndY=2.75 EndZ=0
    g2: ArcOfCircle CenterX=-1.5 CenterY=67.75 CenterZ=0 NormalX=0 NormalY=0 NormalZ=1 AngleXU=0 Radius=1.5 StartAngle=4.71239 EndAngle=7.85398
    g3: ArcOfCircle CenterX=-1.5 CenterY=4.25 CenterZ=0 NormalX=0 NormalY=0 NormalZ=1 AngleXU=0 Radius=1.5 StartAngle=4.71239 EndAngle=7.85398
    g4: LineSegment StartX=-49.19 StartY=69.25 StartZ=0 EndX=-1.5 EndY=69.25 EndZ=0
    g5: LineSegment StartX=-49.19 StartY=66.25 StartZ=0 EndX=-1.5 EndY=66.25 EndZ=0
    g6: LineSegment StartX=-49.19 StartY=5.75 StartZ=0 EndX=-1.5 EndY=5.75 EndZ=0
    g7: LineSegment StartX=-49.19 StartY=2.75 StartZ=0 EndX=-1.5 EndY=2.75 EndZ=0
  constraints (19):
    c: Vertical(g0)
    c: Distance(g0) = 3
    c: Block(g0)
    c: Vertical(g1)
    c: Block(g2)
    c: Block(g3)
    c: Block(g1)
    c: Coincident(g4,g0)
    c: Coincident(g4,g2)
    c: Horizontal(g4)
    c: Coincident(g5,g0)
    c: Coincident(g5,g2)
    c: Horizontal(g5)
    c: Coincident(g6,g1)
    c: Coincident(g6,g3)
    c: Horizontal(g6)
    c: Coincident(g7,g1)
    c: Coincident(g7,g3)
    c: Horizontal(g7)
FEATURE [Sketcher::SketchObject] Sketch034
  FullyConstrained = true
  Placement = pos=(117,19,0) rot=(0.57735,0.57735,0.57735;2.0944rad)
  sketch-geometry (8):
    g0: LineSegment StartX=-49.19 StartY=63.5 StartZ=0 EndX=-49.19 EndY=60.5 EndZ=0
    g1: LineSegment StartX=-49.19 StartY=11.5 StartZ=0 EndX=-49.19 EndY=8.5 EndZ=0
    g2: ArcOfCircle CenterX=-1.5 CenterY=62 CenterZ=0 NormalX=0 NormalY=0 NormalZ=1 AngleXU=0 Radius=1.5 StartAngle=4.71239 EndAngle=7.85398
    g3: ArcOfCircle CenterX=-1.5 CenterY=10 CenterZ=0 NormalX=0 NormalY=0 NormalZ=1 AngleXU=0 Radius=1.5 StartAngle=4.71239 EndAngle=7.85398
    g4: LineSegment StartX=-49.19 StartY=63.5 StartZ=0 EndX=-1.5 EndY=63.5 EndZ=0
    g5: LineSegment StartX=-49.19 StartY=60.5 StartZ=0 EndX=-1.5 EndY=60.5 EndZ=0
    g6: LineSegment StartX=-49.19 StartY=11.5 StartZ=0 EndX=-1.5 EndY=11.5 EndZ=0
    g7: LineSegment StartX=-49.19 StartY=8.5 StartZ=0 EndX=-1.5 EndY=8.5 EndZ=0
  constraints (19):
    c: Vertical(g0)
    c: Distance(g0) = 3
    c: Vertical(g1)
    c: Block(g1)
    c: Block(g2)
    c: Block(g3)
    c: Block(g0)
    c: Coincident(g4,g0)
    c: Coincident(g4,g2)
    c: Horizontal(g4)
    c: Coincident(g5,g0)
    c: Coincident(g5,g2)
    c: Horizontal(g5)
    c: Coincident(g6,g1)
    c: Coincident(g6,g3)
    c: Horizontal(g6)
    c: Coincident(g7,g1)
    c: Coincident(g7,g3)
    c: Horizontal(g7)
FEATURE [Part::Extrusion] Extrude024
  Base = -> Sketch033
  Dir = (1,0,0)
  DirMode = 2
  FaceMakerClass = Part::FaceMakerBullseye
  LengthFwd = 10
  LengthRev = 0
  Solid = true
  Symmetric = false
FEATURE [Part::Extrusion] Extrude025
  Base = -> Sketch034
  Dir = (1,0,0)
  DirMode = 2
  FaceMakerClass = Part::FaceMakerBullseye
  LengthFwd = 10
  LengthRev = 0
  Solid = true
  Symmetric = false
FEATURE [Part::Fillet] Fillet024  label="removeFromtMoreFrontCaseScrewRetainers"
  Base = -> Extrude024
  Edges = 4 edges r=1.49: [Edge6,Edge11,Edge18,Edge23]
  Placement = pos=(-11,0,0) rot=(0,0,1;0rad)
FEATURE [Part::Fillet] Fillet025  label="removeFromtMoreFrontCaseScrewRetainers001"
  Base = -> Extrude025
  Edges = 4 edges r=1.49: [Edge6,Edge11,Edge18,Edge23]
  Placement = pos=(-19,0,0) rot=(0,0,1;0rad)
FEATURE [Part::Cut] Cut022
  Base = -> Cut015
  Tool = -> Fillet025
FEATURE [Part::Cut] Cut023  label="screwRetainers"
  Base = -> Cut022
  Tool = -> Fillet024
FEATURE [Part::MultiFuse] Fusion056  label="bottom005"
  Shapes = -> [Fusion044,Cut021]
FEATURE [Part::MultiFuse] Fusion057  label="casePillars001"
  Shapes = -> [Cut016,Fusion052]
FEATURE [Part::MultiFuse] Fusion058  label="bottom006"
  Shapes = -> [Fusion056,Cut023]
FEATURE [Part::MultiFuse] Fusion059  label="bottom007"
  Shapes = -> [Fusion058,Fillet005]
FEATURE [Part::MultiFuse] Fusion060  label="bottom008"
  Shapes = -> [Fusion059,Fusion]
FEATURE [Part::MultiFuse] Fusion061  label="top011"
  Shapes = -> [Cut006,Cut020]
FEATURE [Part::MultiFuse] Fusion062  label="top012"
  Shapes = -> [Fusion057,Fusion061]
FEATURE [Sketcher::SketchObject] Sketch035  label="topSketch007"
  FullyConstrained = true
  sketch-geometry (6):
    g0: LineSegment StartX=19 StartY=38 StartZ=0 EndX=117 EndY=38 EndZ=0
    g1: ArcOfCircle CenterX=19 CenterY=19 CenterZ=0 NormalX=0 NormalY=0 NormalZ=1 AngleXU=0 Radius=19 StartAngle=1.5708 EndAngle=3.14159
    g2: LineSegment StartX=117 StartY=38 StartZ=0 EndX=117 EndY=19 EndZ=0
    g3: LineSegment StartX=98 StartY=1.0161e-12 StartZ=0 EndX=5.22862e-06 EndY=1.0161e-12 EndZ=0
    g4: LineSegment StartX=5.22862e-06 StartY=19 StartZ=0 EndX=5.22862e-06 EndY=1.0161e-12 EndZ=0
    g5: ArcOfCircle CenterX=98 CenterY=19 CenterZ=0 NormalX=0 NormalY=0 NormalZ=1 AngleXU=0 Radius=19 StartAngle=4.71239 EndAngle=6.28319
  constraints (16):
    c: Horizontal(g0)
    c: Distance(g0) = 98
    c: Coincident(g1,g0)
    c: Block(g1)
    c: Coincident(g2,g0)
    c: Vertical(g2)
    c: Distance(g2) = 19
    c: Horizontal(g3)
    c: Coincident(g4,g1)
    c: Vertical(g4)
    c: Coincident(g3,g4)
    c: Block(g3)
    c: Coincident(g5,g2)
    c: Coincident(g5,g3)
    c: Block(g0)
    c: Block(g5)
FEATURE [Part::Extrusion] Extrude026  label="sideA001"
  Base = -> Sketch035
  Dir = (0,0,1)
  DirMode = 2
  FaceMakerClass = Part::FaceMakerBullseye
  LengthFwd = 3
  LengthRev = 0
  Placement = pos=(0,0,-2.7) rot=(0,0,1;0rad)
  Solid = true
  Symmetric = false
FEATURE [Sketcher::SketchObject] Sketch036  label="topSketch008"
  FullyConstrained = true
  sketch-geometry (6):
    g0: LineSegment StartX=19 StartY=38 StartZ=0 EndX=117 EndY=38 EndZ=0
    g1: ArcOfCircle CenterX=19 CenterY=19 CenterZ=0 NormalX=0 NormalY=0 NormalZ=1 AngleXU=0 Radius=19 StartAngle=1.5708 EndAngle=3.14159
    g2: LineSegment StartX=117 StartY=38 StartZ=0 EndX=117 EndY=19 EndZ=0
    g3: LineSegment StartX=98 StartY=1.0161e-12 StartZ=0 EndX=5.22862e-06 EndY=1.0161e-12 EndZ=0
    g4: LineSegment StartX=5.22862e-06 StartY=19 StartZ=0 EndX=5.22862e-06 EndY=1.0161e-12 EndZ=0
    g5: ArcOfCircle CenterX=98 CenterY=19 CenterZ=0 NormalX=0 NormalY=0 NormalZ=1 AngleXU=0 Radius=19 StartAngle=4.71239 EndAngle=6.28319
  constraints (16):
    c: Horizontal(g0)
    c: Distance(g0) = 98
    c: Coincident(g1,g0)
    c: Block(g1)
    c: Coincident(g2,g0)
    c: Vertical(g2)
    c: Distance(g2) = 19
    c: Horizontal(g3)
    c: Coincident(g4,g1)
    c: Vertical(g4)
    c: Coincident(g3,g4)
    c: Block(g3)
    c: Coincident(g5,g2)
    c: Coincident(g5,g3)
    c: Block(g0)
    c: Block(g5)
FEATURE [Part::Extrusion] Extrude027  label="sideB001"
  Base = -> Sketch036
  Dir = (0,0,1)
  DirMode = 2
  FaceMakerClass = Part::FaceMakerBullseye
  LengthFwd = 3
  LengthRev = 0
  Placement = pos=(0,0,71.7) rot=(0,0,1;0rad)
  Solid = true
  Symmetric = false
FEATURE [Part::MultiFuse] Fusion064  label="removeFromBottom"
  Shapes = -> [Extrude026,Extrude027]
FEATURE [Part::Cut] Cut024  label="bottom009"
  Base = -> Fusion060
  Tool = -> Fusion064
FEATURE [Sketcher::SketchObject] Sketch037  label="topSketch009"
  FullyConstrained = true
  sketch-geometry (6):
    g0: ArcOfCircle CenterX=19 CenterY=19 CenterZ=0 NormalX=0 NormalY=0 NormalZ=1 AngleXU=0 Radius=19 StartAngle=1.5708 EndAngle=3.14159
    g1: LineSegment StartX=5.22862e-06 StartY=19 StartZ=0 EndX=5.22862e-06 EndY=1.19904e-11 EndZ=0
    g2: LineSegment StartX=19 StartY=38 StartZ=0 EndX=124 EndY=38 EndZ=0
    g3: LineSegment StartX=5.22862e-06 StartY=1.19904e-11 StartZ=0 EndX=105 EndY=1.19904e-11 EndZ=0
    g4: ArcOfCircle CenterX=105 CenterY=19 CenterZ=0 NormalX=0 NormalY=0 NormalZ=1 AngleXU=0 Radius=19 StartAngle=4.71239 EndAngle=6.28319
    g5: LineSegment StartX=124 StartY=38 StartZ=0 EndX=124 EndY=19 EndZ=0
  constraints (16):
    c: Block(g0)
    c: Coincident(g1,g0)
    c: Vertical(g1)
    c: Horizontal(g2)
    c: Distance(g2) = 105
    c: Coincident(g2,g0)
    c: Distance(g1) = 19
    c: Coincident(g3,g1)
    c: Horizontal(g3)
    c: Distance(g3) = 105
    c: Block(g4)
    c: Coincident(g4,g3)
    c: Coincident(g5,g2)
    c: Coincident(g5,g4)
    c: Vertical(g5)
    c: Distance(g5) = 19
FEATURE [Part::Extrusion] Extrude028  label="sideB"
  Base = -> Sketch037
  Dir = (0,0,1)
  DirMode = 2
  FaceMakerClass = Part::FaceMakerBullseye
  LengthFwd = 3
  LengthRev = 0
  Placement = pos=(0,0,72) rot=(0,0,1;0rad)
  Solid = true
  Symmetric = false
FEATURE [Sketcher::SketchObject] Sketch038  label="topSketch010"
  FullyConstrained = true
  sketch-geometry (20):
    g0: LineSegment StartX=5.21097e-06 StartY=3 StartZ=0 EndX=5.21097e-06 EndY=19 EndZ=0
    g1: ArcOfCircle CenterX=19 CenterY=19 CenterZ=0 NormalX=0 NormalY=0 NormalZ=1 AngleXU=0 Radius=19 StartAngle=1.5708 EndAngle=3.14159
    g2: ArcOfCircle CenterX=19 CenterY=19 CenterZ=0 NormalX=0 NormalY=0 NormalZ=1 AngleXU=0 Radius=16 StartAngle=1.5708 EndAngle=3.14159
    g3: LineSegment StartX=114 StartY=35 StartZ=0 EndX=19 EndY=35 EndZ=0
    g4: LineSegment StartX=5.21097e-06 StartY=3 StartZ=0 EndX=5.21097e-06 EndY=0 EndZ=0
    g5: LineSegment StartX=3 StartY=0 StartZ=0 EndX=5.21097e-06 EndY=0 EndZ=0
    g6: LineSegment StartX=3 StartY=19 StartZ=0 EndX=3 EndY=0 EndZ=0
    g7: LineSegment StartX=19 StartY=38 StartZ=0 EndX=124 EndY=38 EndZ=0
    g8: Circle CenterX=119 CenterY=35 CenterZ=0 NormalX=0 NormalY=0 NormalZ=1 AngleXU=0 Radius=1
    g9: Circle CenterX=121 CenterY=35 CenterZ=0 NormalX=0 NormalY=0 NormalZ=1 AngleXU=0 Radius=1
    g10: Circle CenterX=121 CenterY=33 CenterZ=0 NormalX=0 NormalY=0 NormalZ=1 AngleXU=0 Radius=1
    g11: BSplineCurve PolesCount=3 KnotsCount=2 Degree=2 IsPeriodic=0
    g12: GeomPoint X=119 Y=35 Z=0
    g13: GeomPoint X=121 Y=33 Z=0
    g14: LineSegment StartX=119 StartY=35 StartZ=0 EndX=114 EndY=35 EndZ=0
    g15: ArcOfCircle CenterX=105 CenterY=19 CenterZ=0 NormalX=0 NormalY=0 NormalZ=1 AngleXU=0 Radius=19 StartAngle=5.7297 EndAngle=6.28319
    g16: ArcOfCircle CenterX=105 CenterY=19 CenterZ=0 NormalX=0 NormalY=0 NormalZ=1 AngleXU=0 Radius=16 StartAngle=5.60905 EndAngle=6.28319
    g17: LineSegment StartX=121 StartY=33 StartZ=0 EndX=121 EndY=19 EndZ=0
    g18: LineSegment StartX=124 StartY=38 StartZ=0 EndX=124 EndY=19 EndZ=0
    g19: LineSegment StartX=117.5 StartY=9.01251 StartZ=0 EndX=121.163 EndY=9.0125 EndZ=0
  constraints (46):
    c: Vertical(g0)
    c: Block(g0)
    c: Coincident(g1,g0)
    c: Block(g1)
    c: Coincident(g2,g1)
    c: Block(g2)
    c: Coincident(g3,g2)
    c: Horizontal(g3)
    c: Tangent(g3,g2)
    c: Coincident(g4,g0)
    c: Distance(g4) = 3
    c: Vertical(g4)
    c: Coincident(g5,g4)
    c: Horizontal(g5)
    c: Coincident(g6,g2)
    c: Coincident(g6,g5)
    c: Vertical(g6)
    c: Horizontal(g7)
    c: Distance(g7) = 105
    c: Coincident(g7,g1)
    c: Block(g3)
    c: Weight(g8) = 1
    c: Equal(g8,g9)
    c: Equal(g8,g10)
    c: InternalAlignment(g8,g11)
    c: InternalAlignment(g9,g11)
    c: InternalAlignment(g10,g11)
    c: InternalAlignment(g12,g11)
    c: InternalAlignment(g13,g11)
    c: Block(g11)
    c: Coincident(g14,g11)
    c: Coincident(g14,g3)
    c: Horizontal(g14)
    c: Block(g15)
    c: Coincident(g16,g15)
    c: Block(g16)
    c: Coincident(g17,g11)
    c: Coincident(g17,g16)
    c: Vertical(g17)
    c: Distance(g17) = 14
    c: Coincident(g18,g7)
    c: Coincident(g18,g15)
    c: Vertical(g18)
    c: Distance(g18) = 19
    c: Coincident(g19,g16)
    c: Coincident(g19,g15)
FEATURE [Part::Extrusion] Extrude029
  Base = -> Sketch038
  Dir = (0,0,1)
  DirMode = 2
  FaceMakerClass = Part::FaceMakerBullseye
  LengthFwd = 72
  LengthRev = 0
  Solid = true
  Symmetric = false
FEATURE [Part::Feature] Face085
  shape: bbox 4.8 x 25.5 x 2e-07 mm, 1 faces, 0 solids (baked)
FEATURE [Part::Revolution] Revolve089  label="moreFrontCaseScrewPost003"
  Angle = 360
  Axis = (0,1,0)
  Base = (0,0,0)
  FaceMakerClass = Part::FaceMakerBullseye
  Placement = pos=(109.5,4.5,3.5) rot=(0,0,1;0rad)
  Solid = false
  Source = -> Face085
  Symmetric = false
FEATURE [Part::Feature] Face086
  shape: bbox 4.8 x 25.5 x 2e-07 mm, 1 faces, 0 solids (baked)
FEATURE [Part::Revolution] Revolve090  label="moreFrontCaseScrewPost004"
  Angle = 360
  Axis = (0,1,0)
  Base = (0,0,0)
  FaceMakerClass = Part::FaceMakerBullseye
  Placement = pos=(109.5,4.5,68.5) rot=(0,0,1;0rad)
  Solid = false
  Source = -> Face086
  Symmetric = false
FEATURE [Part::Fillet] Fillet026  label="top013"
  Base = -> Extrude029
  Edges = 1 edges r=2: [Edge35]
FEATURE [Sketcher::SketchObject] Sketch039
  FullyConstrained = true
  sketch-geometry (7):
    g0: LineSegment StartX=0 StartY=0 StartZ=0 EndX=0 EndY=6 EndZ=0
    g1: Circle CenterX=0 CenterY=0 CenterZ=0 NormalX=0 NormalY=0 NormalZ=1 AngleXU=0 Radius=1
    g2: Circle CenterX=8 CenterY=6 CenterZ=0 NormalX=0 NormalY=0 NormalZ=1 AngleXU=0 Radius=1
    g3: BSplineCurve PolesCount=3 KnotsCount=2 Degree=2 IsPeriodic=0
    g4: GeomPoint X=0 Y=0 Z=0
    g5: GeomPoint X=8 Y=6 Z=0
    g6: LineSegment StartX=0 StartY=6 StartZ=0 EndX=8 EndY=6 EndZ=0
  constraints (14):
    c: Coincident(g0,g-1)
    c: Distance(g0) = 6
    c: Vertical(g0)
    c: Coincident(g3,g0)
    c: Weight(g1) = 1
    c: Equal(g1,g2)
    c: InternalAlignment(g1,g3)
    c: InternalAlignment(g2,g3)
    c: InternalAlignment(g4,g3)
    c: InternalAlignment(g5,g3)
    c: Block(g3)
    c: Coincident(g6,g0)
    c: Coincident(g6,g3)
    c: Horizontal(g6)
FEATURE [Sketcher::SketchObject] Sketch040
  FullyConstrained = true
  sketch-geometry (7):
    g0: LineSegment StartX=0 StartY=0 StartZ=0 EndX=0 EndY=6 EndZ=0
    g1: Circle CenterX=0 CenterY=0 CenterZ=0 NormalX=0 NormalY=0 NormalZ=1 AngleXU=0 Radius=1
    g2: Circle CenterX=8 CenterY=6 CenterZ=0 NormalX=0 NormalY=0 NormalZ=1 AngleXU=0 Radius=1
    g3: BSplineCurve PolesCount=3 KnotsCount=2 Degree=2 IsPeriodic=0
    g4: GeomPoint X=0 Y=0 Z=0
    g5: GeomPoint X=8 Y=6 Z=0
    g6: LineSegment StartX=0 StartY=6 StartZ=0 EndX=8 EndY=6 EndZ=0
  constraints (14):
    c: Coincident(g0,g-1)
    c: Distance(g0) = 6
    c: Vertical(g0)
    c: Coincident(g3,g0)
    c: Weight(g1) = 1
    c: Equal(g1,g2)
    c: InternalAlignment(g1,g3)
    c: InternalAlignment(g2,g3)
    c: InternalAlignment(g4,g3)
    c: InternalAlignment(g5,g3)
    c: Block(g3)
    c: Coincident(g6,g0)
    c: Coincident(g6,g3)
    c: Horizontal(g6)
FEATURE [Sketcher::SketchObject] Sketch041
  FullyConstrained = true
  sketch-geometry (7):
    g0: LineSegment StartX=0 StartY=0 StartZ=0 EndX=0 EndY=6 EndZ=0
    g1: Circle CenterX=0 CenterY=0 CenterZ=0 NormalX=0 NormalY=0 NormalZ=1 AngleXU=0 Radius=1
    g2: Circle CenterX=8 CenterY=6 CenterZ=0 NormalX=0 NormalY=0 NormalZ=1 AngleXU=0 Radius=1
    g3: BSplineCurve PolesCount=3 KnotsCount=2 Degree=2 IsPeriodic=0
    g4: GeomPoint X=0 Y=0 Z=0
    g5: GeomPoint X=8 Y=6 Z=0
    g6: LineSegment StartX=0 StartY=6 StartZ=0 EndX=8 EndY=6 EndZ=0
  constraints (14):
    c: Coincident(g0,g-1)
    c: Distance(g0) = 6
    c: Vertical(g0)
    c: Coincident(g3,g0)
    c: Weight(g1) = 1
    c: Equal(g1,g2)
    c: InternalAlignment(g1,g3)
    c: InternalAlignment(g2,g3)
    c: InternalAlignment(g4,g3)
    c: InternalAlignment(g5,g3)
    c: Block(g3)
    c: Coincident(g6,g0)
    c: Coincident(g6,g3)
    c: Horizontal(g6)
FEATURE [Sketcher::SketchObject] Sketch042
  FullyConstrained = true
  sketch-geometry (7):
    g0: LineSegment StartX=0 StartY=0 StartZ=0 EndX=0 EndY=6 EndZ=0
    g1: Circle CenterX=0 CenterY=0 CenterZ=0 NormalX=0 NormalY=0 NormalZ=1 AngleXU=0 Radius=1
    g2: Circle CenterX=8 CenterY=6 CenterZ=0 NormalX=0 NormalY=0 NormalZ=1 AngleXU=0 Radius=1
    g3: BSplineCurve PolesCount=3 KnotsCount=2 Degree=2 IsPeriodic=0
    g4: GeomPoint X=0 Y=0 Z=0
    g5: GeomPoint X=8 Y=6 Z=0
    g6: LineSegment StartX=0 StartY=6 StartZ=0 EndX=8 EndY=6 EndZ=0
  constraints (14):
    c: Coincident(g0,g-1)
    c: Distance(g0) = 6
    c: Vertical(g0)
    c: Coincident(g3,g0)
    c: Weight(g1) = 1
    c: Equal(g1,g2)
    c: InternalAlignment(g1,g3)
    c: InternalAlignment(g2,g3)
    c: InternalAlignment(g4,g3)
    c: InternalAlignment(g5,g3)
    c: Block(g3)
    c: Coincident(g6,g0)
    c: Coincident(g6,g3)
    c: Horizontal(g6)
FEATURE [Part::Extrusion] Extrude030  label="caseScrewPillarBracket008"
  Base = -> Sketch039
  Dir = (0,0,1)
  DirMode = 2
  FaceMakerClass = Part::FaceMakerBullseye
  LengthFwd = 2.4
  LengthRev = 0
  Placement = pos=(15.76,29,8.8) rot=(0,1,0;0rad)
  Solid = true
  Symmetric = false
FEATURE [Part::Extrusion] Extrude031  label="caseScrewPillarBracket009"
  Base = -> Sketch040
  Dir = (0,0,1)
  DirMode = 2
  FaceMakerClass = Part::FaceMakerBullseye
  LengthFwd = 2.4
  LengthRev = 0
  Placement = pos=(15.76,29,60.8) rot=(0,0,1;0rad)
  Solid = true
  Symmetric = false
FEATURE [Part::Extrusion] Extrude032  label="caseScrewPillarBracket010"
  Base = -> Sketch041
  Dir = (0,0,1)
  DirMode = 2
  FaceMakerClass = Part::FaceMakerBullseye
  LengthFwd = 2.4
  LengthRev = 0
  Placement = pos=(13.7,29,13.26) rot=(0,-1,0;1.5708rad)
  Solid = true
  Symmetric = false
FEATURE [Part::Extrusion] Extrude033  label="caseScrewPillarBracket011"
  Base = -> Sketch042
  Dir = (0,0,1)
  DirMode = 2
  FaceMakerClass = Part::FaceMakerBullseye
  LengthFwd = 2.4
  LengthRev = 0
  Placement = pos=(11.3,29,58.74) rot=(0,1,0;1.5708rad)
  Solid = true
  Symmetric = false
FEATURE [Sketcher::SketchObject] Sketch043
  FullyConstrained = true
  sketch-geometry (7):
    g0: LineSegment StartX=0 StartY=0 StartZ=0 EndX=0 EndY=6 EndZ=0
    g1: Circle CenterX=0 CenterY=0 CenterZ=0 NormalX=0 NormalY=0 NormalZ=1 AngleXU=0 Radius=1
    g2: Circle CenterX=8 CenterY=6 CenterZ=0 NormalX=0 NormalY=0 NormalZ=1 AngleXU=0 Radius=1
    g3: BSplineCurve PolesCount=3 KnotsCount=2 Degree=2 IsPeriodic=0
    g4: GeomPoint X=0 Y=0 Z=0
    g5: GeomPoint X=8 Y=6 Z=0
    g6: LineSegment StartX=0 StartY=6 StartZ=0 EndX=8 EndY=6 EndZ=0
  constraints (14):
    c: Coincident(g0,g-1)
    c: Distance(g0) = 6
    c: Vertical(g0)
    c: Coincident(g3,g0)
    c: Weight(g1) = 1
    c: Equal(g1,g2)
    c: InternalAlignment(g1,g3)
    c: InternalAlignment(g2,g3)
    c: InternalAlignment(g4,g3)
    c: InternalAlignment(g5,g3)
    c: Block(g3)
    c: Coincident(g6,g0)
    c: Coincident(g6,g3)
    c: Horizontal(g6)
FEATURE [Part::Extrusion] Extrude034  label="caseScrewPillarBracket012"
  Base = -> Sketch043
  Dir = (0,0,1)
  DirMode = 2
  FaceMakerClass = Part::FaceMakerBullseye
  LengthFwd = 2.4
  LengthRev = 0
  Placement = pos=(88.3,29,65.23) rot=(0,1,0;1.5708rad)
  Solid = true
  Symmetric = false
FEATURE [Sketcher::SketchObject] Sketch044
  FullyConstrained = true
  sketch-geometry (7):
    g0: LineSegment StartX=0 StartY=0 StartZ=0 EndX=0 EndY=6 EndZ=0
    g1: Circle CenterX=0 CenterY=0 CenterZ=0 NormalX=0 NormalY=0 NormalZ=1 AngleXU=0 Radius=1
    g2: Circle CenterX=8 CenterY=6 CenterZ=0 NormalX=0 NormalY=0 NormalZ=1 AngleXU=0 Radius=1
    g3: BSplineCurve PolesCount=3 KnotsCount=2 Degree=2 IsPeriodic=0
    g4: GeomPoint X=0 Y=0 Z=0
    g5: GeomPoint X=8 Y=6 Z=0
    g6: LineSegment StartX=0 StartY=6 StartZ=0 EndX=8 EndY=6 EndZ=0
  constraints (14):
    c: Coincident(g0,g-1)
    c: Distance(g0) = 6
    c: Vertical(g0)
    c: Coincident(g3,g0)
    c: Weight(g1) = 1
    c: Equal(g1,g2)
    c: InternalAlignment(g1,g3)
    c: InternalAlignment(g2,g3)
    c: InternalAlignment(g4,g3)
    c: InternalAlignment(g5,g3)
    c: Block(g3)
    c: Coincident(g6,g0)
    c: Coincident(g6,g3)
    c: Horizontal(g6)
FEATURE [Part::Extrusion] Extrude035  label="caseScrewPillarBracket013"
  Base = -> Sketch044
  Dir = (0,0,1)
  DirMode = 2
  FaceMakerClass = Part::FaceMakerBullseye
  LengthFwd = 2.4
  LengthRev = 0
  Placement = pos=(90.7,29,6.77) rot=(0,-1,0;1.5708rad)
  Solid = true
  Symmetric = false
FEATURE [Sketcher::SketchObject] Sketch045
  FullyConstrained = true
  sketch-geometry (7):
    g0: LineSegment StartX=0 StartY=0 StartZ=0 EndX=0 EndY=6 EndZ=0
    g1: Circle CenterX=0 CenterY=0 CenterZ=0 NormalX=0 NormalY=0 NormalZ=1 AngleXU=0 Radius=1
    g2: Circle CenterX=8 CenterY=6 CenterZ=0 NormalX=0 NormalY=0 NormalZ=1 AngleXU=0 Radius=1
    g3: BSplineCurve PolesCount=3 KnotsCount=2 Degree=2 IsPeriodic=0
    g4: GeomPoint X=0 Y=0 Z=0
    g5: GeomPoint X=8 Y=6 Z=0
    g6: LineSegment StartX=0 StartY=6 StartZ=0 EndX=8 EndY=6 EndZ=0
  constraints (14):
    c: Coincident(g0,g-1)
    c: Distance(g0) = 6
    c: Vertical(g0)
    c: Coincident(g3,g0)
    c: Weight(g1) = 1
    c: Equal(g1,g2)
    c: InternalAlignment(g1,g3)
    c: InternalAlignment(g2,g3)
    c: InternalAlignment(g4,g3)
    c: InternalAlignment(g5,g3)
    c: Block(g3)
    c: Coincident(g6,g0)
    c: Coincident(g6,g3)
    c: Horizontal(g6)
FEATURE [Sketcher::SketchObject] Sketch046
  FullyConstrained = true
  sketch-geometry (7):
    g0: LineSegment StartX=0 StartY=0 StartZ=0 EndX=0 EndY=6 EndZ=0
    g1: Circle CenterX=0 CenterY=0 CenterZ=0 NormalX=0 NormalY=0 NormalZ=1 AngleXU=0 Radius=1
    g2: Circle CenterX=8 CenterY=6 CenterZ=0 NormalX=0 NormalY=0 NormalZ=1 AngleXU=0 Radius=1
    g3: BSplineCurve PolesCount=3 KnotsCount=2 Degree=2 IsPeriodic=0
    g4: GeomPoint X=0 Y=0 Z=0
    g5: GeomPoint X=8 Y=6 Z=0
    g6: LineSegment StartX=0 StartY=6 StartZ=0 EndX=8 EndY=6 EndZ=0
  constraints (14):
    c: Coincident(g0,g-1)
    c: Distance(g0) = 6
    c: Vertical(g0)
    c: Coincident(g3,g0)
    c: Weight(g1) = 1
    c: Equal(g1,g2)
    c: InternalAlignment(g1,g3)
    c: InternalAlignment(g2,g3)
    c: InternalAlignment(g4,g3)
    c: InternalAlignment(g5,g3)
    c: Block(g3)
    c: Coincident(g6,g0)
    c: Coincident(g6,g3)
    c: Horizontal(g6)
FEATURE [Part::Extrusion] Extrude036  label="caseScrewPillarBracket014"
  Base = -> Sketch045
  Dir = (0,0,1)
  DirMode = 2
  FaceMakerClass = Part::FaceMakerBullseye
  LengthFwd = 2.4
  LengthRev = 0
  Placement = pos=(110.7,29,6.77) rot=(0,-1,0;1.5708rad)
  Solid = true
  Symmetric = false
FEATURE [Part::Extrusion] Extrude037  label="caseScrewPillarBracket015"
  Base = -> Sketch046
  Dir = (0,0,1)
  DirMode = 2
  FaceMakerClass = Part::FaceMakerBullseye
  LengthFwd = 2.4
  LengthRev = 0
  Placement = pos=(108.3,29,65.23) rot=(0,1,0;1.5708rad)
  Solid = true
  Symmetric = false
FEATURE [Part::Box] Box013  label="frontCaseScrewPillarBracket002"
  AttacherType = Attacher::AttachEngine3D
  Height = 2.4
  Length = 22
  Placement = pos=(87,28,2.3) rot=(0,0,1;0rad)
  Width = 7
FEATURE [Part::Box] Box014  label="frontCaseScrewPillarBracket003"
  AttacherType = Attacher::AttachEngine3D
  Height = 2.4
  Length = 22
  Placement = pos=(87,28,67.3) rot=(0,0,1;0rad)
  Width = 7
FEATURE [Part::Feature] Face087
  shape: bbox 4.8 x 30.2 x 2e-07 mm, 1 faces, 0 solids (baked)
FEATURE [Part::Revolution] Revolve091  label="frontCaseScrewPost004"
  Angle = 360
  Axis = (0,1,0)
  Base = (0,0,0)
  FaceMakerClass = Part::FaceMakerBullseye
  Placement = pos=(89.5,4.5,3.5) rot=(0,0,1;0rad)
  Solid = false
  Source = -> Face087
  Symmetric = false
FEATURE [Part::Feature] Face088
  shape: bbox 4.8 x 30.2 x 2e-07 mm, 1 faces, 0 solids (baked)
FEATURE [Part::Revolution] Revolve092  label="frontCaseScrewPost005"
  Angle = 360
  Axis = (0,1,0)
  Base = (0,0,0)
  FaceMakerClass = Part::FaceMakerBullseye
  Placement = pos=(89.5,4.5,68.5) rot=(0,0,1;0rad)
  Solid = false
  Source = -> Face088
  Symmetric = false
FEATURE [Part::Feature] Face089
  shape: bbox 3.5 x 30.2 x 2e-07 mm, 1 faces, 0 solids (baked)
FEATURE [Part::Revolution] Revolve093  label="backCaseScrewPost002"
  Angle = 360
  Axis = (0,1,0)
  Base = (0,0,0)
  FaceMakerClass = Part::FaceMakerBullseye
  Placement = pos=(12.5,4.5,10) rot=(0,0,1;0rad)
  Solid = false
  Source = -> Face089
  Symmetric = false
FEATURE [Part::Feature] Face090
  shape: bbox 3.5 x 30.2 x 2e-07 mm, 1 faces, 0 solids (baked)
FEATURE [Part::Revolution] Revolve094  label="backCaseScrewPost003"
  Angle = 360
  Axis = (0,1,0)
  Base = (0,0,0)
  FaceMakerClass = Part::FaceMakerBullseye
  Placement = pos=(12.5,4.5,62) rot=(0,0,1;0rad)
  Solid = false
  Source = -> Face090
  Symmetric = false
FEATURE [Part::Box] Box015  label="Cube011"
  AttacherType = Attacher::AttachEngine3D
  Height = 28.8
  Length = 3
  Placement = pos=(107.3,28,21.6) rot=(0,0,1;0rad)
  Width = 7
FEATURE [Part::Box] Box016  label="Cube012"
  AttacherType = Attacher::AttachEngine3D
  Height = 3
  Length = 7.4
  Placement = pos=(107.3,28,18.6) rot=(0,0,1;0rad)
  Width = 7
FEATURE [Part::Box] Box017  label="Cube013"
  AttacherType = Attacher::AttachEngine3D
  Height = 3
  Length = 7.4
  Placement = pos=(107.3,28,50.4) rot=(0,0,1;0rad)
  Width = 7
FEATURE [Part::Cylinder] Cylinder024
  Angle = 360
  AttacherType = Attacher::AttachEngine3D
  Height = 20
  Placement = pos=(0,0,36.15) rot=(0,0,1;0rad)
  Radius = 14.3
FEATURE [Part::Cylinder] Cylinder025
  Angle = 360
  AttacherType = Attacher::AttachEngine3D
  Height = 10
  Placement = pos=(0,0,36.15) rot=(0,0,1;0rad)
  Radius = 4
FEATURE [Part::MultiFuse] Fusion066  label="removeToCreteHoleForPlugHousing009"
  Placement = pos=(70,19,36) rot=(0,1,0;1.5708rad)
  Shapes = -> [Cylinder024,Cylinder025]
FEATURE [Part::MultiFuse] Fusion065  label="plugHousingBracketHolder002"
  Shapes = -> [Box017,Box015,Box016]
FEATURE [Part::Cut] Cut025  label="plugHousingBracketHolder003"
  Base = -> Fusion065
  Placement = pos=(7,0,0) rot=(0,0,1;0rad)
  Tool = -> Fusion066
FEATURE [Sketcher::SketchObject] Sketch047
  FullyConstrained = false
  Placement = pos=(0,0,0) rot=(1,0,0;1.5708rad)
  sketch-geometry (24):
    g0: ArcOfCircle CenterX=-4 CenterY=-10.5 CenterZ=0 NormalX=0 NormalY=0 NormalZ=1 AngleXU=0 Radius=1.5 StartAngle=6e-16 EndAngle=3.14159
    g1: ArcOfCircle CenterX=-34.2 CenterY=-10.5 CenterZ=0 NormalX=0 NormalY=0 NormalZ=1 AngleXU=0 Radius=1.5 StartAngle=0 EndAngle=3.14159
    g2: ArcOfCircle CenterX=-34.2 CenterY=-27.7 CenterZ=0 NormalX=0 NormalY=0 NormalZ=1 AngleXU=0 Radius=1.5 StartAngle=3.14159 EndAngle=6.28319
    g3: ArcOfCircle CenterX=-4 CenterY=-27.7 CenterZ=0 NormalX=0 NormalY=0 NormalZ=1 AngleXU=0 Radius=1.5 StartAngle=3.1416 EndAngle=6.28319
    g4: ArcOfCircle CenterX=-10 CenterY=-4.3 CenterZ=0 NormalX=0 NormalY=0 NormalZ=1 AngleXU=0 Radius=1.5 StartAngle=2e-16 EndAngle=3.14159
    g5: ArcOfCircle CenterX=-16.1 CenterY=-1.8 CenterZ=0 NormalX=0 NormalY=0 NormalZ=1 AngleXU=0 Radius=1.5 StartAngle=5e-16 EndAngle=3.14159
    g6: ArcOfCircle CenterX=-22.1 CenterY=-1.8 CenterZ=0 NormalX=0 NormalY=0 NormalZ=1 AngleXU=0 Radius=1.5 StartAngle=5e-16 EndAngle=3.14159
    g7: ArcOfCircle CenterX=-28.2 CenterY=-4.3 CenterZ=0 NormalX=0 NormalY=0 NormalZ=1 AngleXU=0 Radius=1.5 StartAngle=2e-16 EndAngle=3.14159
    g8: ArcOfCircle CenterX=-10 CenterY=-33.9 CenterZ=0 NormalX=0 NormalY=0 NormalZ=1 AngleXU=0 Radius=1.5 StartAngle=3.14159 EndAngle=6.28319
    g9: ArcOfCircle CenterX=-16.1 CenterY=-36.4 CenterZ=0 NormalX=0 NormalY=0 NormalZ=1 AngleXU=0 Radius=1.5 StartAngle=3.14159 EndAngle=6.28319
    g10: ArcOfCircle CenterX=-22.1 CenterY=-36.4 CenterZ=0 NormalX=0 NormalY=0 NormalZ=1 AngleXU=0 Radius=1.5 StartAngle=3.14159 EndAngle=6.28319
    g11: ArcOfCircle CenterX=-28.2 CenterY=-33.9 CenterZ=0 NormalX=0 NormalY=0 NormalZ=1 AngleXU=0 Radius=1.5 StartAngle=3.14159 EndAngle=6.28319
    g12: LineSegment StartX=-35.7 StartY=-10.5 StartZ=0 EndX=-35.7 EndY=-27.7 EndZ=0
    g13: LineSegment StartX=-32.7 StartY=-10.5 StartZ=0 EndX=-32.7 EndY=-27.7 EndZ=0
    g14: LineSegment StartX=-29.7 StartY=-33.9 StartZ=0 EndX=-29.7 EndY=-4.3 EndZ=0
    g15: LineSegment StartX=-26.7 StartY=-33.9 StartZ=0 EndX=-26.7 EndY=-4.3 EndZ=0
    g16: LineSegment StartX=-2.5 StartY=-10.5 StartZ=0 EndX=-2.5 EndY=-27.7 EndZ=0
    g17: LineSegment StartX=-8.5 StartY=-4.3 StartZ=0 EndX=-8.5 EndY=-33.9 EndZ=0
    g18: LineSegment StartX=-5.5 StartY=-10.5 StartZ=0 EndX=-5.5 EndY=-27.7 EndZ=0
    g19: LineSegment StartX=-11.5 StartY=-4.3 StartZ=0 EndX=-11.5 EndY=-33.9 EndZ=0
    g20: LineSegment StartX=-14.6 StartY=-1.8 StartZ=0 EndX=-14.6 EndY=-36.4 EndZ=0
    g21: LineSegment StartX=-17.6 StartY=-1.8 StartZ=0 EndX=-17.6 EndY=-36.4 EndZ=0
    g22: LineSegment StartX=-20.6 StartY=-36.4 StartZ=0 EndX=-20.6 EndY=-1.8 EndZ=0
    g23: LineSegment StartX=-23.6 StartY=-1.8 StartZ=0 EndX=-23.6 EndY=-36.4 EndZ=0
  constraints (48):
    c: Block(g0)
    c: Block(g1)
    c: Block(g2)
    c: Block(g3)
    c: Block(g4)
    c: Block(g5)
    c: Block(g6)
    c: Block(g7)
    c: Block(g8)
    c: Block(g9)
    c: Block(g10)
    c: Block(g11)
    c: Coincident(g12,g1)
    c: Coincident(g12,g2)
    c: Vertical(g12)
    c: Coincident(g13,g1)
    c: Coincident(g13,g2)
    c: Vertical(g13)
    c: Coincident(g14,g11)
    c: Coincident(g14,g7)
    c: Vertical(g14)
    c: Coincident(g15,g11)
    c: Coincident(g15,g7)
    c: Vertical(g15)
    c: Coincident(g16,g0)
    c: Coincident(g16,g3)
    c: Vertical(g16)
    c: Coincident(g17,g4)
    c: Coincident(g17,g8)
    c: Vertical(g17)
    c: Coincident(g18,g0)
    c: Coincident(g18,g3)
    c: Vertical(g18)
    c: Coincident(g19,g4)
    c: Coincident(g19,g8)
    c: Vertical(g19)
    c: Coincident(g20,g5)
    c: Coincident(g20,g9)
    c: Vertical(g20)
    c: Coincident(g21,g5)
    c: Coincident(g21,g9)
    c: Vertical(g21)
    c: Coincident(g22,g10)
    c: Coincident(g22,g6)
    c: Vertical(g22)
    c: Coincident(g23,g6)
    c: Coincident(g23,g10)
    c: Vertical(g23)
FEATURE [Part::Extrusion] Extrude038  label="removeToCreateFanGrillHoles001"
  Base = -> Sketch047
  Dir = (0,-1,6e-16)
  DirMode = 2
  FaceMakerClass = Part::FaceMakerBullseye
  LengthFwd = 10
  LengthRev = 0
  Placement = pos=(65.4,44,54.82) rot=(0,0,1;0rad)
  Solid = true
  Symmetric = false
FEATURE [Part::Feature] Wire004
  shape: bbox 11 x 5.2 x 2e-07 mm, 0 faces, 0 solids (baked)
FEATURE [Part::Revolution] Revolve095
  Angle = 360
  Axis = (0,1,0)
  Base = (0,0,0)
  FaceMakerClass = Part::FaceMakerBullseye
  Placement = pos=(30.3,38,19.7) rot=(0,0,1;0rad)
  Solid = true
  Source = -> Wire004
  Symmetric = false
FEATURE [Part::Feature] Wire005
  shape: bbox 11 x 5.2 x 2e-07 mm, 0 faces, 0 solids (baked)
FEATURE [Part::Revolution] Revolve096
  Angle = 360
  Axis = (0,1,0)
  Base = (0,0,0)
  FaceMakerClass = Part::FaceMakerBullseye
  Placement = pos=(30.3,38,51.7) rot=(0,0,1;0rad)
  Solid = true
  Source = -> Wire005
  Symmetric = false
FEATURE [Part::Feature] Wire006
  shape: bbox 11 x 5.2 x 2e-07 mm, 0 faces, 0 solids (baked)
FEATURE [Part::Revolution] Revolve097
  Angle = 360
  Axis = (0,1,0)
  Base = (0,0,0)
  FaceMakerClass = Part::FaceMakerBullseye
  Placement = pos=(62.3,38,51.7) rot=(0,0,1;0rad)
  Solid = true
  Source = -> Wire006
  Symmetric = false
FEATURE [Part::Feature] Wire007
  shape: bbox 11 x 5.2 x 2e-07 mm, 0 faces, 0 solids (baked)
FEATURE [Part::Revolution] Revolve098
  Angle = 360
  Axis = (0,1,0)
  Base = (0,0,0)
  FaceMakerClass = Part::FaceMakerBullseye
  Placement = pos=(62.3,38,19.7) rot=(0,0,1;0rad)
  Solid = true
  Source = -> Wire007
  Symmetric = false
FEATURE [Part::MultiFuse] Fusion067  label="fanScrewHousing002"
  Shapes = -> [Revolve098,Revolve097,Revolve096,Revolve095]
FEATURE [Part::Feature] Face091 .. Face094  x4 (patterned run collapsed; names and placements below)
  shape: bbox 3.5 x 17.8 x 2e-07 mm, 1 faces, 0 solids (baked)
FEATURE [Part::Revolution] Revolve099  label="removeToCreateScrewAndThreadedInsertHole026"
  Angle = 360
  Axis = (0,1,0)
  Base = (0,0,0)
  FaceMakerClass = Part::FaceMakerBullseye
  Placement = pos=(62.3,30.3,19.7) rot=(0,0,1;0rad)
  Solid = false
  Source = -> Face091
  Symmetric = false
FEATURE [Part::Revolution] Revolve100  label="removeToCreateScrewAndThreadedInsertHole027"
  Angle = 360
  Axis = (0,1,0)
  Base = (0,0,0)
  FaceMakerClass = Part::FaceMakerBullseye
  Placement = pos=(62.3,30.3,51.7) rot=(0,0,1;0rad)
  Solid = false
  Source = -> Face092
  Symmetric = false
FEATURE [Part::Revolution] Revolve101  label="removeToCreateScrewAndThreadedInsertHole028"
  Angle = 360
  Axis = (0,1,0)
  Base = (0,0,0)
  FaceMakerClass = Part::FaceMakerBullseye
  Placement = pos=(30.3,30.3,19.7) rot=(0,0,1;0rad)
  Solid = false
  Source = -> Face093
  Symmetric = false
FEATURE [Part::Revolution] Revolve102  label="removeToCreateScrewAndThreadedInsertHole029"
  Angle = 360
  Axis = (0,1,0)
  Base = (0,0,0)
  FaceMakerClass = Part::FaceMakerBullseye
  Placement = pos=(30.3,30.3,51.7) rot=(0,0,1;0rad)
  Solid = false
  Source = -> Face094
  Symmetric = false
FEATURE [Part::MultiFuse] Fusion068  label="createThreadedInsertHolesForFan002"
  Shapes = -> [Revolve099,Revolve100,Revolve101,Revolve102]
FEATURE [Part::Cut] Cut026  label="fanScrewHousing003"
  Base = -> Fusion067
  Tool = -> Fusion068
FEATURE [Sketcher::SketchObject] Sketch048
  FullyConstrained = false
  Placement = pos=(0,0,0) rot=(1,0,0;1.5708rad)
  sketch-geometry (24):
    g0: ArcOfCircle CenterX=-4 CenterY=-10.5 CenterZ=0 NormalX=0 NormalY=0 NormalZ=1 AngleXU=0 Radius=1.5 StartAngle=6e-16 EndAngle=3.14159
    g1: ArcOfCircle CenterX=-34.2 CenterY=-10.5 CenterZ=0 NormalX=0 NormalY=0 NormalZ=1 AngleXU=0 Radius=1.5 StartAngle=0 EndAngle=3.14159
    g2: ArcOfCircle CenterX=-34.2 CenterY=-27.7 CenterZ=0 NormalX=0 NormalY=0 NormalZ=1 AngleXU=0 Radius=1.5 StartAngle=3.14159 EndAngle=6.28319
    g3: ArcOfCircle CenterX=-4 CenterY=-27.7 CenterZ=0 NormalX=0 NormalY=0 NormalZ=1 AngleXU=0 Radius=1.5 StartAngle=3.1416 EndAngle=6.28319
    g4: ArcOfCircle CenterX=-10 CenterY=-4.3 CenterZ=0 NormalX=0 NormalY=0 NormalZ=1 AngleXU=0 Radius=1.5 StartAngle=2e-16 EndAngle=3.14159
    g5: ArcOfCircle CenterX=-16.1 CenterY=-1.8 CenterZ=0 NormalX=0 NormalY=0 NormalZ=1 AngleXU=0 Radius=1.5 StartAngle=5e-16 EndAngle=3.14159
    g6: ArcOfCircle CenterX=-22.1 CenterY=-1.8 CenterZ=0 NormalX=0 NormalY=0 NormalZ=1 AngleXU=0 Radius=1.5 StartAngle=5e-16 EndAngle=3.14159
    g7: ArcOfCircle CenterX=-28.2 CenterY=-4.3 CenterZ=0 NormalX=0 NormalY=0 NormalZ=1 AngleXU=0 Radius=1.5 StartAngle=2e-16 EndAngle=3.14159
    g8: ArcOfCircle CenterX=-10 CenterY=-33.9 CenterZ=0 NormalX=0 NormalY=0 NormalZ=1 AngleXU=0 Radius=1.5 StartAngle=3.14159 EndAngle=6.28319
    g9: ArcOfCircle CenterX=-16.1 CenterY=-36.4 CenterZ=0 NormalX=0 NormalY=0 NormalZ=1 AngleXU=0 Radius=1.5 StartAngle=3.14159 EndAngle=6.28319
    g10: ArcOfCircle CenterX=-22.1 CenterY=-36.4 CenterZ=0 NormalX=0 NormalY=0 NormalZ=1 AngleXU=0 Radius=1.5 StartAngle=3.14159 EndAngle=6.28319
    g11: ArcOfCircle CenterX=-28.2 CenterY=-33.9 CenterZ=0 NormalX=0 NormalY=0 NormalZ=1 AngleXU=0 Radius=1.5 StartAngle=3.14159 EndAngle=6.28319
    g12: LineSegment StartX=-35.7 StartY=-10.5 StartZ=0 EndX=-35.7 EndY=-27.7 EndZ=0
    g13: LineSegment StartX=-32.7 StartY=-10.5 StartZ=0 EndX=-32.7 EndY=-27.7 EndZ=0
    g14: LineSegment StartX=-29.7 StartY=-33.9 StartZ=0 EndX=-29.7 EndY=-4.3 EndZ=0
    g15: LineSegment StartX=-26.7 StartY=-33.9 StartZ=0 EndX=-26.7 EndY=-4.3 EndZ=0
    g16: LineSegment StartX=-2.5 StartY=-10.5 StartZ=0 EndX=-2.5 EndY=-27.7 EndZ=0
    g17: LineSegment StartX=-8.5 StartY=-4.3 StartZ=0 EndX=-8.5 EndY=-33.9 EndZ=0
    g18: LineSegment StartX=-5.5 StartY=-10.5 StartZ=0 EndX=-5.5 EndY=-27.7 EndZ=0
    g19: LineSegment StartX=-11.5 StartY=-4.3 StartZ=0 EndX=-11.5 EndY=-33.9 EndZ=0
    g20: LineSegment StartX=-14.6 StartY=-1.8 StartZ=0 EndX=-14.6 EndY=-36.4 EndZ=0
    g21: LineSegment StartX=-17.6 StartY=-1.8 StartZ=0 EndX=-17.6 EndY=-36.4 EndZ=0
    g22: LineSegment StartX=-20.6 StartY=-36.4 StartZ=0 EndX=-20.6 EndY=-1.8 EndZ=0
    g23: LineSegment StartX=-23.6 StartY=-1.8 StartZ=0 EndX=-23.6 EndY=-36.4 EndZ=0
  constraints (48):
    c: Block(g0)
    c: Block(g1)
    c: Block(g2)
    c: Block(g3)
    c: Block(g4)
    c: Block(g5)
    c: Block(g6)
    c: Block(g7)
    c: Block(g8)
    c: Block(g9)
    c: Block(g10)
    c: Block(g11)
    c: Coincident(g12,g1)
    c: Coincident(g12,g2)
    c: Vertical(g12)
    c: Coincident(g13,g1)
    c: Coincident(g13,g2)
    c: Vertical(g13)
    c: Coincident(g14,g11)
    c: Coincident(g14,g7)
    c: Vertical(g14)
    c: Coincident(g15,g11)
    c: Coincident(g15,g7)
    c: Vertical(g15)
    c: Coincident(g16,g0)
    c: Coincident(g16,g3)
    c: Vertical(g16)
    c: Coincident(g17,g4)
    c: Coincident(g17,g8)
    c: Vertical(g17)
    c: Coincident(g18,g0)
    c: Coincident(g18,g3)
    c: Vertical(g18)
    c: Coincident(g19,g4)
    c: Coincident(g19,g8)
    c: Vertical(g19)
    c: Coincident(g20,g5)
    c: Coincident(g20,g9)
    c: Vertical(g20)
    c: Coincident(g21,g5)
    c: Coincident(g21,g9)
    c: Vertical(g21)
    c: Coincident(g22,g10)
    c: Coincident(g22,g6)
    c: Vertical(g22)
    c: Coincident(g23,g6)
    c: Coincident(g23,g10)
    c: Vertical(g23)
FEATURE [Part::Extrusion] Extrude039  label="removeToCreateFanGrillHoles002"
  Base = -> Sketch048
  Dir = (0,-1,6e-16)
  DirMode = 2
  FaceMakerClass = Part::FaceMakerBullseye
  LengthFwd = 10
  LengthRev = 0
  Placement = pos=(65.4,44,54.82) rot=(0,0,1;0rad)
  Solid = true
  Symmetric = false
FEATURE [Part::Cut] Cut027  label="fanScrewHousing004"
  Base = -> Cut026
  Tool = -> Extrude038
FEATURE [Part::Cut] Cut028  label="top014"
  Base = -> Fillet026
  Tool = -> Extrude039
FEATURE [Part::Feature] Face095 .. Face098  x4 (patterned run collapsed; names and placements below)
  shape: bbox 3.5 x 17.8 x 2e-07 mm, 1 faces, 0 solids (baked)
FEATURE [Part::Revolution] Revolve103  label="removeToCreateScrewAndThreadedInsertHole030"
  Angle = 360
  Axis = (0,1,0)
  Base = (0,0,0)
  FaceMakerClass = Part::FaceMakerBullseye
  Placement = pos=(62.3,30.3,19.7) rot=(0,0,1;0rad)
  Solid = false
  Source = -> Face095
  Symmetric = false
FEATURE [Part::Revolution] Revolve104  label="removeToCreateScrewAndThreadedInsertHole031"
  Angle = 360
  Axis = (0,1,0)
  Base = (0,0,0)
  FaceMakerClass = Part::FaceMakerBullseye
  Placement = pos=(62.3,30.3,51.7) rot=(0,0,1;0rad)
  Solid = false
  Source = -> Face096
  Symmetric = false
FEATURE [Part::Revolution] Revolve105  label="removeToCreateScrewAndThreadedInsertHole032"
  Angle = 360
  Axis = (0,1,0)
  Base = (0,0,0)
  FaceMakerClass = Part::FaceMakerBullseye
  Placement = pos=(30.3,30.3,19.7) rot=(0,0,1;0rad)
  Solid = false
  Source = -> Face097
  Symmetric = false
FEATURE [Part::Revolution] Revolve106  label="removeToCreateScrewAndThreadedInsertHole033"
  Angle = 360
  Axis = (0,1,0)
  Base = (0,0,0)
  FaceMakerClass = Part::FaceMakerBullseye
  Placement = pos=(30.3,30.3,51.7) rot=(0,0,1;0rad)
  Solid = false
  Source = -> Face098
  Symmetric = false
FEATURE [Part::MultiFuse] Fusion069  label="createThreadedInsertHolesForFan003"
  Shapes = -> [Revolve103,Revolve104,Revolve105,Revolve106]
FEATURE [Part::Cut] Cut029  label="top015"
  Base = -> Cut028
  Tool = -> Fusion054
FEATURE [Part::Cut] Cut030  label="fanScrewHousing005"
  Base = -> Cut027
  Tool = -> Fusion069
FEATURE [Part::Cylinder] Cylinder026  label="removeToCreteHoleForPlugHousing010"
  Angle = 360
  AttacherType = Attacher::AttachEngine3D
  Height = 20
  Placement = pos=(-2,19,36) rot=(0,1,0;1.5708rad)
  Radius = 14.3
FEATURE [Part::Box] Box018  label="removeToCreteHoleForPlugHousing011"
  AttacherType = Attacher::AttachEngine3D
  Height = 28.6
  Length = 10
  Placement = pos=(-2,0,21.7) rot=(0,0,1;0rad)
  Width = 19
FEATURE [Part::Box] Box019  label="wireHolderBottomCaseBit"
  AttacherType = Attacher::AttachEngine3D
  Height = 28
  Length = 3
  Placement = pos=(0,0,22) rot=(0,0,1;0rad)
  Width = 21
FEATURE [Part::Cylinder] Cylinder027  label="removeToCreteHoleForPlugHousing012"
  Angle = 360
  AttacherType = Attacher::AttachEngine3D
  Height = 20
  Placement = pos=(-2,19,36) rot=(0,1,0;1.5708rad)
  Radius = 14.3
FEATURE [Part::Cut] Cut031  label="wireHolderBottomCaseBit001"
  Base = -> Box019
  Tool = -> Cylinder027
FEATURE [Part::MultiFuse] Fusion070  label="removeToCreteHoleForPlugHousing013"
  Shapes = -> [Box018,Cylinder026]
FEATURE [Part::Cut] Cut032  label="top016"
  Base = -> Cut029
  Tool = -> Fusion070
